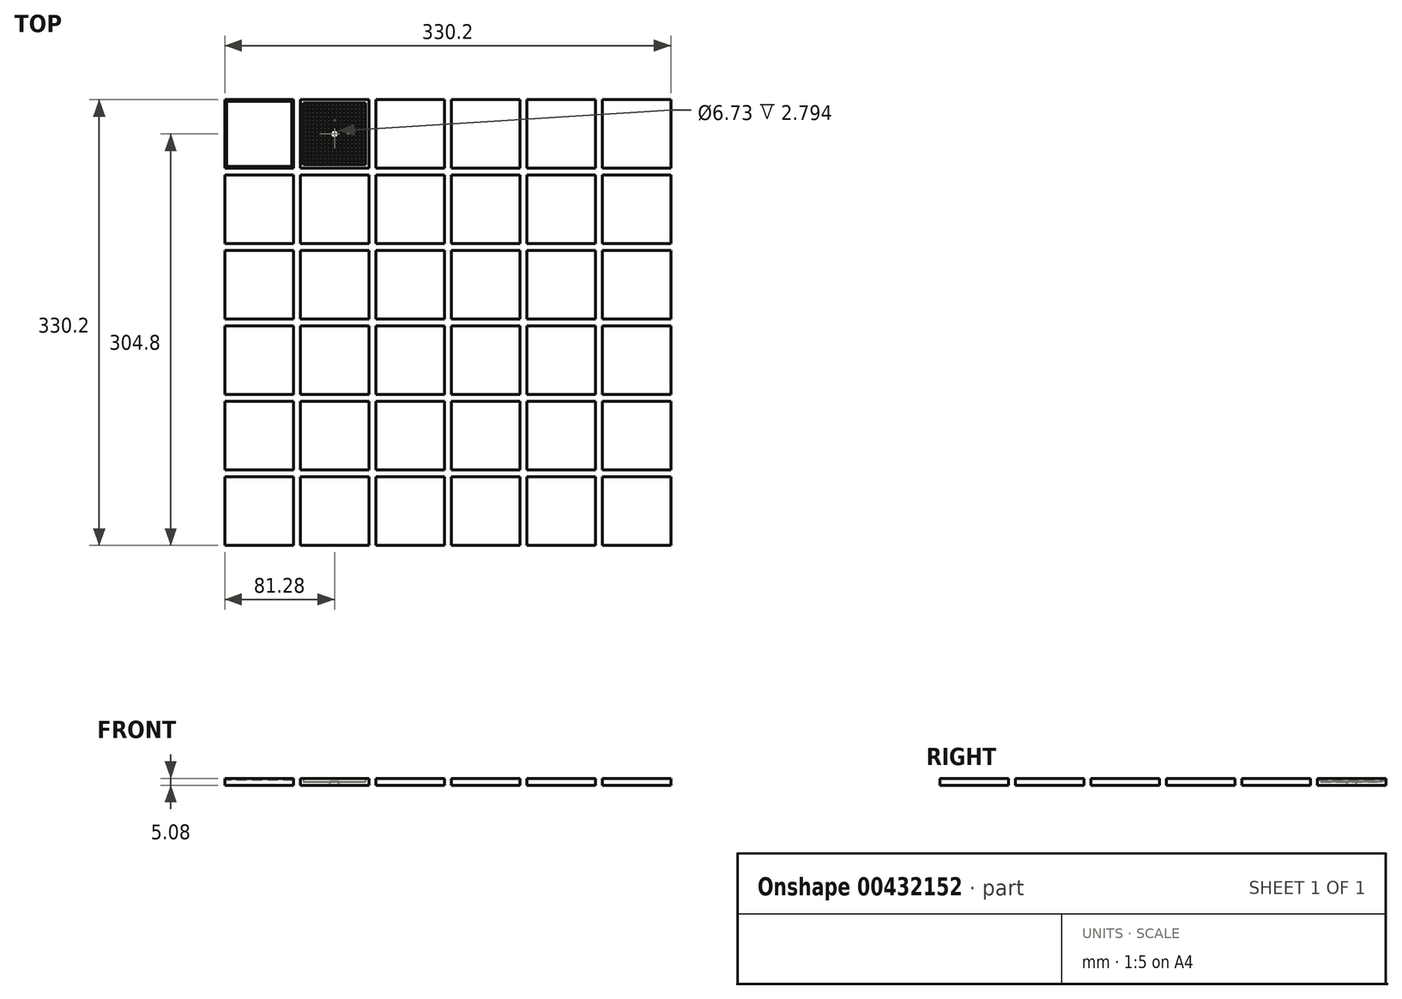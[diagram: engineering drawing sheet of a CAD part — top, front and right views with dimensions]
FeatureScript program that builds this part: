
annotation { "Feature Type Name" : "Feature", "Feature Type Description" : "" }
export const myFeature = defineFeature(function(context is Context, id is Id, definition is map)
    precondition{}
    {
        {
            var Q0;
            Q0=qCreatedBy(makeId("Top.planeOp"),FACE);
            var sketch = newSketch(context, id + "F0", { "sketchPlane" : qUnion([Q0])});
            skLineSegment(sketch, "E0.bottom", {"start": v(0, 0) * mm, "end": v(50.8, 0) * mm});
            skLineSegment(sketch, "E0.top", {"start": v(0, 50.8) * mm, "end": v(50.8, 50.8) * mm});
            skLineSegment(sketch, "E0.left", {"start": v(0, 0) * mm, "end": v(0, 50.8) * mm});
            skLineSegment(sketch, "E0.right", {"start": v(50.8, 0) * mm, "end": v(50.8, 50.8) * mm});
            skLineSegment(sketch, "E1.0.1.0", {"start": v(0, 55.88) * mm, "end": v(0, 106.68) * mm});
            skLineSegment(sketch, "E1.0.1.1", {"start": v(0, 106.68) * mm, "end": v(50.8, 106.68) * mm});
            skLineSegment(sketch, "E1.0.1.2", {"start": v(50.8, 55.88) * mm, "end": v(50.8, 106.68) * mm});
            skLineSegment(sketch, "E1.0.1.3", {"start": v(0, 55.88) * mm, "end": v(50.8, 55.88) * mm});
            skLineSegment(sketch, "E1.0.2.0", {"start": v(0, 111.76) * mm, "end": v(0, 162.56) * mm});
            skLineSegment(sketch, "E1.0.2.1", {"start": v(0, 162.56) * mm, "end": v(50.8, 162.56) * mm});
            skLineSegment(sketch, "E1.0.2.2", {"start": v(50.8, 111.76) * mm, "end": v(50.8, 162.56) * mm});
            skLineSegment(sketch, "E1.0.2.3", {"start": v(0, 111.76) * mm, "end": v(50.8, 111.76) * mm});
            skLineSegment(sketch, "E1.0.3.0", {"start": v(0, 167.64) * mm, "end": v(0, 218.44) * mm});
            skLineSegment(sketch, "E1.0.3.1", {"start": v(0, 218.44) * mm, "end": v(50.8, 218.44) * mm});
            skLineSegment(sketch, "E1.0.3.2", {"start": v(50.8, 167.64) * mm, "end": v(50.8, 218.44) * mm});
            skLineSegment(sketch, "E1.0.3.3", {"start": v(0, 167.64) * mm, "end": v(50.8, 167.64) * mm});
            skLineSegment(sketch, "E1.0.4.0", {"start": v(0, 223.52) * mm, "end": v(0, 274.32) * mm});
            skLineSegment(sketch, "E1.0.4.1", {"start": v(0, 274.32) * mm, "end": v(50.8, 274.32) * mm});
            skLineSegment(sketch, "E1.0.4.2", {"start": v(50.8, 223.52) * mm, "end": v(50.8, 274.32) * mm});
            skLineSegment(sketch, "E1.0.4.3", {"start": v(0, 223.52) * mm, "end": v(50.8, 223.52) * mm});
            skLineSegment(sketch, "E1.0.5.0", {"start": v(0, 279.4) * mm, "end": v(0, 330.2) * mm});
            skLineSegment(sketch, "E1.0.5.1", {"start": v(0, 330.2) * mm, "end": v(50.8, 330.2) * mm});
            skLineSegment(sketch, "E1.0.5.2", {"start": v(50.8, 279.4) * mm, "end": v(50.8, 330.2) * mm});
            skLineSegment(sketch, "E1.0.5.3", {"start": v(0, 279.4) * mm, "end": v(50.8, 279.4) * mm});
            skLineSegment(sketch, "E1.1.0.0", {"start": v(-55.88, 0) * mm, "end": v(-55.88, 50.8) * mm});
            skLineSegment(sketch, "E1.1.0.1", {"start": v(-55.88, 50.8) * mm, "end": v(-5.08, 50.8) * mm});
            skLineSegment(sketch, "E1.1.0.2", {"start": v(-5.08, 0) * mm, "end": v(-5.08, 50.8) * mm});
            skLineSegment(sketch, "E1.1.0.3", {"start": v(-55.88, 0) * mm, "end": v(-5.08, 0) * mm});
            skLineSegment(sketch, "E1.1.1.0", {"start": v(-55.88, 55.88) * mm, "end": v(-55.88, 106.68) * mm});
            skLineSegment(sketch, "E1.1.1.1", {"start": v(-55.88, 106.68) * mm, "end": v(-5.08, 106.68) * mm});
            skLineSegment(sketch, "E1.1.1.2", {"start": v(-5.08, 55.88) * mm, "end": v(-5.08, 106.68) * mm});
            skLineSegment(sketch, "E1.1.1.3", {"start": v(-55.88, 55.88) * mm, "end": v(-5.08, 55.88) * mm});
            skLineSegment(sketch, "E1.1.2.0", {"start": v(-55.88, 111.76) * mm, "end": v(-55.88, 162.56) * mm});
            skLineSegment(sketch, "E1.1.2.1", {"start": v(-55.88, 162.56) * mm, "end": v(-5.08, 162.56) * mm});
            skLineSegment(sketch, "E1.1.2.2", {"start": v(-5.08, 111.76) * mm, "end": v(-5.08, 162.56) * mm});
            skLineSegment(sketch, "E1.1.2.3", {"start": v(-55.88, 111.76) * mm, "end": v(-5.08, 111.76) * mm});
            skLineSegment(sketch, "E1.1.3.0", {"start": v(-55.88, 167.64) * mm, "end": v(-55.88, 218.44) * mm});
            skLineSegment(sketch, "E1.1.3.1", {"start": v(-55.88, 218.44) * mm, "end": v(-5.08, 218.44) * mm});
            skLineSegment(sketch, "E1.1.3.2", {"start": v(-5.08, 167.64) * mm, "end": v(-5.08, 218.44) * mm});
            skLineSegment(sketch, "E1.1.3.3", {"start": v(-55.88, 167.64) * mm, "end": v(-5.08, 167.64) * mm});
            skLineSegment(sketch, "E1.1.4.0", {"start": v(-55.88, 223.52) * mm, "end": v(-55.88, 274.32) * mm});
            skLineSegment(sketch, "E1.1.4.1", {"start": v(-55.88, 274.32) * mm, "end": v(-5.08, 274.32) * mm});
            skLineSegment(sketch, "E1.1.4.2", {"start": v(-5.08, 223.52) * mm, "end": v(-5.08, 274.32) * mm});
            skLineSegment(sketch, "E1.1.4.3", {"start": v(-55.88, 223.52) * mm, "end": v(-5.08, 223.52) * mm});
            skLineSegment(sketch, "E1.1.5.0", {"start": v(-55.88, 279.4) * mm, "end": v(-55.88, 330.2) * mm});
            skLineSegment(sketch, "E1.1.5.1", {"start": v(-55.88, 330.2) * mm, "end": v(-5.08, 330.2) * mm});
            skLineSegment(sketch, "E1.1.5.2", {"start": v(-5.08, 279.4) * mm, "end": v(-5.08, 330.2) * mm});
            skLineSegment(sketch, "E1.1.5.3", {"start": v(-55.88, 279.4) * mm, "end": v(-5.08, 279.4) * mm});
            skLineSegment(sketch, "E1.2.0.0", {"start": v(-111.76, 0) * mm, "end": v(-111.76, 50.8) * mm});
            skLineSegment(sketch, "E1.2.0.1", {"start": v(-111.76, 50.8) * mm, "end": v(-60.96, 50.8) * mm});
            skLineSegment(sketch, "E1.2.0.2", {"start": v(-60.96, 0) * mm, "end": v(-60.96, 50.8) * mm});
            skLineSegment(sketch, "E1.2.0.3", {"start": v(-111.76, 0) * mm, "end": v(-60.96, 0) * mm});
            skLineSegment(sketch, "E1.2.1.0", {"start": v(-111.76, 55.88) * mm, "end": v(-111.76, 106.68) * mm});
            skLineSegment(sketch, "E1.2.1.1", {"start": v(-111.76, 106.68) * mm, "end": v(-60.96, 106.68) * mm});
            skLineSegment(sketch, "E1.2.1.2", {"start": v(-60.96, 55.88) * mm, "end": v(-60.96, 106.68) * mm});
            skLineSegment(sketch, "E1.2.1.3", {"start": v(-111.76, 55.88) * mm, "end": v(-60.96, 55.88) * mm});
            skLineSegment(sketch, "E1.2.2.0", {"start": v(-111.76, 111.76) * mm, "end": v(-111.76, 162.56) * mm});
            skLineSegment(sketch, "E1.2.2.1", {"start": v(-111.76, 162.56) * mm, "end": v(-60.96, 162.56) * mm});
            skLineSegment(sketch, "E1.2.2.2", {"start": v(-60.96, 111.76) * mm, "end": v(-60.96, 162.56) * mm});
            skLineSegment(sketch, "E1.2.2.3", {"start": v(-111.76, 111.76) * mm, "end": v(-60.96, 111.76) * mm});
            skLineSegment(sketch, "E1.2.3.0", {"start": v(-111.76, 167.64) * mm, "end": v(-111.76, 218.44) * mm});
            skLineSegment(sketch, "E1.2.3.1", {"start": v(-111.76, 218.44) * mm, "end": v(-60.96, 218.44) * mm});
            skLineSegment(sketch, "E1.2.3.2", {"start": v(-60.96, 167.64) * mm, "end": v(-60.96, 218.44) * mm});
            skLineSegment(sketch, "E1.2.3.3", {"start": v(-111.76, 167.64) * mm, "end": v(-60.96, 167.64) * mm});
            skLineSegment(sketch, "E1.2.4.0", {"start": v(-111.76, 223.52) * mm, "end": v(-111.76, 274.32) * mm});
            skLineSegment(sketch, "E1.2.4.1", {"start": v(-111.76, 274.32) * mm, "end": v(-60.96, 274.32) * mm});
            skLineSegment(sketch, "E1.2.4.2", {"start": v(-60.96, 223.52) * mm, "end": v(-60.96, 274.32) * mm});
            skLineSegment(sketch, "E1.2.4.3", {"start": v(-111.76, 223.52) * mm, "end": v(-60.96, 223.52) * mm});
            skLineSegment(sketch, "E1.2.5.0", {"start": v(-111.76, 279.4) * mm, "end": v(-111.76, 330.2) * mm});
            skLineSegment(sketch, "E1.2.5.1", {"start": v(-111.76, 330.2) * mm, "end": v(-60.96, 330.2) * mm});
            skLineSegment(sketch, "E1.2.5.2", {"start": v(-60.96, 279.4) * mm, "end": v(-60.96, 330.2) * mm});
            skLineSegment(sketch, "E1.2.5.3", {"start": v(-111.76, 279.4) * mm, "end": v(-60.96, 279.4) * mm});
            skLineSegment(sketch, "E1.3.0.0", {"start": v(-167.64, 0) * mm, "end": v(-167.64, 50.8) * mm});
            skLineSegment(sketch, "E1.3.0.1", {"start": v(-167.64, 50.8) * mm, "end": v(-116.84, 50.8) * mm});
            skLineSegment(sketch, "E1.3.0.2", {"start": v(-116.84, 0) * mm, "end": v(-116.84, 50.8) * mm});
            skLineSegment(sketch, "E1.3.0.3", {"start": v(-167.64, 0) * mm, "end": v(-116.84, 0) * mm});
            skLineSegment(sketch, "E1.3.1.0", {"start": v(-167.64, 55.88) * mm, "end": v(-167.64, 106.68) * mm});
            skLineSegment(sketch, "E1.3.1.1", {"start": v(-167.64, 106.68) * mm, "end": v(-116.84, 106.68) * mm});
            skLineSegment(sketch, "E1.3.1.2", {"start": v(-116.84, 55.88) * mm, "end": v(-116.84, 106.68) * mm});
            skLineSegment(sketch, "E1.3.1.3", {"start": v(-167.64, 55.88) * mm, "end": v(-116.84, 55.88) * mm});
            skLineSegment(sketch, "E1.3.2.0", {"start": v(-167.64, 111.76) * mm, "end": v(-167.64, 162.56) * mm});
            skLineSegment(sketch, "E1.3.2.1", {"start": v(-167.64, 162.56) * mm, "end": v(-116.84, 162.56) * mm});
            skLineSegment(sketch, "E1.3.2.2", {"start": v(-116.84, 111.76) * mm, "end": v(-116.84, 162.56) * mm});
            skLineSegment(sketch, "E1.3.2.3", {"start": v(-167.64, 111.76) * mm, "end": v(-116.84, 111.76) * mm});
            skLineSegment(sketch, "E1.3.3.0", {"start": v(-167.64, 167.64) * mm, "end": v(-167.64, 218.44) * mm});
            skLineSegment(sketch, "E1.3.3.1", {"start": v(-167.64, 218.44) * mm, "end": v(-116.84, 218.44) * mm});
            skLineSegment(sketch, "E1.3.3.2", {"start": v(-116.84, 167.64) * mm, "end": v(-116.84, 218.44) * mm});
            skLineSegment(sketch, "E1.3.3.3", {"start": v(-167.64, 167.64) * mm, "end": v(-116.84, 167.64) * mm});
            skLineSegment(sketch, "E1.3.4.0", {"start": v(-167.64, 223.52) * mm, "end": v(-167.64, 274.32) * mm});
            skLineSegment(sketch, "E1.3.4.1", {"start": v(-167.64, 274.32) * mm, "end": v(-116.84, 274.32) * mm});
            skLineSegment(sketch, "E1.3.4.2", {"start": v(-116.84, 223.52) * mm, "end": v(-116.84, 274.32) * mm});
            skLineSegment(sketch, "E1.3.4.3", {"start": v(-167.64, 223.52) * mm, "end": v(-116.84, 223.52) * mm});
            skLineSegment(sketch, "E1.3.5.0", {"start": v(-167.64, 279.4) * mm, "end": v(-167.64, 330.2) * mm});
            skLineSegment(sketch, "E1.3.5.1", {"start": v(-167.64, 330.2) * mm, "end": v(-116.84, 330.2) * mm});
            skLineSegment(sketch, "E1.3.5.2", {"start": v(-116.84, 279.4) * mm, "end": v(-116.84, 330.2) * mm});
            skLineSegment(sketch, "E1.3.5.3", {"start": v(-167.64, 279.4) * mm, "end": v(-116.84, 279.4) * mm});
            skLineSegment(sketch, "E1.4.0.0", {"start": v(-223.52, 0) * mm, "end": v(-223.52, 50.8) * mm});
            skLineSegment(sketch, "E1.4.0.1", {"start": v(-223.52, 50.8) * mm, "end": v(-172.72, 50.8) * mm});
            skLineSegment(sketch, "E1.4.0.2", {"start": v(-172.72, 0) * mm, "end": v(-172.72, 50.8) * mm});
            skLineSegment(sketch, "E1.4.0.3", {"start": v(-223.52, 0) * mm, "end": v(-172.72, 0) * mm});
            skLineSegment(sketch, "E1.4.1.0", {"start": v(-223.52, 55.88) * mm, "end": v(-223.52, 106.68) * mm});
            skLineSegment(sketch, "E1.4.1.1", {"start": v(-223.52, 106.68) * mm, "end": v(-172.72, 106.68) * mm});
            skLineSegment(sketch, "E1.4.1.2", {"start": v(-172.72, 55.88) * mm, "end": v(-172.72, 106.68) * mm});
            skLineSegment(sketch, "E1.4.1.3", {"start": v(-223.52, 55.88) * mm, "end": v(-172.72, 55.88) * mm});
            skLineSegment(sketch, "E1.4.2.0", {"start": v(-223.52, 111.76) * mm, "end": v(-223.52, 162.56) * mm});
            skLineSegment(sketch, "E1.4.2.1", {"start": v(-223.52, 162.56) * mm, "end": v(-172.72, 162.56) * mm});
            skLineSegment(sketch, "E1.4.2.2", {"start": v(-172.72, 111.76) * mm, "end": v(-172.72, 162.56) * mm});
            skLineSegment(sketch, "E1.4.2.3", {"start": v(-223.52, 111.76) * mm, "end": v(-172.72, 111.76) * mm});
            skLineSegment(sketch, "E1.4.3.0", {"start": v(-223.52, 167.64) * mm, "end": v(-223.52, 218.44) * mm});
            skLineSegment(sketch, "E1.4.3.1", {"start": v(-223.52, 218.44) * mm, "end": v(-172.72, 218.44) * mm});
            skLineSegment(sketch, "E1.4.3.2", {"start": v(-172.72, 167.64) * mm, "end": v(-172.72, 218.44) * mm});
            skLineSegment(sketch, "E1.4.3.3", {"start": v(-223.52, 167.64) * mm, "end": v(-172.72, 167.64) * mm});
            skLineSegment(sketch, "E1.4.4.0", {"start": v(-223.52, 223.52) * mm, "end": v(-223.52, 274.32) * mm});
            skLineSegment(sketch, "E1.4.4.1", {"start": v(-223.52, 274.32) * mm, "end": v(-172.72, 274.32) * mm});
            skLineSegment(sketch, "E1.4.4.2", {"start": v(-172.72, 223.52) * mm, "end": v(-172.72, 274.32) * mm});
            skLineSegment(sketch, "E1.4.4.3", {"start": v(-223.52, 223.52) * mm, "end": v(-172.72, 223.52) * mm});
            skLineSegment(sketch, "E1.4.5.0", {"start": v(-223.52, 279.4) * mm, "end": v(-223.52, 330.2) * mm});
            skLineSegment(sketch, "E1.4.5.1", {"start": v(-223.52, 330.2) * mm, "end": v(-172.72, 330.2) * mm});
            skLineSegment(sketch, "E1.4.5.2", {"start": v(-172.72, 279.4) * mm, "end": v(-172.72, 330.2) * mm});
            skLineSegment(sketch, "E1.4.5.3", {"start": v(-223.52, 279.4) * mm, "end": v(-172.72, 279.4) * mm});
            skLineSegment(sketch, "E1.5.0.0", {"start": v(-279.4, 0) * mm, "end": v(-279.4, 50.8) * mm});
            skLineSegment(sketch, "E1.5.0.1", {"start": v(-279.4, 50.8) * mm, "end": v(-228.6, 50.8) * mm});
            skLineSegment(sketch, "E1.5.0.2", {"start": v(-228.6, 0) * mm, "end": v(-228.6, 50.8) * mm});
            skLineSegment(sketch, "E1.5.0.3", {"start": v(-279.4, 0) * mm, "end": v(-228.6, 0) * mm});
            skLineSegment(sketch, "E1.5.1.0", {"start": v(-279.4, 55.88) * mm, "end": v(-279.4, 106.68) * mm});
            skLineSegment(sketch, "E1.5.1.1", {"start": v(-279.4, 106.68) * mm, "end": v(-228.6, 106.68) * mm});
            skLineSegment(sketch, "E1.5.1.2", {"start": v(-228.6, 55.88) * mm, "end": v(-228.6, 106.68) * mm});
            skLineSegment(sketch, "E1.5.1.3", {"start": v(-279.4, 55.88) * mm, "end": v(-228.6, 55.88) * mm});
            skLineSegment(sketch, "E1.5.2.0", {"start": v(-279.4, 111.76) * mm, "end": v(-279.4, 162.56) * mm});
            skLineSegment(sketch, "E1.5.2.1", {"start": v(-279.4, 162.56) * mm, "end": v(-228.6, 162.56) * mm});
            skLineSegment(sketch, "E1.5.2.2", {"start": v(-228.6, 111.76) * mm, "end": v(-228.6, 162.56) * mm});
            skLineSegment(sketch, "E1.5.2.3", {"start": v(-279.4, 111.76) * mm, "end": v(-228.6, 111.76) * mm});
            skLineSegment(sketch, "E1.5.3.0", {"start": v(-279.4, 167.64) * mm, "end": v(-279.4, 218.44) * mm});
            skLineSegment(sketch, "E1.5.3.1", {"start": v(-279.4, 218.44) * mm, "end": v(-228.6, 218.44) * mm});
            skLineSegment(sketch, "E1.5.3.2", {"start": v(-228.6, 167.64) * mm, "end": v(-228.6, 218.44) * mm});
            skLineSegment(sketch, "E1.5.3.3", {"start": v(-279.4, 167.64) * mm, "end": v(-228.6, 167.64) * mm});
            skLineSegment(sketch, "E1.5.4.0", {"start": v(-279.4, 223.52) * mm, "end": v(-279.4, 274.32) * mm});
            skLineSegment(sketch, "E1.5.4.1", {"start": v(-279.4, 274.32) * mm, "end": v(-228.6, 274.32) * mm});
            skLineSegment(sketch, "E1.5.4.2", {"start": v(-228.6, 223.52) * mm, "end": v(-228.6, 274.32) * mm});
            skLineSegment(sketch, "E1.5.4.3", {"start": v(-279.4, 223.52) * mm, "end": v(-228.6, 223.52) * mm});
            skLineSegment(sketch, "E1.5.5.0", {"start": v(-279.4, 279.4) * mm, "end": v(-279.4, 330.2) * mm});
            skLineSegment(sketch, "E1.5.5.1", {"start": v(-279.4, 330.2) * mm, "end": v(-228.6, 330.2) * mm});
            skLineSegment(sketch, "E1.5.5.2", {"start": v(-228.6, 279.4) * mm, "end": v(-228.6, 330.2) * mm});
            skLineSegment(sketch, "E1.5.5.3", {"start": v(-279.4, 279.4) * mm, "end": v(-228.6, 279.4) * mm});
            skLineSegment(sketch, "E1.direction1", {"start": v(0, 0) * mm, "end": v(-55.88, 0) * mm, "construction": true});
            skLineSegment(sketch, "E1.direction2", {"start": v(0, 0) * mm, "end": v(0, 55.88) * mm, "construction": true});
            skSolve(sketch);
        }
        {
            var Q0;
            Q0=makeQuery(id+"F0.imprint","IMPRINT",FACE,{"disambiguationData":[TD([[makeQuery(id+"F0.imprint","IMPRINT",EDGE,{"derivedFrom":sQuery(id+"F0.wireOp",EDGE,"E1.4.2.0")}),-1.0]])]});
            var Q1;
            Q1=makeQuery(id+"F0.imprint","IMPRINT",FACE,{"disambiguationData":[TD([[makeQuery(id+"F0.imprint","IMPRINT",EDGE,{"derivedFrom":sQuery(id+"F0.wireOp",EDGE,"E1.4.5.0")}),-1.0]])]});
            var Q2;
            Q2=makeQuery(id+"F0.imprint","IMPRINT",FACE,{"disambiguationData":[TD([[makeQuery(id+"F0.imprint","IMPRINT",EDGE,{"derivedFrom":sQuery(id+"F0.wireOp",EDGE,"E1.4.3.0")}),-1.0]])]});
            var Q3;
            Q3=makeQuery(id+"F0.imprint","IMPRINT",FACE,{"disambiguationData":[TD([[makeQuery(id+"F0.imprint","IMPRINT",EDGE,{"derivedFrom":sQuery(id+"F0.wireOp",EDGE,"E1.5.0.0")}),-1.0]])]});
            var Q4;
            Q4=makeQuery(id+"F0.imprint","IMPRINT",FACE,{"disambiguationData":[TD([[makeQuery(id+"F0.imprint","IMPRINT",EDGE,{"derivedFrom":sQuery(id+"F0.wireOp",EDGE,"E1.4.4.0")}),-1.0]])]});
            var Q5;
            Q5=makeQuery(id+"F0.imprint","IMPRINT",FACE,{"disambiguationData":[TD([[makeQuery(id+"F0.imprint","IMPRINT",EDGE,{"derivedFrom":sQuery(id+"F0.wireOp",EDGE,"E1.2.4.0")}),-1.0]])]});
            var Q6;
            Q6=makeQuery(id+"F0.imprint","IMPRINT",FACE,{"disambiguationData":[TD([[makeQuery(id+"F0.imprint","IMPRINT",EDGE,{"derivedFrom":sQuery(id+"F0.wireOp",EDGE,"E1.5.2.0")}),-1.0]])]});
            var Q7;
            Q7=makeQuery(id+"F0.imprint","IMPRINT",FACE,{"disambiguationData":[TD([[makeQuery(id+"F0.imprint","IMPRINT",EDGE,{"derivedFrom":sQuery(id+"F0.wireOp",EDGE,"E1.2.5.0")}),-1.0]])]});
            var Q8;
            Q8=makeQuery(id+"F0.imprint","IMPRINT",FACE,{"disambiguationData":[TD([[makeQuery(id+"F0.imprint","IMPRINT",EDGE,{"derivedFrom":sQuery(id+"F0.wireOp",EDGE,"E1.5.3.0")}),-1.0]])]});
            var Q9;
            Q9=makeQuery(id+"F0.imprint","IMPRINT",FACE,{"disambiguationData":[TD([[makeQuery(id+"F0.imprint","IMPRINT",EDGE,{"derivedFrom":sQuery(id+"F0.wireOp",EDGE,"E1.3.0.0")}),-1.0]])]});
            var Q10;
            Q10=makeQuery(id+"F0.imprint","IMPRINT",FACE,{"disambiguationData":[TD([[makeQuery(id+"F0.imprint","IMPRINT",EDGE,{"derivedFrom":sQuery(id+"F0.wireOp",EDGE,"E1.5.4.0")}),-1.0]])]});
            var Q11;
            Q11=makeQuery(id+"F0.imprint","IMPRINT",FACE,{"disambiguationData":[TD([[makeQuery(id+"F0.imprint","IMPRINT",EDGE,{"derivedFrom":sQuery(id+"F0.wireOp",EDGE,"E1.3.1.0")}),-1.0]])]});
            var Q12;
            Q12=makeQuery(id+"F0.imprint","IMPRINT",FACE,{"disambiguationData":[TD([[makeQuery(id+"F0.imprint","IMPRINT",EDGE,{"derivedFrom":sQuery(id+"F0.wireOp",EDGE,"E1.5.5.0")}),-1.0]])]});
            var Q13;
            Q13=makeQuery(id+"F0.imprint","IMPRINT",FACE,{"disambiguationData":[TD([[makeQuery(id+"F0.imprint","IMPRINT",EDGE,{"derivedFrom":sQuery(id+"F0.wireOp",EDGE,"E1.3.2.0")}),-1.0]])]});
            var Q14;
            Q14=makeQuery(id+"F0.imprint","IMPRINT",FACE,{"disambiguationData":[TD([[makeQuery(id+"F0.imprint","IMPRINT",EDGE,{"derivedFrom":sQuery(id+"F0.wireOp",EDGE,"E1.3.3.0")}),-1.0]])]});
            var Q15;
            Q15=makeQuery(id+"F0.imprint","IMPRINT",FACE,{"disambiguationData":[TD([[makeQuery(id+"F0.imprint","IMPRINT",EDGE,{"derivedFrom":sQuery(id+"F0.wireOp",EDGE,"E1.3.4.0")}),-1.0]])]});
            var Q16;
            Q16=makeQuery(id+"F0.imprint","IMPRINT",FACE,{"disambiguationData":[TD([[makeQuery(id+"F0.imprint","IMPRINT",EDGE,{"derivedFrom":sQuery(id+"F0.wireOp",EDGE,"E1.2.3.0")}),-1.0]])]});
            var Q17;
            Q17=makeQuery(id+"F0.imprint","IMPRINT",FACE,{"disambiguationData":[TD([[makeQuery(id+"F0.imprint","IMPRINT",EDGE,{"derivedFrom":sQuery(id+"F0.wireOp",EDGE,"E1.2.1.0")}),-1.0]])]});
            var Q18;
            Q18=makeQuery(id+"F0.imprint","IMPRINT",FACE,{"disambiguationData":[TD([[makeQuery(id+"F0.imprint","IMPRINT",EDGE,{"derivedFrom":sQuery(id+"F0.wireOp",EDGE,"E1.2.2.0")}),-1.0]])]});
            var Q19;
            Q19=makeQuery(id+"F0.imprint","IMPRINT",FACE,{"disambiguationData":[TD([[makeQuery(id+"F0.imprint","IMPRINT",EDGE,{"derivedFrom":sQuery(id+"F0.wireOp",EDGE,"E1.0.1.0")}),-1.0]])]});
            var Q20;
            Q20=makeQuery(id+"F0.imprint","IMPRINT",FACE,{"disambiguationData":[TD([[makeQuery(id+"F0.imprint","IMPRINT",EDGE,{"derivedFrom":sQuery(id+"F0.wireOp",EDGE,"E1.0.2.0")}),-1.0]])]});
            var Q21;
            Q21=makeQuery(id+"F0.imprint","IMPRINT",FACE,{"disambiguationData":[TD([[makeQuery(id+"F0.imprint","IMPRINT",EDGE,{"derivedFrom":sQuery(id+"F0.wireOp",EDGE,"E1.0.3.0")}),-1.0]])]});
            var Q22;
            Q22=makeQuery(id+"F0.imprint","IMPRINT",FACE,{"disambiguationData":[TD([[makeQuery(id+"F0.imprint","IMPRINT",EDGE,{"derivedFrom":sQuery(id+"F0.wireOp",EDGE,"E1.0.4.0")}),-1.0]])]});
            var Q23;
            Q23=makeQuery(id+"F0.imprint","IMPRINT",FACE,{"disambiguationData":[TD([[makeQuery(id+"F0.imprint","IMPRINT",EDGE,{"derivedFrom":sQuery(id+"F0.wireOp",EDGE,"E1.0.5.0")}),-1.0]])]});
            var Q24;
            Q24=makeQuery(id+"F0.imprint","IMPRINT",FACE,{"disambiguationData":[TD([[makeQuery(id+"F0.imprint","IMPRINT",EDGE,{"derivedFrom":sQuery(id+"F0.wireOp",EDGE,"E1.1.0.0")}),-1.0]])]});
            var Q25;
            Q25=makeQuery(id+"F0.imprint","IMPRINT",FACE,{"disambiguationData":[TD([[makeQuery(id+"F0.imprint","IMPRINT",EDGE,{"derivedFrom":sQuery(id+"F0.wireOp",EDGE,"E1.1.1.0")}),-1.0]])]});
            var Q26;
            Q26=makeQuery(id+"F0.imprint","IMPRINT",FACE,{"disambiguationData":[TD([[makeQuery(id+"F0.imprint","IMPRINT",EDGE,{"derivedFrom":sQuery(id+"F0.wireOp",EDGE,"E1.1.2.0")}),-1.0]])]});
            var Q27;
            Q27=makeQuery(id+"F0.imprint","IMPRINT",FACE,{"disambiguationData":[TD([[makeQuery(id+"F0.imprint","IMPRINT",EDGE,{"derivedFrom":sQuery(id+"F0.wireOp",EDGE,"E1.1.3.0")}),-1.0]])]});
            var Q28;
            Q28=makeQuery(id+"F0.imprint","IMPRINT",FACE,{"disambiguationData":[TD([[makeQuery(id+"F0.imprint","IMPRINT",EDGE,{"derivedFrom":sQuery(id+"F0.wireOp",EDGE,"E1.1.4.0")}),-1.0]])]});
            var Q29;
            Q29=makeQuery(id+"F0.imprint","IMPRINT",FACE,{"disambiguationData":[TD([[makeQuery(id+"F0.imprint","IMPRINT",EDGE,{"derivedFrom":sQuery(id+"F0.wireOp",EDGE,"E1.1.5.0")}),-1.0]])]});
            var Q30;
            Q30=makeQuery(id+"F0.imprint","IMPRINT",FACE,{"disambiguationData":[TD([[makeQuery(id+"F0.imprint","IMPRINT",EDGE,{"derivedFrom":sQuery(id+"F0.wireOp",EDGE,"E1.2.0.0")}),-1.0]])]});
            var Q31;
            Q31=makeQuery(id+"F0.imprint","IMPRINT",FACE,{"disambiguationData":[TD([[makeQuery(id+"F0.imprint","IMPRINT",EDGE,{"derivedFrom":sQuery(id+"F0.wireOp",EDGE,"E1.3.5.0")}),-1.0]])]});
            var Q32;
            Q32=makeQuery(id+"F0.imprint","IMPRINT",FACE,{"disambiguationData":[TD([[makeQuery(id+"F0.imprint","IMPRINT",EDGE,{"derivedFrom":sQuery(id+"F0.wireOp",EDGE,"E1.4.0.0")}),-1.0]])]});
            var Q33;
            Q33=makeQuery(id+"F0.imprint","IMPRINT",FACE,{"disambiguationData":[TD([[makeQuery(id+"F0.imprint","IMPRINT",EDGE,{"derivedFrom":sQuery(id+"F0.wireOp",EDGE,"E1.5.1.0")}),-1.0]])]});
            var Q34;
            Q34=makeQuery(id+"F0.imprint","IMPRINT",FACE,{"disambiguationData":[TD([[makeQuery(id+"F0.imprint","IMPRINT",EDGE,{"derivedFrom":sQuery(id+"F0.wireOp",EDGE,"E1.4.1.0")}),-1.0]])]});
            var Q35;
            Q35=makeQuery(id+"F0.imprint","IMPRINT",FACE,{"disambiguationData":[TD([[makeQuery(id+"F0.imprint","IMPRINT",EDGE,{"derivedFrom":sQuery(id+"F0.wireOp",EDGE,"E0.bottom")}),1.0]])]});
            extrude(context, id + "F1", {"entities" : qUnion([Q0, Q1, Q2, Q3, Q4, Q5, Q6, Q7, Q8, Q9, Q10, Q11, Q12, Q13, Q14, Q15, Q16, Q17, Q18, Q19, Q20, Q21, Q22, Q23, Q24, Q25, Q26, Q27, Q28, Q29, Q30, Q31, Q32, Q33, Q34, Q35]), "depth" : 5.08 * mm});
        }
        {
            var Q0;
            Q0=makeQuery(id+"F1.opExtrude","CAP_EDGE",EDGE,{"disambiguationData":[OSD([sQuery(id+"F0.wireOp",EDGE,"E1.5.5.0")])],"isStart":false});
            var Q1;
            Q1=makeQuery(id+"F1.opExtrude","CAP_EDGE",EDGE,{"disambiguationData":[OSD([sQuery(id+"F0.wireOp",EDGE,"E1.5.5.3")])],"isStart":false});
            var Q2;
            Q2=makeQuery(id+"F1.opExtrude","CAP_EDGE",EDGE,{"disambiguationData":[OSD([sQuery(id+"F0.wireOp",EDGE,"E1.5.5.2")])],"isStart":false});
            var Q3;
            Q3=makeQuery(id+"F1.opExtrude","CAP_EDGE",EDGE,{"disambiguationData":[OSD([sQuery(id+"F0.wireOp",EDGE,"E1.5.5.1")])],"isStart":false});
            chamfer(context, id + "F2", {"entities" : qUnion([Q0, Q1, Q2, Q3]), "width" : 1.27 * mm, "tangentPropagation" : true});
        }
        {
            var Q0;
            Q0=makeQuery(id+"F1.opExtrude","CAP_FACE",FACE,{"disambiguationData":[OSD([sQuery(id+"F0.wireOp",EDGE,"E1.4.5.0"),sQuery(id+"F0.wireOp",EDGE,"E1.4.5.1"),sQuery(id+"F0.wireOp",EDGE,"E1.4.5.2"),sQuery(id+"F0.wireOp",EDGE,"E1.4.5.3")])],"isStart":false});
            shell(context, id + "F3", {"entities" : qUnion([Q0]), "thickness" : 2.54 * mm});
        }
        {
            var Q0;
            Q0=makeQuery(id+"F3.opShell","OFFSET_FACE",FACE,{"disambiguationData":[OSD([sQuery(id+"F0.wireOp",EDGE,"E1.4.5.0"),sQuery(id+"F0.wireOp",EDGE,"E1.4.5.1"),sQuery(id+"F0.wireOp",EDGE,"E1.4.5.2"),sQuery(id+"F0.wireOp",EDGE,"E1.4.5.3")])]});
            var sketch = newSketch(context, id + "F4", { "sketchPlane" : qUnion([Q0])});
            skLineSegment(sketch, "E2", {"start": v(-220.98, 327.66) * mm, "end": v(-220.73, 327.66) * mm});
            skLineSegment(sketch, "E3", {"start": v(-220.73, 327.66) * mm, "end": v(-220.73, 327.41) * mm});
            skLineSegment(sketch, "E4", {"start": v(-220.73, 327.41) * mm, "end": v(-220.98, 327.41) * mm});
            skLineSegment(sketch, "E5.bottom", {"start": v(-220.73, 327.41) * mm, "end": v(-218.2, 327.41) * mm});
            skLineSegment(sketch, "E5.top", {"start": v(-220.73, 324.87) * mm, "end": v(-218.2, 324.87) * mm});
            skLineSegment(sketch, "E5.left", {"start": v(-220.73, 327.41) * mm, "end": v(-220.73, 324.87) * mm});
            skLineSegment(sketch, "E5.right", {"start": v(-218.2, 327.41) * mm, "end": v(-218.2, 324.87) * mm});
            skCircle(sketch, "E6", {"center": v(-198.12, 304.8) * mm, "radius": 3.18 * mm});
            skPoint(sketch, "E6.centerSnap0", {"position": v(-220.98, 304.8) * mm});
            skPoint(sketch, "E6.centerSnap1", {"position": v(-198.12, 327.66) * mm});
            skLineSegment(sketch, "E7.0.1.0", {"start": v(-220.73, 322.03) * mm, "end": v(-218.2, 322.03) * mm});
            skLineSegment(sketch, "E7.0.1.1", {"start": v(-220.73, 324.57) * mm, "end": v(-220.73, 322.03) * mm});
            skLineSegment(sketch, "E7.0.1.2", {"start": v(-220.73, 324.57) * mm, "end": v(-218.2, 324.57) * mm});
            skLineSegment(sketch, "E7.0.1.3", {"start": v(-218.2, 324.57) * mm, "end": v(-218.2, 322.03) * mm});
            skLineSegment(sketch, "E7.1.0.0", {"start": v(-217.89, 324.87) * mm, "end": v(-215.35, 324.87) * mm});
            skLineSegment(sketch, "E7.1.0.1", {"start": v(-217.89, 327.41) * mm, "end": v(-217.89, 324.87) * mm});
            skLineSegment(sketch, "E7.1.0.2", {"start": v(-217.89, 327.41) * mm, "end": v(-215.35, 327.41) * mm});
            skLineSegment(sketch, "E7.1.0.3", {"start": v(-215.35, 327.41) * mm, "end": v(-215.35, 324.87) * mm});
            skLineSegment(sketch, "E7.1.1.0", {"start": v(-217.89, 322.03) * mm, "end": v(-215.35, 322.03) * mm});
            skLineSegment(sketch, "E7.1.1.1", {"start": v(-217.89, 324.57) * mm, "end": v(-217.89, 322.03) * mm});
            skLineSegment(sketch, "E7.1.1.2", {"start": v(-217.89, 324.57) * mm, "end": v(-215.35, 324.57) * mm});
            skLineSegment(sketch, "E7.1.1.3", {"start": v(-215.35, 324.57) * mm, "end": v(-215.35, 322.03) * mm});
            skLineSegment(sketch, "E7.2.0.0", {"start": v(-215.04, 324.87) * mm, "end": v(-212.5, 324.87) * mm});
            skLineSegment(sketch, "E7.2.0.1", {"start": v(-215.04, 327.41) * mm, "end": v(-215.04, 324.87) * mm});
            skLineSegment(sketch, "E7.2.0.2", {"start": v(-215.04, 327.41) * mm, "end": v(-212.5, 327.41) * mm});
            skLineSegment(sketch, "E7.2.0.3", {"start": v(-212.5, 327.41) * mm, "end": v(-212.5, 324.87) * mm});
            skLineSegment(sketch, "E7.2.1.0", {"start": v(-215.04, 322.03) * mm, "end": v(-212.5, 322.03) * mm});
            skLineSegment(sketch, "E7.2.1.1", {"start": v(-215.04, 324.57) * mm, "end": v(-215.04, 322.03) * mm});
            skLineSegment(sketch, "E7.2.1.2", {"start": v(-215.04, 324.57) * mm, "end": v(-212.5, 324.57) * mm});
            skLineSegment(sketch, "E7.2.1.3", {"start": v(-212.5, 324.57) * mm, "end": v(-212.5, 322.03) * mm});
            skLineSegment(sketch, "E7.3.0.0", {"start": v(-212.2, 324.87) * mm, "end": v(-209.66, 324.87) * mm});
            skLineSegment(sketch, "E7.3.0.1", {"start": v(-212.2, 327.41) * mm, "end": v(-212.2, 324.87) * mm});
            skLineSegment(sketch, "E7.3.0.2", {"start": v(-212.2, 327.41) * mm, "end": v(-209.66, 327.41) * mm});
            skLineSegment(sketch, "E7.3.0.3", {"start": v(-209.66, 327.41) * mm, "end": v(-209.66, 324.87) * mm});
            skLineSegment(sketch, "E7.3.1.0", {"start": v(-212.2, 322.03) * mm, "end": v(-209.66, 322.03) * mm});
            skLineSegment(sketch, "E7.3.1.1", {"start": v(-212.2, 324.57) * mm, "end": v(-212.2, 322.03) * mm});
            skLineSegment(sketch, "E7.3.1.2", {"start": v(-212.2, 324.57) * mm, "end": v(-209.66, 324.57) * mm});
            skLineSegment(sketch, "E7.3.1.3", {"start": v(-209.66, 324.57) * mm, "end": v(-209.66, 322.03) * mm});
            skLineSegment(sketch, "E7.4.0.0", {"start": v(-209.35, 324.87) * mm, "end": v(-206.81, 324.87) * mm});
            skLineSegment(sketch, "E7.4.0.1", {"start": v(-209.35, 327.41) * mm, "end": v(-209.35, 324.87) * mm});
            skLineSegment(sketch, "E7.4.0.2", {"start": v(-209.35, 327.41) * mm, "end": v(-206.81, 327.41) * mm});
            skLineSegment(sketch, "E7.4.0.3", {"start": v(-206.81, 327.41) * mm, "end": v(-206.81, 324.87) * mm});
            skLineSegment(sketch, "E7.4.1.0", {"start": v(-209.35, 322.03) * mm, "end": v(-206.81, 322.03) * mm});
            skLineSegment(sketch, "E7.4.1.1", {"start": v(-209.35, 324.57) * mm, "end": v(-209.35, 322.03) * mm});
            skLineSegment(sketch, "E7.4.1.2", {"start": v(-209.35, 324.57) * mm, "end": v(-206.81, 324.57) * mm});
            skLineSegment(sketch, "E7.4.1.3", {"start": v(-206.81, 324.57) * mm, "end": v(-206.81, 322.03) * mm});
            skLineSegment(sketch, "E7.5.0.0", {"start": v(-206.5, 324.87) * mm, "end": v(-203.97, 324.87) * mm});
            skLineSegment(sketch, "E7.5.0.1", {"start": v(-206.5, 327.41) * mm, "end": v(-206.5, 324.87) * mm});
            skLineSegment(sketch, "E7.5.0.2", {"start": v(-206.5, 327.41) * mm, "end": v(-203.97, 327.41) * mm});
            skLineSegment(sketch, "E7.5.0.3", {"start": v(-203.97, 327.41) * mm, "end": v(-203.97, 324.87) * mm});
            skLineSegment(sketch, "E7.5.1.0", {"start": v(-206.5, 322.03) * mm, "end": v(-203.97, 322.03) * mm});
            skLineSegment(sketch, "E7.5.1.1", {"start": v(-206.5, 324.57) * mm, "end": v(-206.5, 322.03) * mm});
            skLineSegment(sketch, "E7.5.1.2", {"start": v(-206.5, 324.57) * mm, "end": v(-203.97, 324.57) * mm});
            skLineSegment(sketch, "E7.5.1.3", {"start": v(-203.97, 324.57) * mm, "end": v(-203.97, 322.03) * mm});
            skLineSegment(sketch, "E7.6.0.0", {"start": v(-203.66, 324.87) * mm, "end": v(-201.12, 324.87) * mm});
            skLineSegment(sketch, "E7.6.0.1", {"start": v(-203.66, 327.41) * mm, "end": v(-203.66, 324.87) * mm});
            skLineSegment(sketch, "E7.6.0.2", {"start": v(-203.66, 327.41) * mm, "end": v(-201.12, 327.41) * mm});
            skLineSegment(sketch, "E7.6.0.3", {"start": v(-201.12, 327.41) * mm, "end": v(-201.12, 324.87) * mm});
            skLineSegment(sketch, "E7.6.1.0", {"start": v(-203.66, 322.03) * mm, "end": v(-201.12, 322.03) * mm});
            skLineSegment(sketch, "E7.6.1.1", {"start": v(-203.66, 324.57) * mm, "end": v(-203.66, 322.03) * mm});
            skLineSegment(sketch, "E7.6.1.2", {"start": v(-203.66, 324.57) * mm, "end": v(-201.12, 324.57) * mm});
            skLineSegment(sketch, "E7.6.1.3", {"start": v(-201.12, 324.57) * mm, "end": v(-201.12, 322.03) * mm});
            skLineSegment(sketch, "E7.7.0.0", {"start": v(-200.82, 324.87) * mm, "end": v(-198.28, 324.87) * mm});
            skLineSegment(sketch, "E7.7.0.1", {"start": v(-200.82, 327.41) * mm, "end": v(-200.82, 324.87) * mm});
            skLineSegment(sketch, "E7.7.0.2", {"start": v(-200.82, 327.41) * mm, "end": v(-198.28, 327.41) * mm});
            skLineSegment(sketch, "E7.7.0.3", {"start": v(-198.28, 327.41) * mm, "end": v(-198.28, 324.87) * mm});
            skLineSegment(sketch, "E7.7.1.0", {"start": v(-200.82, 322.03) * mm, "end": v(-198.28, 322.03) * mm});
            skLineSegment(sketch, "E7.7.1.1", {"start": v(-200.82, 324.57) * mm, "end": v(-200.82, 322.03) * mm});
            skLineSegment(sketch, "E7.7.1.2", {"start": v(-200.82, 324.57) * mm, "end": v(-198.28, 324.57) * mm});
            skLineSegment(sketch, "E7.7.1.3", {"start": v(-198.28, 324.57) * mm, "end": v(-198.28, 322.03) * mm});
            skLineSegment(sketch, "E7.8.0.0", {"start": v(-197.97, 324.87) * mm, "end": v(-195.43, 324.87) * mm});
            skLineSegment(sketch, "E7.8.0.1", {"start": v(-197.97, 327.41) * mm, "end": v(-197.97, 324.87) * mm});
            skLineSegment(sketch, "E7.8.0.2", {"start": v(-197.97, 327.41) * mm, "end": v(-195.43, 327.41) * mm});
            skLineSegment(sketch, "E7.8.0.3", {"start": v(-195.43, 327.41) * mm, "end": v(-195.43, 324.87) * mm});
            skLineSegment(sketch, "E7.8.1.0", {"start": v(-197.97, 322.03) * mm, "end": v(-195.43, 322.03) * mm});
            skLineSegment(sketch, "E7.8.1.1", {"start": v(-197.97, 324.57) * mm, "end": v(-197.97, 322.03) * mm});
            skLineSegment(sketch, "E7.8.1.2", {"start": v(-197.97, 324.57) * mm, "end": v(-195.43, 324.57) * mm});
            skLineSegment(sketch, "E7.8.1.3", {"start": v(-195.43, 324.57) * mm, "end": v(-195.43, 322.03) * mm});
            skLineSegment(sketch, "E7.9.0.0", {"start": v(-195.13, 324.87) * mm, "end": v(-192.59, 324.87) * mm});
            skLineSegment(sketch, "E7.9.0.1", {"start": v(-195.13, 327.41) * mm, "end": v(-195.13, 324.87) * mm});
            skLineSegment(sketch, "E7.9.0.2", {"start": v(-195.13, 327.41) * mm, "end": v(-192.59, 327.41) * mm});
            skLineSegment(sketch, "E7.9.0.3", {"start": v(-192.59, 327.41) * mm, "end": v(-192.59, 324.87) * mm});
            skLineSegment(sketch, "E7.9.1.0", {"start": v(-195.13, 322.03) * mm, "end": v(-192.59, 322.03) * mm});
            skLineSegment(sketch, "E7.9.1.1", {"start": v(-195.13, 324.57) * mm, "end": v(-195.13, 322.03) * mm});
            skLineSegment(sketch, "E7.9.1.2", {"start": v(-195.13, 324.57) * mm, "end": v(-192.59, 324.57) * mm});
            skLineSegment(sketch, "E7.9.1.3", {"start": v(-192.59, 324.57) * mm, "end": v(-192.59, 322.03) * mm});
            skLineSegment(sketch, "E7.10.0.0", {"start": v(-192.28, 324.87) * mm, "end": v(-189.74, 324.87) * mm});
            skLineSegment(sketch, "E7.10.0.1", {"start": v(-192.28, 327.41) * mm, "end": v(-192.28, 324.87) * mm});
            skLineSegment(sketch, "E7.10.0.2", {"start": v(-192.28, 327.41) * mm, "end": v(-189.74, 327.41) * mm});
            skLineSegment(sketch, "E7.10.0.3", {"start": v(-189.74, 327.41) * mm, "end": v(-189.74, 324.87) * mm});
            skLineSegment(sketch, "E7.10.1.0", {"start": v(-192.28, 322.03) * mm, "end": v(-189.74, 322.03) * mm});
            skLineSegment(sketch, "E7.10.1.1", {"start": v(-192.28, 324.57) * mm, "end": v(-192.28, 322.03) * mm});
            skLineSegment(sketch, "E7.10.1.2", {"start": v(-192.28, 324.57) * mm, "end": v(-189.74, 324.57) * mm});
            skLineSegment(sketch, "E7.10.1.3", {"start": v(-189.74, 324.57) * mm, "end": v(-189.74, 322.03) * mm});
            skLineSegment(sketch, "E7.11.0.0", {"start": v(-189.44, 324.87) * mm, "end": v(-186.9, 324.87) * mm});
            skLineSegment(sketch, "E7.11.0.1", {"start": v(-189.44, 327.41) * mm, "end": v(-189.44, 324.87) * mm});
            skLineSegment(sketch, "E7.11.0.2", {"start": v(-189.44, 327.41) * mm, "end": v(-186.9, 327.41) * mm});
            skLineSegment(sketch, "E7.11.0.3", {"start": v(-186.9, 327.41) * mm, "end": v(-186.9, 324.87) * mm});
            skLineSegment(sketch, "E7.11.1.0", {"start": v(-189.44, 322.03) * mm, "end": v(-186.9, 322.03) * mm});
            skLineSegment(sketch, "E7.11.1.1", {"start": v(-189.44, 324.57) * mm, "end": v(-189.44, 322.03) * mm});
            skLineSegment(sketch, "E7.11.1.2", {"start": v(-189.44, 324.57) * mm, "end": v(-186.9, 324.57) * mm});
            skLineSegment(sketch, "E7.11.1.3", {"start": v(-186.9, 324.57) * mm, "end": v(-186.9, 322.03) * mm});
            skLineSegment(sketch, "E7.12.0.0", {"start": v(-186.6, 324.87) * mm, "end": v(-184.05, 324.87) * mm});
            skLineSegment(sketch, "E7.12.0.1", {"start": v(-186.6, 327.41) * mm, "end": v(-186.6, 324.87) * mm});
            skLineSegment(sketch, "E7.12.0.2", {"start": v(-186.6, 327.41) * mm, "end": v(-184.05, 327.41) * mm});
            skLineSegment(sketch, "E7.12.0.3", {"start": v(-184.05, 327.41) * mm, "end": v(-184.05, 324.87) * mm});
            skLineSegment(sketch, "E7.12.1.0", {"start": v(-186.6, 322.03) * mm, "end": v(-184.05, 322.03) * mm});
            skLineSegment(sketch, "E7.12.1.1", {"start": v(-186.6, 324.57) * mm, "end": v(-186.6, 322.03) * mm});
            skLineSegment(sketch, "E7.12.1.2", {"start": v(-186.6, 324.57) * mm, "end": v(-184.05, 324.57) * mm});
            skLineSegment(sketch, "E7.12.1.3", {"start": v(-184.05, 324.57) * mm, "end": v(-184.05, 322.03) * mm});
            skLineSegment(sketch, "E7.13.0.0", {"start": v(-183.75, 324.87) * mm, "end": v(-181.2, 324.87) * mm});
            skLineSegment(sketch, "E7.13.0.1", {"start": v(-183.75, 327.41) * mm, "end": v(-183.75, 324.87) * mm});
            skLineSegment(sketch, "E7.13.0.2", {"start": v(-183.75, 327.41) * mm, "end": v(-181.2, 327.41) * mm});
            skLineSegment(sketch, "E7.13.0.3", {"start": v(-181.2, 327.41) * mm, "end": v(-181.2, 324.87) * mm});
            skLineSegment(sketch, "E7.13.1.0", {"start": v(-183.75, 322.03) * mm, "end": v(-181.2, 322.03) * mm});
            skLineSegment(sketch, "E7.13.1.1", {"start": v(-183.75, 324.57) * mm, "end": v(-183.75, 322.03) * mm});
            skLineSegment(sketch, "E7.13.1.2", {"start": v(-183.75, 324.57) * mm, "end": v(-181.2, 324.57) * mm});
            skLineSegment(sketch, "E7.13.1.3", {"start": v(-181.2, 324.57) * mm, "end": v(-181.2, 322.03) * mm});
            skLineSegment(sketch, "E7.14.0.0", {"start": v(-180.9, 324.87) * mm, "end": v(-178.36, 324.87) * mm});
            skLineSegment(sketch, "E7.14.0.1", {"start": v(-180.9, 327.41) * mm, "end": v(-180.9, 324.87) * mm});
            skLineSegment(sketch, "E7.14.0.2", {"start": v(-180.9, 327.41) * mm, "end": v(-178.36, 327.41) * mm});
            skLineSegment(sketch, "E7.14.0.3", {"start": v(-178.36, 327.41) * mm, "end": v(-178.36, 324.87) * mm});
            skLineSegment(sketch, "E7.14.1.0", {"start": v(-180.9, 322.03) * mm, "end": v(-178.36, 322.03) * mm});
            skLineSegment(sketch, "E7.14.1.1", {"start": v(-180.9, 324.57) * mm, "end": v(-180.9, 322.03) * mm});
            skLineSegment(sketch, "E7.14.1.2", {"start": v(-180.9, 324.57) * mm, "end": v(-178.36, 324.57) * mm});
            skLineSegment(sketch, "E7.14.1.3", {"start": v(-178.36, 324.57) * mm, "end": v(-178.36, 322.03) * mm});
            skLineSegment(sketch, "E7.15.0.0", {"start": v(-178.06, 324.87) * mm, "end": v(-175.52, 324.87) * mm});
            skLineSegment(sketch, "E7.15.0.1", {"start": v(-178.06, 327.41) * mm, "end": v(-178.06, 324.87) * mm});
            skLineSegment(sketch, "E7.15.0.2", {"start": v(-178.06, 327.41) * mm, "end": v(-175.52, 327.41) * mm});
            skLineSegment(sketch, "E7.15.0.3", {"start": v(-175.52, 327.41) * mm, "end": v(-175.52, 324.87) * mm});
            skLineSegment(sketch, "E7.15.1.0", {"start": v(-178.06, 322.03) * mm, "end": v(-175.52, 322.03) * mm});
            skLineSegment(sketch, "E7.15.1.1", {"start": v(-178.06, 324.57) * mm, "end": v(-178.06, 322.03) * mm});
            skLineSegment(sketch, "E7.15.1.2", {"start": v(-178.06, 324.57) * mm, "end": v(-175.52, 324.57) * mm});
            skLineSegment(sketch, "E7.15.1.3", {"start": v(-175.52, 324.57) * mm, "end": v(-175.52, 322.03) * mm});
            skLineSegment(sketch, "E7.direction1", {"start": v(-220.73, 324.87) * mm, "end": v(-217.89, 324.87) * mm, "construction": true});
            skLineSegment(sketch, "E7.direction2", {"start": v(-220.73, 324.87) * mm, "end": v(-220.73, 322.03) * mm, "construction": true});
            skLineSegment(sketch, "E8.0.0.2", {"start": v(-220.73, 319.18) * mm, "end": v(-218.2, 319.18) * mm});
            skLineSegment(sketch, "E8.3.0.2", {"start": v(-220.73, 321.72) * mm, "end": v(-220.73, 319.18) * mm});
            skLineSegment(sketch, "E8.6.0.2", {"start": v(-220.73, 321.72) * mm, "end": v(-218.2, 321.72) * mm});
            skLineSegment(sketch, "E8.9.0.2", {"start": v(-218.2, 321.72) * mm, "end": v(-218.2, 319.18) * mm});
            skLineSegment(sketch, "E8.0.0.3", {"start": v(-220.73, 316.34) * mm, "end": v(-218.2, 316.34) * mm});
            skLineSegment(sketch, "E8.3.0.3", {"start": v(-220.73, 318.88) * mm, "end": v(-220.73, 316.34) * mm});
            skLineSegment(sketch, "E8.6.0.3", {"start": v(-220.73, 318.88) * mm, "end": v(-218.2, 318.88) * mm});
            skLineSegment(sketch, "E8.9.0.3", {"start": v(-218.2, 318.88) * mm, "end": v(-218.2, 316.34) * mm});
            skLineSegment(sketch, "E8.0.0.4", {"start": v(-220.73, 313.5) * mm, "end": v(-218.2, 313.5) * mm});
            skLineSegment(sketch, "E8.3.0.4", {"start": v(-220.73, 316.03) * mm, "end": v(-220.73, 313.5) * mm});
            skLineSegment(sketch, "E8.6.0.4", {"start": v(-220.73, 316.03) * mm, "end": v(-218.2, 316.03) * mm});
            skLineSegment(sketch, "E8.9.0.4", {"start": v(-218.2, 316.03) * mm, "end": v(-218.2, 313.5) * mm});
            skLineSegment(sketch, "E8.0.0.5", {"start": v(-220.73, 310.65) * mm, "end": v(-218.2, 310.65) * mm});
            skLineSegment(sketch, "E8.3.0.5", {"start": v(-220.73, 313.19) * mm, "end": v(-220.73, 310.65) * mm});
            skLineSegment(sketch, "E8.6.0.5", {"start": v(-220.73, 313.19) * mm, "end": v(-218.2, 313.19) * mm});
            skLineSegment(sketch, "E8.9.0.5", {"start": v(-218.2, 313.19) * mm, "end": v(-218.2, 310.65) * mm});
            skLineSegment(sketch, "E8.0.0.6", {"start": v(-220.73, 307.8) * mm, "end": v(-218.2, 307.8) * mm});
            skLineSegment(sketch, "E8.3.0.6", {"start": v(-220.73, 310.34) * mm, "end": v(-220.73, 307.8) * mm});
            skLineSegment(sketch, "E8.6.0.6", {"start": v(-220.73, 310.34) * mm, "end": v(-218.2, 310.34) * mm});
            skLineSegment(sketch, "E8.9.0.6", {"start": v(-218.2, 310.34) * mm, "end": v(-218.2, 307.8) * mm});
            skLineSegment(sketch, "E8.0.0.7", {"start": v(-220.73, 304.96) * mm, "end": v(-218.2, 304.96) * mm});
            skLineSegment(sketch, "E8.3.0.7", {"start": v(-220.73, 307.5) * mm, "end": v(-220.73, 304.96) * mm});
            skLineSegment(sketch, "E8.6.0.7", {"start": v(-220.73, 307.5) * mm, "end": v(-218.2, 307.5) * mm});
            skLineSegment(sketch, "E8.9.0.7", {"start": v(-218.2, 307.5) * mm, "end": v(-218.2, 304.96) * mm});
            skLineSegment(sketch, "E8.0.0.8", {"start": v(-220.73, 302.11) * mm, "end": v(-218.2, 302.11) * mm});
            skLineSegment(sketch, "E8.3.0.8", {"start": v(-220.73, 304.65) * mm, "end": v(-220.73, 302.11) * mm});
            skLineSegment(sketch, "E8.6.0.8", {"start": v(-220.73, 304.65) * mm, "end": v(-218.2, 304.65) * mm});
            skLineSegment(sketch, "E8.9.0.8", {"start": v(-218.2, 304.65) * mm, "end": v(-218.2, 302.11) * mm});
            skLineSegment(sketch, "E8.0.0.9", {"start": v(-220.73, 299.27) * mm, "end": v(-218.2, 299.27) * mm});
            skLineSegment(sketch, "E8.3.0.9", {"start": v(-220.73, 301.8) * mm, "end": v(-220.73, 299.27) * mm});
            skLineSegment(sketch, "E8.6.0.9", {"start": v(-220.73, 301.8) * mm, "end": v(-218.2, 301.8) * mm});
            skLineSegment(sketch, "E8.9.0.9", {"start": v(-218.2, 301.8) * mm, "end": v(-218.2, 299.27) * mm});
            skLineSegment(sketch, "E8.0.0.10", {"start": v(-220.73, 296.42) * mm, "end": v(-218.2, 296.42) * mm});
            skLineSegment(sketch, "E8.3.0.10", {"start": v(-220.73, 298.96) * mm, "end": v(-220.73, 296.42) * mm});
            skLineSegment(sketch, "E8.6.0.10", {"start": v(-220.73, 298.96) * mm, "end": v(-218.2, 298.96) * mm});
            skLineSegment(sketch, "E8.9.0.10", {"start": v(-218.2, 298.96) * mm, "end": v(-218.2, 296.42) * mm});
            skLineSegment(sketch, "E8.0.0.11", {"start": v(-220.73, 293.58) * mm, "end": v(-218.2, 293.58) * mm});
            skLineSegment(sketch, "E8.3.0.11", {"start": v(-220.73, 296.12) * mm, "end": v(-220.73, 293.58) * mm});
            skLineSegment(sketch, "E8.6.0.11", {"start": v(-220.73, 296.12) * mm, "end": v(-218.2, 296.12) * mm});
            skLineSegment(sketch, "E8.9.0.11", {"start": v(-218.2, 296.12) * mm, "end": v(-218.2, 293.58) * mm});
            skLineSegment(sketch, "E8.0.0.12", {"start": v(-220.73, 290.73) * mm, "end": v(-218.2, 290.73) * mm});
            skLineSegment(sketch, "E8.3.0.12", {"start": v(-220.73, 293.27) * mm, "end": v(-220.73, 290.73) * mm});
            skLineSegment(sketch, "E8.6.0.12", {"start": v(-220.73, 293.27) * mm, "end": v(-218.2, 293.27) * mm});
            skLineSegment(sketch, "E8.9.0.12", {"start": v(-218.2, 293.27) * mm, "end": v(-218.2, 290.73) * mm});
            skLineSegment(sketch, "E8.0.0.13", {"start": v(-220.73, 287.89) * mm, "end": v(-218.2, 287.89) * mm});
            skLineSegment(sketch, "E8.3.0.13", {"start": v(-220.73, 290.43) * mm, "end": v(-220.73, 287.89) * mm});
            skLineSegment(sketch, "E8.6.0.13", {"start": v(-220.73, 290.43) * mm, "end": v(-218.2, 290.43) * mm});
            skLineSegment(sketch, "E8.9.0.13", {"start": v(-218.2, 290.43) * mm, "end": v(-218.2, 287.89) * mm});
            skLineSegment(sketch, "E8.0.0.14", {"start": v(-220.73, 285.04) * mm, "end": v(-218.2, 285.04) * mm});
            skLineSegment(sketch, "E8.3.0.14", {"start": v(-220.73, 287.58) * mm, "end": v(-220.73, 285.04) * mm});
            skLineSegment(sketch, "E8.6.0.14", {"start": v(-220.73, 287.58) * mm, "end": v(-218.2, 287.58) * mm});
            skLineSegment(sketch, "E8.9.0.14", {"start": v(-218.2, 287.58) * mm, "end": v(-218.2, 285.04) * mm});
            skLineSegment(sketch, "E8.0.0.15", {"start": v(-220.73, 282.2) * mm, "end": v(-218.2, 282.2) * mm});
            skLineSegment(sketch, "E8.3.0.15", {"start": v(-220.73, 284.74) * mm, "end": v(-220.73, 282.2) * mm});
            skLineSegment(sketch, "E8.6.0.15", {"start": v(-220.73, 284.74) * mm, "end": v(-218.2, 284.74) * mm});
            skLineSegment(sketch, "E8.9.0.15", {"start": v(-218.2, 284.74) * mm, "end": v(-218.2, 282.2) * mm});
            skLineSegment(sketch, "E8.0.1.2", {"start": v(-217.89, 319.18) * mm, "end": v(-215.35, 319.18) * mm});
            skLineSegment(sketch, "E8.3.1.2", {"start": v(-217.89, 321.72) * mm, "end": v(-217.89, 319.18) * mm});
            skLineSegment(sketch, "E8.6.1.2", {"start": v(-217.89, 321.72) * mm, "end": v(-215.35, 321.72) * mm});
            skLineSegment(sketch, "E8.9.1.2", {"start": v(-215.35, 321.72) * mm, "end": v(-215.35, 319.18) * mm});
            skLineSegment(sketch, "E8.0.1.3", {"start": v(-217.89, 316.34) * mm, "end": v(-215.35, 316.34) * mm});
            skLineSegment(sketch, "E8.3.1.3", {"start": v(-217.89, 318.88) * mm, "end": v(-217.89, 316.34) * mm});
            skLineSegment(sketch, "E8.6.1.3", {"start": v(-217.89, 318.88) * mm, "end": v(-215.35, 318.88) * mm});
            skLineSegment(sketch, "E8.9.1.3", {"start": v(-215.35, 318.88) * mm, "end": v(-215.35, 316.34) * mm});
            skLineSegment(sketch, "E8.0.1.4", {"start": v(-217.89, 313.5) * mm, "end": v(-215.35, 313.5) * mm});
            skLineSegment(sketch, "E8.3.1.4", {"start": v(-217.89, 316.03) * mm, "end": v(-217.89, 313.5) * mm});
            skLineSegment(sketch, "E8.6.1.4", {"start": v(-217.89, 316.03) * mm, "end": v(-215.35, 316.03) * mm});
            skLineSegment(sketch, "E8.9.1.4", {"start": v(-215.35, 316.03) * mm, "end": v(-215.35, 313.5) * mm});
            skLineSegment(sketch, "E8.0.1.5", {"start": v(-217.89, 310.65) * mm, "end": v(-215.35, 310.65) * mm});
            skLineSegment(sketch, "E8.3.1.5", {"start": v(-217.89, 313.19) * mm, "end": v(-217.89, 310.65) * mm});
            skLineSegment(sketch, "E8.6.1.5", {"start": v(-217.89, 313.19) * mm, "end": v(-215.35, 313.19) * mm});
            skLineSegment(sketch, "E8.9.1.5", {"start": v(-215.35, 313.19) * mm, "end": v(-215.35, 310.65) * mm});
            skLineSegment(sketch, "E8.0.1.6", {"start": v(-217.89, 307.8) * mm, "end": v(-215.35, 307.8) * mm});
            skLineSegment(sketch, "E8.3.1.6", {"start": v(-217.89, 310.34) * mm, "end": v(-217.89, 307.8) * mm});
            skLineSegment(sketch, "E8.6.1.6", {"start": v(-217.89, 310.34) * mm, "end": v(-215.35, 310.34) * mm});
            skLineSegment(sketch, "E8.9.1.6", {"start": v(-215.35, 310.34) * mm, "end": v(-215.35, 307.8) * mm});
            skLineSegment(sketch, "E8.0.1.7", {"start": v(-217.89, 304.96) * mm, "end": v(-215.35, 304.96) * mm});
            skLineSegment(sketch, "E8.3.1.7", {"start": v(-217.89, 307.5) * mm, "end": v(-217.89, 304.96) * mm});
            skLineSegment(sketch, "E8.6.1.7", {"start": v(-217.89, 307.5) * mm, "end": v(-215.35, 307.5) * mm});
            skLineSegment(sketch, "E8.9.1.7", {"start": v(-215.35, 307.5) * mm, "end": v(-215.35, 304.96) * mm});
            skLineSegment(sketch, "E8.0.1.8", {"start": v(-217.89, 302.11) * mm, "end": v(-215.35, 302.11) * mm});
            skLineSegment(sketch, "E8.3.1.8", {"start": v(-217.89, 304.65) * mm, "end": v(-217.89, 302.11) * mm});
            skLineSegment(sketch, "E8.6.1.8", {"start": v(-217.89, 304.65) * mm, "end": v(-215.35, 304.65) * mm});
            skLineSegment(sketch, "E8.9.1.8", {"start": v(-215.35, 304.65) * mm, "end": v(-215.35, 302.11) * mm});
            skLineSegment(sketch, "E8.0.1.9", {"start": v(-217.89, 299.27) * mm, "end": v(-215.35, 299.27) * mm});
            skLineSegment(sketch, "E8.3.1.9", {"start": v(-217.89, 301.8) * mm, "end": v(-217.89, 299.27) * mm});
            skLineSegment(sketch, "E8.6.1.9", {"start": v(-217.89, 301.8) * mm, "end": v(-215.35, 301.8) * mm});
            skLineSegment(sketch, "E8.9.1.9", {"start": v(-215.35, 301.8) * mm, "end": v(-215.35, 299.27) * mm});
            skLineSegment(sketch, "E8.0.1.10", {"start": v(-217.89, 296.42) * mm, "end": v(-215.35, 296.42) * mm});
            skLineSegment(sketch, "E8.3.1.10", {"start": v(-217.89, 298.96) * mm, "end": v(-217.89, 296.42) * mm});
            skLineSegment(sketch, "E8.6.1.10", {"start": v(-217.89, 298.96) * mm, "end": v(-215.35, 298.96) * mm});
            skLineSegment(sketch, "E8.9.1.10", {"start": v(-215.35, 298.96) * mm, "end": v(-215.35, 296.42) * mm});
            skLineSegment(sketch, "E8.0.1.11", {"start": v(-217.89, 293.58) * mm, "end": v(-215.35, 293.58) * mm});
            skLineSegment(sketch, "E8.3.1.11", {"start": v(-217.89, 296.12) * mm, "end": v(-217.89, 293.58) * mm});
            skLineSegment(sketch, "E8.6.1.11", {"start": v(-217.89, 296.12) * mm, "end": v(-215.35, 296.12) * mm});
            skLineSegment(sketch, "E8.9.1.11", {"start": v(-215.35, 296.12) * mm, "end": v(-215.35, 293.58) * mm});
            skLineSegment(sketch, "E8.0.1.12", {"start": v(-217.89, 290.73) * mm, "end": v(-215.35, 290.73) * mm});
            skLineSegment(sketch, "E8.3.1.12", {"start": v(-217.89, 293.27) * mm, "end": v(-217.89, 290.73) * mm});
            skLineSegment(sketch, "E8.6.1.12", {"start": v(-217.89, 293.27) * mm, "end": v(-215.35, 293.27) * mm});
            skLineSegment(sketch, "E8.9.1.12", {"start": v(-215.35, 293.27) * mm, "end": v(-215.35, 290.73) * mm});
            skLineSegment(sketch, "E8.0.1.13", {"start": v(-217.89, 287.89) * mm, "end": v(-215.35, 287.89) * mm});
            skLineSegment(sketch, "E8.3.1.13", {"start": v(-217.89, 290.43) * mm, "end": v(-217.89, 287.89) * mm});
            skLineSegment(sketch, "E8.6.1.13", {"start": v(-217.89, 290.43) * mm, "end": v(-215.35, 290.43) * mm});
            skLineSegment(sketch, "E8.9.1.13", {"start": v(-215.35, 290.43) * mm, "end": v(-215.35, 287.89) * mm});
            skLineSegment(sketch, "E8.0.1.14", {"start": v(-217.89, 285.04) * mm, "end": v(-215.35, 285.04) * mm});
            skLineSegment(sketch, "E8.3.1.14", {"start": v(-217.89, 287.58) * mm, "end": v(-217.89, 285.04) * mm});
            skLineSegment(sketch, "E8.6.1.14", {"start": v(-217.89, 287.58) * mm, "end": v(-215.35, 287.58) * mm});
            skLineSegment(sketch, "E8.9.1.14", {"start": v(-215.35, 287.58) * mm, "end": v(-215.35, 285.04) * mm});
            skLineSegment(sketch, "E8.0.1.15", {"start": v(-217.89, 282.2) * mm, "end": v(-215.35, 282.2) * mm});
            skLineSegment(sketch, "E8.3.1.15", {"start": v(-217.89, 284.74) * mm, "end": v(-217.89, 282.2) * mm});
            skLineSegment(sketch, "E8.6.1.15", {"start": v(-217.89, 284.74) * mm, "end": v(-215.35, 284.74) * mm});
            skLineSegment(sketch, "E8.9.1.15", {"start": v(-215.35, 284.74) * mm, "end": v(-215.35, 282.2) * mm});
            skLineSegment(sketch, "E8.0.2.2", {"start": v(-215.04, 319.18) * mm, "end": v(-212.5, 319.18) * mm});
            skLineSegment(sketch, "E8.3.2.2", {"start": v(-215.04, 321.72) * mm, "end": v(-215.04, 319.18) * mm});
            skLineSegment(sketch, "E8.6.2.2", {"start": v(-215.04, 321.72) * mm, "end": v(-212.5, 321.72) * mm});
            skLineSegment(sketch, "E8.9.2.2", {"start": v(-212.5, 321.72) * mm, "end": v(-212.5, 319.18) * mm});
            skLineSegment(sketch, "E8.0.2.3", {"start": v(-215.04, 316.34) * mm, "end": v(-212.5, 316.34) * mm});
            skLineSegment(sketch, "E8.3.2.3", {"start": v(-215.04, 318.88) * mm, "end": v(-215.04, 316.34) * mm});
            skLineSegment(sketch, "E8.6.2.3", {"start": v(-215.04, 318.88) * mm, "end": v(-212.5, 318.88) * mm});
            skLineSegment(sketch, "E8.9.2.3", {"start": v(-212.5, 318.88) * mm, "end": v(-212.5, 316.34) * mm});
            skLineSegment(sketch, "E8.0.2.4", {"start": v(-215.04, 313.5) * mm, "end": v(-212.5, 313.5) * mm});
            skLineSegment(sketch, "E8.3.2.4", {"start": v(-215.04, 316.03) * mm, "end": v(-215.04, 313.5) * mm});
            skLineSegment(sketch, "E8.6.2.4", {"start": v(-215.04, 316.03) * mm, "end": v(-212.5, 316.03) * mm});
            skLineSegment(sketch, "E8.9.2.4", {"start": v(-212.5, 316.03) * mm, "end": v(-212.5, 313.5) * mm});
            skLineSegment(sketch, "E8.0.2.5", {"start": v(-215.04, 310.65) * mm, "end": v(-212.5, 310.65) * mm});
            skLineSegment(sketch, "E8.3.2.5", {"start": v(-215.04, 313.19) * mm, "end": v(-215.04, 310.65) * mm});
            skLineSegment(sketch, "E8.6.2.5", {"start": v(-215.04, 313.19) * mm, "end": v(-212.5, 313.19) * mm});
            skLineSegment(sketch, "E8.9.2.5", {"start": v(-212.5, 313.19) * mm, "end": v(-212.5, 310.65) * mm});
            skLineSegment(sketch, "E8.0.2.6", {"start": v(-215.04, 307.8) * mm, "end": v(-212.5, 307.8) * mm});
            skLineSegment(sketch, "E8.3.2.6", {"start": v(-215.04, 310.34) * mm, "end": v(-215.04, 307.8) * mm});
            skLineSegment(sketch, "E8.6.2.6", {"start": v(-215.04, 310.34) * mm, "end": v(-212.5, 310.34) * mm});
            skLineSegment(sketch, "E8.9.2.6", {"start": v(-212.5, 310.34) * mm, "end": v(-212.5, 307.8) * mm});
            skLineSegment(sketch, "E8.0.2.7", {"start": v(-215.04, 304.96) * mm, "end": v(-212.5, 304.96) * mm});
            skLineSegment(sketch, "E8.3.2.7", {"start": v(-215.04, 307.5) * mm, "end": v(-215.04, 304.96) * mm});
            skLineSegment(sketch, "E8.6.2.7", {"start": v(-215.04, 307.5) * mm, "end": v(-212.5, 307.5) * mm});
            skLineSegment(sketch, "E8.9.2.7", {"start": v(-212.5, 307.5) * mm, "end": v(-212.5, 304.96) * mm});
            skLineSegment(sketch, "E8.0.2.8", {"start": v(-215.04, 302.11) * mm, "end": v(-212.5, 302.11) * mm});
            skLineSegment(sketch, "E8.3.2.8", {"start": v(-215.04, 304.65) * mm, "end": v(-215.04, 302.11) * mm});
            skLineSegment(sketch, "E8.6.2.8", {"start": v(-215.04, 304.65) * mm, "end": v(-212.5, 304.65) * mm});
            skLineSegment(sketch, "E8.9.2.8", {"start": v(-212.5, 304.65) * mm, "end": v(-212.5, 302.11) * mm});
            skLineSegment(sketch, "E8.0.2.9", {"start": v(-215.04, 299.27) * mm, "end": v(-212.5, 299.27) * mm});
            skLineSegment(sketch, "E8.3.2.9", {"start": v(-215.04, 301.8) * mm, "end": v(-215.04, 299.27) * mm});
            skLineSegment(sketch, "E8.6.2.9", {"start": v(-215.04, 301.8) * mm, "end": v(-212.5, 301.8) * mm});
            skLineSegment(sketch, "E8.9.2.9", {"start": v(-212.5, 301.8) * mm, "end": v(-212.5, 299.27) * mm});
            skLineSegment(sketch, "E8.0.2.10", {"start": v(-215.04, 296.42) * mm, "end": v(-212.5, 296.42) * mm});
            skLineSegment(sketch, "E8.3.2.10", {"start": v(-215.04, 298.96) * mm, "end": v(-215.04, 296.42) * mm});
            skLineSegment(sketch, "E8.6.2.10", {"start": v(-215.04, 298.96) * mm, "end": v(-212.5, 298.96) * mm});
            skLineSegment(sketch, "E8.9.2.10", {"start": v(-212.5, 298.96) * mm, "end": v(-212.5, 296.42) * mm});
            skLineSegment(sketch, "E8.0.2.11", {"start": v(-215.04, 293.58) * mm, "end": v(-212.5, 293.58) * mm});
            skLineSegment(sketch, "E8.3.2.11", {"start": v(-215.04, 296.12) * mm, "end": v(-215.04, 293.58) * mm});
            skLineSegment(sketch, "E8.6.2.11", {"start": v(-215.04, 296.12) * mm, "end": v(-212.5, 296.12) * mm});
            skLineSegment(sketch, "E8.9.2.11", {"start": v(-212.5, 296.12) * mm, "end": v(-212.5, 293.58) * mm});
            skLineSegment(sketch, "E8.0.2.12", {"start": v(-215.04, 290.73) * mm, "end": v(-212.5, 290.73) * mm});
            skLineSegment(sketch, "E8.3.2.12", {"start": v(-215.04, 293.27) * mm, "end": v(-215.04, 290.73) * mm});
            skLineSegment(sketch, "E8.6.2.12", {"start": v(-215.04, 293.27) * mm, "end": v(-212.5, 293.27) * mm});
            skLineSegment(sketch, "E8.9.2.12", {"start": v(-212.5, 293.27) * mm, "end": v(-212.5, 290.73) * mm});
            skLineSegment(sketch, "E8.0.2.13", {"start": v(-215.04, 287.89) * mm, "end": v(-212.5, 287.89) * mm});
            skLineSegment(sketch, "E8.3.2.13", {"start": v(-215.04, 290.43) * mm, "end": v(-215.04, 287.89) * mm});
            skLineSegment(sketch, "E8.6.2.13", {"start": v(-215.04, 290.43) * mm, "end": v(-212.5, 290.43) * mm});
            skLineSegment(sketch, "E8.9.2.13", {"start": v(-212.5, 290.43) * mm, "end": v(-212.5, 287.89) * mm});
            skLineSegment(sketch, "E8.0.2.14", {"start": v(-215.04, 285.04) * mm, "end": v(-212.5, 285.04) * mm});
            skLineSegment(sketch, "E8.3.2.14", {"start": v(-215.04, 287.58) * mm, "end": v(-215.04, 285.04) * mm});
            skLineSegment(sketch, "E8.6.2.14", {"start": v(-215.04, 287.58) * mm, "end": v(-212.5, 287.58) * mm});
            skLineSegment(sketch, "E8.9.2.14", {"start": v(-212.5, 287.58) * mm, "end": v(-212.5, 285.04) * mm});
            skLineSegment(sketch, "E8.0.2.15", {"start": v(-215.04, 282.2) * mm, "end": v(-212.5, 282.2) * mm});
            skLineSegment(sketch, "E8.3.2.15", {"start": v(-215.04, 284.74) * mm, "end": v(-215.04, 282.2) * mm});
            skLineSegment(sketch, "E8.6.2.15", {"start": v(-215.04, 284.74) * mm, "end": v(-212.5, 284.74) * mm});
            skLineSegment(sketch, "E8.9.2.15", {"start": v(-212.5, 284.74) * mm, "end": v(-212.5, 282.2) * mm});
            skLineSegment(sketch, "E8.0.3.2", {"start": v(-212.2, 319.18) * mm, "end": v(-209.66, 319.18) * mm});
            skLineSegment(sketch, "E8.3.3.2", {"start": v(-212.2, 321.72) * mm, "end": v(-212.2, 319.18) * mm});
            skLineSegment(sketch, "E8.6.3.2", {"start": v(-212.2, 321.72) * mm, "end": v(-209.66, 321.72) * mm});
            skLineSegment(sketch, "E8.9.3.2", {"start": v(-209.66, 321.72) * mm, "end": v(-209.66, 319.18) * mm});
            skLineSegment(sketch, "E8.0.3.3", {"start": v(-212.2, 316.34) * mm, "end": v(-209.66, 316.34) * mm});
            skLineSegment(sketch, "E8.3.3.3", {"start": v(-212.2, 318.88) * mm, "end": v(-212.2, 316.34) * mm});
            skLineSegment(sketch, "E8.6.3.3", {"start": v(-212.2, 318.88) * mm, "end": v(-209.66, 318.88) * mm});
            skLineSegment(sketch, "E8.9.3.3", {"start": v(-209.66, 318.88) * mm, "end": v(-209.66, 316.34) * mm});
            skLineSegment(sketch, "E8.0.3.4", {"start": v(-212.2, 313.5) * mm, "end": v(-209.66, 313.5) * mm});
            skLineSegment(sketch, "E8.3.3.4", {"start": v(-212.2, 316.03) * mm, "end": v(-212.2, 313.5) * mm});
            skLineSegment(sketch, "E8.6.3.4", {"start": v(-212.2, 316.03) * mm, "end": v(-209.66, 316.03) * mm});
            skLineSegment(sketch, "E8.9.3.4", {"start": v(-209.66, 316.03) * mm, "end": v(-209.66, 313.5) * mm});
            skLineSegment(sketch, "E8.0.3.5", {"start": v(-212.2, 310.65) * mm, "end": v(-209.66, 310.65) * mm});
            skLineSegment(sketch, "E8.3.3.5", {"start": v(-212.2, 313.19) * mm, "end": v(-212.2, 310.65) * mm});
            skLineSegment(sketch, "E8.6.3.5", {"start": v(-212.2, 313.19) * mm, "end": v(-209.66, 313.19) * mm});
            skLineSegment(sketch, "E8.9.3.5", {"start": v(-209.66, 313.19) * mm, "end": v(-209.66, 310.65) * mm});
            skLineSegment(sketch, "E8.0.3.6", {"start": v(-212.2, 307.8) * mm, "end": v(-209.66, 307.8) * mm});
            skLineSegment(sketch, "E8.3.3.6", {"start": v(-212.2, 310.34) * mm, "end": v(-212.2, 307.8) * mm});
            skLineSegment(sketch, "E8.6.3.6", {"start": v(-212.2, 310.34) * mm, "end": v(-209.66, 310.34) * mm});
            skLineSegment(sketch, "E8.9.3.6", {"start": v(-209.66, 310.34) * mm, "end": v(-209.66, 307.8) * mm});
            skLineSegment(sketch, "E8.0.3.7", {"start": v(-212.2, 304.96) * mm, "end": v(-209.66, 304.96) * mm});
            skLineSegment(sketch, "E8.3.3.7", {"start": v(-212.2, 307.5) * mm, "end": v(-212.2, 304.96) * mm});
            skLineSegment(sketch, "E8.6.3.7", {"start": v(-212.2, 307.5) * mm, "end": v(-209.66, 307.5) * mm});
            skLineSegment(sketch, "E8.9.3.7", {"start": v(-209.66, 307.5) * mm, "end": v(-209.66, 304.96) * mm});
            skLineSegment(sketch, "E8.0.3.8", {"start": v(-212.2, 302.11) * mm, "end": v(-209.66, 302.11) * mm});
            skLineSegment(sketch, "E8.3.3.8", {"start": v(-212.2, 304.65) * mm, "end": v(-212.2, 302.11) * mm});
            skLineSegment(sketch, "E8.6.3.8", {"start": v(-212.2, 304.65) * mm, "end": v(-209.66, 304.65) * mm});
            skLineSegment(sketch, "E8.9.3.8", {"start": v(-209.66, 304.65) * mm, "end": v(-209.66, 302.11) * mm});
            skLineSegment(sketch, "E8.0.3.9", {"start": v(-212.2, 299.27) * mm, "end": v(-209.66, 299.27) * mm});
            skLineSegment(sketch, "E8.3.3.9", {"start": v(-212.2, 301.8) * mm, "end": v(-212.2, 299.27) * mm});
            skLineSegment(sketch, "E8.6.3.9", {"start": v(-212.2, 301.8) * mm, "end": v(-209.66, 301.8) * mm});
            skLineSegment(sketch, "E8.9.3.9", {"start": v(-209.66, 301.8) * mm, "end": v(-209.66, 299.27) * mm});
            skLineSegment(sketch, "E8.0.3.10", {"start": v(-212.2, 296.42) * mm, "end": v(-209.66, 296.42) * mm});
            skLineSegment(sketch, "E8.3.3.10", {"start": v(-212.2, 298.96) * mm, "end": v(-212.2, 296.42) * mm});
            skLineSegment(sketch, "E8.6.3.10", {"start": v(-212.2, 298.96) * mm, "end": v(-209.66, 298.96) * mm});
            skLineSegment(sketch, "E8.9.3.10", {"start": v(-209.66, 298.96) * mm, "end": v(-209.66, 296.42) * mm});
            skLineSegment(sketch, "E8.0.3.11", {"start": v(-212.2, 293.58) * mm, "end": v(-209.66, 293.58) * mm});
            skLineSegment(sketch, "E8.3.3.11", {"start": v(-212.2, 296.12) * mm, "end": v(-212.2, 293.58) * mm});
            skLineSegment(sketch, "E8.6.3.11", {"start": v(-212.2, 296.12) * mm, "end": v(-209.66, 296.12) * mm});
            skLineSegment(sketch, "E8.9.3.11", {"start": v(-209.66, 296.12) * mm, "end": v(-209.66, 293.58) * mm});
            skLineSegment(sketch, "E8.0.3.12", {"start": v(-212.2, 290.73) * mm, "end": v(-209.66, 290.73) * mm});
            skLineSegment(sketch, "E8.3.3.12", {"start": v(-212.2, 293.27) * mm, "end": v(-212.2, 290.73) * mm});
            skLineSegment(sketch, "E8.6.3.12", {"start": v(-212.2, 293.27) * mm, "end": v(-209.66, 293.27) * mm});
            skLineSegment(sketch, "E8.9.3.12", {"start": v(-209.66, 293.27) * mm, "end": v(-209.66, 290.73) * mm});
            skLineSegment(sketch, "E8.0.3.13", {"start": v(-212.2, 287.89) * mm, "end": v(-209.66, 287.89) * mm});
            skLineSegment(sketch, "E8.3.3.13", {"start": v(-212.2, 290.43) * mm, "end": v(-212.2, 287.89) * mm});
            skLineSegment(sketch, "E8.6.3.13", {"start": v(-212.2, 290.43) * mm, "end": v(-209.66, 290.43) * mm});
            skLineSegment(sketch, "E8.9.3.13", {"start": v(-209.66, 290.43) * mm, "end": v(-209.66, 287.89) * mm});
            skLineSegment(sketch, "E8.0.3.14", {"start": v(-212.2, 285.04) * mm, "end": v(-209.66, 285.04) * mm});
            skLineSegment(sketch, "E8.3.3.14", {"start": v(-212.2, 287.58) * mm, "end": v(-212.2, 285.04) * mm});
            skLineSegment(sketch, "E8.6.3.14", {"start": v(-212.2, 287.58) * mm, "end": v(-209.66, 287.58) * mm});
            skLineSegment(sketch, "E8.9.3.14", {"start": v(-209.66, 287.58) * mm, "end": v(-209.66, 285.04) * mm});
            skLineSegment(sketch, "E8.0.3.15", {"start": v(-212.2, 282.2) * mm, "end": v(-209.66, 282.2) * mm});
            skLineSegment(sketch, "E8.3.3.15", {"start": v(-212.2, 284.74) * mm, "end": v(-212.2, 282.2) * mm});
            skLineSegment(sketch, "E8.6.3.15", {"start": v(-212.2, 284.74) * mm, "end": v(-209.66, 284.74) * mm});
            skLineSegment(sketch, "E8.9.3.15", {"start": v(-209.66, 284.74) * mm, "end": v(-209.66, 282.2) * mm});
            skLineSegment(sketch, "E8.0.4.2", {"start": v(-209.35, 319.18) * mm, "end": v(-206.81, 319.18) * mm});
            skLineSegment(sketch, "E8.3.4.2", {"start": v(-209.35, 321.72) * mm, "end": v(-209.35, 319.18) * mm});
            skLineSegment(sketch, "E8.6.4.2", {"start": v(-209.35, 321.72) * mm, "end": v(-206.81, 321.72) * mm});
            skLineSegment(sketch, "E8.9.4.2", {"start": v(-206.81, 321.72) * mm, "end": v(-206.81, 319.18) * mm});
            skLineSegment(sketch, "E8.0.4.3", {"start": v(-209.35, 316.34) * mm, "end": v(-206.81, 316.34) * mm});
            skLineSegment(sketch, "E8.3.4.3", {"start": v(-209.35, 318.88) * mm, "end": v(-209.35, 316.34) * mm});
            skLineSegment(sketch, "E8.6.4.3", {"start": v(-209.35, 318.88) * mm, "end": v(-206.81, 318.88) * mm});
            skLineSegment(sketch, "E8.9.4.3", {"start": v(-206.81, 318.88) * mm, "end": v(-206.81, 316.34) * mm});
            skLineSegment(sketch, "E8.0.4.4", {"start": v(-209.35, 313.5) * mm, "end": v(-206.81, 313.5) * mm});
            skLineSegment(sketch, "E8.3.4.4", {"start": v(-209.35, 316.03) * mm, "end": v(-209.35, 313.5) * mm});
            skLineSegment(sketch, "E8.6.4.4", {"start": v(-209.35, 316.03) * mm, "end": v(-206.81, 316.03) * mm});
            skLineSegment(sketch, "E8.9.4.4", {"start": v(-206.81, 316.03) * mm, "end": v(-206.81, 313.5) * mm});
            skLineSegment(sketch, "E8.0.4.5", {"start": v(-209.35, 310.65) * mm, "end": v(-206.81, 310.65) * mm});
            skLineSegment(sketch, "E8.3.4.5", {"start": v(-209.35, 313.19) * mm, "end": v(-209.35, 310.65) * mm});
            skLineSegment(sketch, "E8.6.4.5", {"start": v(-209.35, 313.19) * mm, "end": v(-206.81, 313.19) * mm});
            skLineSegment(sketch, "E8.9.4.5", {"start": v(-206.81, 313.19) * mm, "end": v(-206.81, 310.65) * mm});
            skLineSegment(sketch, "E8.0.4.6", {"start": v(-209.35, 307.8) * mm, "end": v(-206.81, 307.8) * mm});
            skLineSegment(sketch, "E8.3.4.6", {"start": v(-209.35, 310.34) * mm, "end": v(-209.35, 307.8) * mm});
            skLineSegment(sketch, "E8.6.4.6", {"start": v(-209.35, 310.34) * mm, "end": v(-206.81, 310.34) * mm});
            skLineSegment(sketch, "E8.9.4.6", {"start": v(-206.81, 310.34) * mm, "end": v(-206.81, 307.8) * mm});
            skLineSegment(sketch, "E8.0.4.7", {"start": v(-209.35, 304.96) * mm, "end": v(-206.81, 304.96) * mm});
            skLineSegment(sketch, "E8.3.4.7", {"start": v(-209.35, 307.5) * mm, "end": v(-209.35, 304.96) * mm});
            skLineSegment(sketch, "E8.6.4.7", {"start": v(-209.35, 307.5) * mm, "end": v(-206.81, 307.5) * mm});
            skLineSegment(sketch, "E8.9.4.7", {"start": v(-206.81, 307.5) * mm, "end": v(-206.81, 304.96) * mm});
            skLineSegment(sketch, "E8.0.4.8", {"start": v(-209.35, 302.11) * mm, "end": v(-206.81, 302.11) * mm});
            skLineSegment(sketch, "E8.3.4.8", {"start": v(-209.35, 304.65) * mm, "end": v(-209.35, 302.11) * mm});
            skLineSegment(sketch, "E8.6.4.8", {"start": v(-209.35, 304.65) * mm, "end": v(-206.81, 304.65) * mm});
            skLineSegment(sketch, "E8.9.4.8", {"start": v(-206.81, 304.65) * mm, "end": v(-206.81, 302.11) * mm});
            skLineSegment(sketch, "E8.0.4.9", {"start": v(-209.35, 299.27) * mm, "end": v(-206.81, 299.27) * mm});
            skLineSegment(sketch, "E8.3.4.9", {"start": v(-209.35, 301.8) * mm, "end": v(-209.35, 299.27) * mm});
            skLineSegment(sketch, "E8.6.4.9", {"start": v(-209.35, 301.8) * mm, "end": v(-206.81, 301.8) * mm});
            skLineSegment(sketch, "E8.9.4.9", {"start": v(-206.81, 301.8) * mm, "end": v(-206.81, 299.27) * mm});
            skLineSegment(sketch, "E8.0.4.10", {"start": v(-209.35, 296.42) * mm, "end": v(-206.81, 296.42) * mm});
            skLineSegment(sketch, "E8.3.4.10", {"start": v(-209.35, 298.96) * mm, "end": v(-209.35, 296.42) * mm});
            skLineSegment(sketch, "E8.6.4.10", {"start": v(-209.35, 298.96) * mm, "end": v(-206.81, 298.96) * mm});
            skLineSegment(sketch, "E8.9.4.10", {"start": v(-206.81, 298.96) * mm, "end": v(-206.81, 296.42) * mm});
            skLineSegment(sketch, "E8.0.4.11", {"start": v(-209.35, 293.58) * mm, "end": v(-206.81, 293.58) * mm});
            skLineSegment(sketch, "E8.3.4.11", {"start": v(-209.35, 296.12) * mm, "end": v(-209.35, 293.58) * mm});
            skLineSegment(sketch, "E8.6.4.11", {"start": v(-209.35, 296.12) * mm, "end": v(-206.81, 296.12) * mm});
            skLineSegment(sketch, "E8.9.4.11", {"start": v(-206.81, 296.12) * mm, "end": v(-206.81, 293.58) * mm});
            skLineSegment(sketch, "E8.0.4.12", {"start": v(-209.35, 290.73) * mm, "end": v(-206.81, 290.73) * mm});
            skLineSegment(sketch, "E8.3.4.12", {"start": v(-209.35, 293.27) * mm, "end": v(-209.35, 290.73) * mm});
            skLineSegment(sketch, "E8.6.4.12", {"start": v(-209.35, 293.27) * mm, "end": v(-206.81, 293.27) * mm});
            skLineSegment(sketch, "E8.9.4.12", {"start": v(-206.81, 293.27) * mm, "end": v(-206.81, 290.73) * mm});
            skLineSegment(sketch, "E8.0.4.13", {"start": v(-209.35, 287.89) * mm, "end": v(-206.81, 287.89) * mm});
            skLineSegment(sketch, "E8.3.4.13", {"start": v(-209.35, 290.43) * mm, "end": v(-209.35, 287.89) * mm});
            skLineSegment(sketch, "E8.6.4.13", {"start": v(-209.35, 290.43) * mm, "end": v(-206.81, 290.43) * mm});
            skLineSegment(sketch, "E8.9.4.13", {"start": v(-206.81, 290.43) * mm, "end": v(-206.81, 287.89) * mm});
            skLineSegment(sketch, "E8.0.4.14", {"start": v(-209.35, 285.04) * mm, "end": v(-206.81, 285.04) * mm});
            skLineSegment(sketch, "E8.3.4.14", {"start": v(-209.35, 287.58) * mm, "end": v(-209.35, 285.04) * mm});
            skLineSegment(sketch, "E8.6.4.14", {"start": v(-209.35, 287.58) * mm, "end": v(-206.81, 287.58) * mm});
            skLineSegment(sketch, "E8.9.4.14", {"start": v(-206.81, 287.58) * mm, "end": v(-206.81, 285.04) * mm});
            skLineSegment(sketch, "E8.0.4.15", {"start": v(-209.35, 282.2) * mm, "end": v(-206.81, 282.2) * mm});
            skLineSegment(sketch, "E8.3.4.15", {"start": v(-209.35, 284.74) * mm, "end": v(-209.35, 282.2) * mm});
            skLineSegment(sketch, "E8.6.4.15", {"start": v(-209.35, 284.74) * mm, "end": v(-206.81, 284.74) * mm});
            skLineSegment(sketch, "E8.9.4.15", {"start": v(-206.81, 284.74) * mm, "end": v(-206.81, 282.2) * mm});
            skLineSegment(sketch, "E8.0.5.2", {"start": v(-206.5, 319.18) * mm, "end": v(-203.97, 319.18) * mm});
            skLineSegment(sketch, "E8.3.5.2", {"start": v(-206.5, 321.72) * mm, "end": v(-206.5, 319.18) * mm});
            skLineSegment(sketch, "E8.6.5.2", {"start": v(-206.5, 321.72) * mm, "end": v(-203.97, 321.72) * mm});
            skLineSegment(sketch, "E8.9.5.2", {"start": v(-203.97, 321.72) * mm, "end": v(-203.97, 319.18) * mm});
            skLineSegment(sketch, "E8.0.5.3", {"start": v(-206.5, 316.34) * mm, "end": v(-203.97, 316.34) * mm});
            skLineSegment(sketch, "E8.3.5.3", {"start": v(-206.5, 318.88) * mm, "end": v(-206.5, 316.34) * mm});
            skLineSegment(sketch, "E8.6.5.3", {"start": v(-206.5, 318.88) * mm, "end": v(-203.97, 318.88) * mm});
            skLineSegment(sketch, "E8.9.5.3", {"start": v(-203.97, 318.88) * mm, "end": v(-203.97, 316.34) * mm});
            skLineSegment(sketch, "E8.0.5.4", {"start": v(-206.5, 313.5) * mm, "end": v(-203.97, 313.5) * mm});
            skLineSegment(sketch, "E8.3.5.4", {"start": v(-206.5, 316.03) * mm, "end": v(-206.5, 313.5) * mm});
            skLineSegment(sketch, "E8.6.5.4", {"start": v(-206.5, 316.03) * mm, "end": v(-203.97, 316.03) * mm});
            skLineSegment(sketch, "E8.9.5.4", {"start": v(-203.97, 316.03) * mm, "end": v(-203.97, 313.5) * mm});
            skLineSegment(sketch, "E8.0.5.5", {"start": v(-206.5, 310.65) * mm, "end": v(-203.97, 310.65) * mm});
            skLineSegment(sketch, "E8.3.5.5", {"start": v(-206.5, 313.19) * mm, "end": v(-206.5, 310.65) * mm});
            skLineSegment(sketch, "E8.6.5.5", {"start": v(-206.5, 313.19) * mm, "end": v(-203.97, 313.19) * mm});
            skLineSegment(sketch, "E8.9.5.5", {"start": v(-203.97, 313.19) * mm, "end": v(-203.97, 310.65) * mm});
            skLineSegment(sketch, "E8.0.5.6", {"start": v(-206.5, 307.8) * mm, "end": v(-203.97, 307.8) * mm});
            skLineSegment(sketch, "E8.3.5.6", {"start": v(-206.5, 310.34) * mm, "end": v(-206.5, 307.8) * mm});
            skLineSegment(sketch, "E8.6.5.6", {"start": v(-206.5, 310.34) * mm, "end": v(-203.97, 310.34) * mm});
            skLineSegment(sketch, "E8.9.5.6", {"start": v(-203.97, 310.34) * mm, "end": v(-203.97, 307.8) * mm});
            skLineSegment(sketch, "E8.0.5.7", {"start": v(-206.5, 304.96) * mm, "end": v(-203.97, 304.96) * mm});
            skLineSegment(sketch, "E8.3.5.7", {"start": v(-206.5, 307.5) * mm, "end": v(-206.5, 304.96) * mm});
            skLineSegment(sketch, "E8.6.5.7", {"start": v(-206.5, 307.5) * mm, "end": v(-203.97, 307.5) * mm});
            skLineSegment(sketch, "E8.9.5.7", {"start": v(-203.97, 307.5) * mm, "end": v(-203.97, 304.96) * mm});
            skLineSegment(sketch, "E8.0.5.8", {"start": v(-206.5, 302.11) * mm, "end": v(-203.97, 302.11) * mm});
            skLineSegment(sketch, "E8.3.5.8", {"start": v(-206.5, 304.65) * mm, "end": v(-206.5, 302.11) * mm});
            skLineSegment(sketch, "E8.6.5.8", {"start": v(-206.5, 304.65) * mm, "end": v(-203.97, 304.65) * mm});
            skLineSegment(sketch, "E8.9.5.8", {"start": v(-203.97, 304.65) * mm, "end": v(-203.97, 302.11) * mm});
            skLineSegment(sketch, "E8.0.5.9", {"start": v(-206.5, 299.27) * mm, "end": v(-203.97, 299.27) * mm});
            skLineSegment(sketch, "E8.3.5.9", {"start": v(-206.5, 301.8) * mm, "end": v(-206.5, 299.27) * mm});
            skLineSegment(sketch, "E8.6.5.9", {"start": v(-206.5, 301.8) * mm, "end": v(-203.97, 301.8) * mm});
            skLineSegment(sketch, "E8.9.5.9", {"start": v(-203.97, 301.8) * mm, "end": v(-203.97, 299.27) * mm});
            skLineSegment(sketch, "E8.0.5.10", {"start": v(-206.5, 296.42) * mm, "end": v(-203.97, 296.42) * mm});
            skLineSegment(sketch, "E8.3.5.10", {"start": v(-206.5, 298.96) * mm, "end": v(-206.5, 296.42) * mm});
            skLineSegment(sketch, "E8.6.5.10", {"start": v(-206.5, 298.96) * mm, "end": v(-203.97, 298.96) * mm});
            skLineSegment(sketch, "E8.9.5.10", {"start": v(-203.97, 298.96) * mm, "end": v(-203.97, 296.42) * mm});
            skLineSegment(sketch, "E8.0.5.11", {"start": v(-206.5, 293.58) * mm, "end": v(-203.97, 293.58) * mm});
            skLineSegment(sketch, "E8.3.5.11", {"start": v(-206.5, 296.12) * mm, "end": v(-206.5, 293.58) * mm});
            skLineSegment(sketch, "E8.6.5.11", {"start": v(-206.5, 296.12) * mm, "end": v(-203.97, 296.12) * mm});
            skLineSegment(sketch, "E8.9.5.11", {"start": v(-203.97, 296.12) * mm, "end": v(-203.97, 293.58) * mm});
            skLineSegment(sketch, "E8.0.5.12", {"start": v(-206.5, 290.73) * mm, "end": v(-203.97, 290.73) * mm});
            skLineSegment(sketch, "E8.3.5.12", {"start": v(-206.5, 293.27) * mm, "end": v(-206.5, 290.73) * mm});
            skLineSegment(sketch, "E8.6.5.12", {"start": v(-206.5, 293.27) * mm, "end": v(-203.97, 293.27) * mm});
            skLineSegment(sketch, "E8.9.5.12", {"start": v(-203.97, 293.27) * mm, "end": v(-203.97, 290.73) * mm});
            skLineSegment(sketch, "E8.0.5.13", {"start": v(-206.5, 287.89) * mm, "end": v(-203.97, 287.89) * mm});
            skLineSegment(sketch, "E8.3.5.13", {"start": v(-206.5, 290.43) * mm, "end": v(-206.5, 287.89) * mm});
            skLineSegment(sketch, "E8.6.5.13", {"start": v(-206.5, 290.43) * mm, "end": v(-203.97, 290.43) * mm});
            skLineSegment(sketch, "E8.9.5.13", {"start": v(-203.97, 290.43) * mm, "end": v(-203.97, 287.89) * mm});
            skLineSegment(sketch, "E8.0.5.14", {"start": v(-206.5, 285.04) * mm, "end": v(-203.97, 285.04) * mm});
            skLineSegment(sketch, "E8.3.5.14", {"start": v(-206.5, 287.58) * mm, "end": v(-206.5, 285.04) * mm});
            skLineSegment(sketch, "E8.6.5.14", {"start": v(-206.5, 287.58) * mm, "end": v(-203.97, 287.58) * mm});
            skLineSegment(sketch, "E8.9.5.14", {"start": v(-203.97, 287.58) * mm, "end": v(-203.97, 285.04) * mm});
            skLineSegment(sketch, "E8.0.5.15", {"start": v(-206.5, 282.2) * mm, "end": v(-203.97, 282.2) * mm});
            skLineSegment(sketch, "E8.3.5.15", {"start": v(-206.5, 284.74) * mm, "end": v(-206.5, 282.2) * mm});
            skLineSegment(sketch, "E8.6.5.15", {"start": v(-206.5, 284.74) * mm, "end": v(-203.97, 284.74) * mm});
            skLineSegment(sketch, "E8.9.5.15", {"start": v(-203.97, 284.74) * mm, "end": v(-203.97, 282.2) * mm});
            skLineSegment(sketch, "E8.0.6.2", {"start": v(-203.66, 319.18) * mm, "end": v(-201.12, 319.18) * mm});
            skLineSegment(sketch, "E8.3.6.2", {"start": v(-203.66, 321.72) * mm, "end": v(-203.66, 319.18) * mm});
            skLineSegment(sketch, "E8.6.6.2", {"start": v(-203.66, 321.72) * mm, "end": v(-201.12, 321.72) * mm});
            skLineSegment(sketch, "E8.9.6.2", {"start": v(-201.12, 321.72) * mm, "end": v(-201.12, 319.18) * mm});
            skLineSegment(sketch, "E8.0.6.3", {"start": v(-203.66, 316.34) * mm, "end": v(-201.12, 316.34) * mm});
            skLineSegment(sketch, "E8.3.6.3", {"start": v(-203.66, 318.88) * mm, "end": v(-203.66, 316.34) * mm});
            skLineSegment(sketch, "E8.6.6.3", {"start": v(-203.66, 318.88) * mm, "end": v(-201.12, 318.88) * mm});
            skLineSegment(sketch, "E8.9.6.3", {"start": v(-201.12, 318.88) * mm, "end": v(-201.12, 316.34) * mm});
            skLineSegment(sketch, "E8.0.6.4", {"start": v(-203.66, 313.5) * mm, "end": v(-201.12, 313.5) * mm});
            skLineSegment(sketch, "E8.3.6.4", {"start": v(-203.66, 316.03) * mm, "end": v(-203.66, 313.5) * mm});
            skLineSegment(sketch, "E8.6.6.4", {"start": v(-203.66, 316.03) * mm, "end": v(-201.12, 316.03) * mm});
            skLineSegment(sketch, "E8.9.6.4", {"start": v(-201.12, 316.03) * mm, "end": v(-201.12, 313.5) * mm});
            skLineSegment(sketch, "E8.0.6.5", {"start": v(-203.66, 310.65) * mm, "end": v(-201.12, 310.65) * mm});
            skLineSegment(sketch, "E8.3.6.5", {"start": v(-203.66, 313.19) * mm, "end": v(-203.66, 310.65) * mm});
            skLineSegment(sketch, "E8.6.6.5", {"start": v(-203.66, 313.19) * mm, "end": v(-201.12, 313.19) * mm});
            skLineSegment(sketch, "E8.9.6.5", {"start": v(-201.12, 313.19) * mm, "end": v(-201.12, 310.65) * mm});
            skLineSegment(sketch, "E8.0.6.6", {"start": v(-203.66, 307.8) * mm, "end": v(-201.12, 307.8) * mm});
            skLineSegment(sketch, "E8.3.6.6", {"start": v(-203.66, 310.34) * mm, "end": v(-203.66, 307.8) * mm});
            skLineSegment(sketch, "E8.6.6.6", {"start": v(-203.66, 310.34) * mm, "end": v(-201.12, 310.34) * mm});
            skLineSegment(sketch, "E8.9.6.6", {"start": v(-201.12, 310.34) * mm, "end": v(-201.12, 307.8) * mm});
            skLineSegment(sketch, "E8.0.6.7", {"start": v(-203.66, 304.96) * mm, "end": v(-201.12, 304.96) * mm});
            skLineSegment(sketch, "E8.3.6.7", {"start": v(-203.66, 307.5) * mm, "end": v(-203.66, 304.96) * mm});
            skLineSegment(sketch, "E8.6.6.7", {"start": v(-203.66, 307.5) * mm, "end": v(-201.12, 307.5) * mm});
            skLineSegment(sketch, "E8.9.6.7", {"start": v(-201.12, 307.5) * mm, "end": v(-201.12, 304.96) * mm});
            skLineSegment(sketch, "E8.0.6.8", {"start": v(-203.66, 302.11) * mm, "end": v(-201.12, 302.11) * mm});
            skLineSegment(sketch, "E8.3.6.8", {"start": v(-203.66, 304.65) * mm, "end": v(-203.66, 302.11) * mm});
            skLineSegment(sketch, "E8.6.6.8", {"start": v(-203.66, 304.65) * mm, "end": v(-201.12, 304.65) * mm});
            skLineSegment(sketch, "E8.9.6.8", {"start": v(-201.12, 304.65) * mm, "end": v(-201.12, 302.11) * mm});
            skLineSegment(sketch, "E8.0.6.9", {"start": v(-203.66, 299.27) * mm, "end": v(-201.12, 299.27) * mm});
            skLineSegment(sketch, "E8.3.6.9", {"start": v(-203.66, 301.8) * mm, "end": v(-203.66, 299.27) * mm});
            skLineSegment(sketch, "E8.6.6.9", {"start": v(-203.66, 301.8) * mm, "end": v(-201.12, 301.8) * mm});
            skLineSegment(sketch, "E8.9.6.9", {"start": v(-201.12, 301.8) * mm, "end": v(-201.12, 299.27) * mm});
            skLineSegment(sketch, "E8.0.6.10", {"start": v(-203.66, 296.42) * mm, "end": v(-201.12, 296.42) * mm});
            skLineSegment(sketch, "E8.3.6.10", {"start": v(-203.66, 298.96) * mm, "end": v(-203.66, 296.42) * mm});
            skLineSegment(sketch, "E8.6.6.10", {"start": v(-203.66, 298.96) * mm, "end": v(-201.12, 298.96) * mm});
            skLineSegment(sketch, "E8.9.6.10", {"start": v(-201.12, 298.96) * mm, "end": v(-201.12, 296.42) * mm});
            skLineSegment(sketch, "E8.0.6.11", {"start": v(-203.66, 293.58) * mm, "end": v(-201.12, 293.58) * mm});
            skLineSegment(sketch, "E8.3.6.11", {"start": v(-203.66, 296.12) * mm, "end": v(-203.66, 293.58) * mm});
            skLineSegment(sketch, "E8.6.6.11", {"start": v(-203.66, 296.12) * mm, "end": v(-201.12, 296.12) * mm});
            skLineSegment(sketch, "E8.9.6.11", {"start": v(-201.12, 296.12) * mm, "end": v(-201.12, 293.58) * mm});
            skLineSegment(sketch, "E8.0.6.12", {"start": v(-203.66, 290.73) * mm, "end": v(-201.12, 290.73) * mm});
            skLineSegment(sketch, "E8.3.6.12", {"start": v(-203.66, 293.27) * mm, "end": v(-203.66, 290.73) * mm});
            skLineSegment(sketch, "E8.6.6.12", {"start": v(-203.66, 293.27) * mm, "end": v(-201.12, 293.27) * mm});
            skLineSegment(sketch, "E8.9.6.12", {"start": v(-201.12, 293.27) * mm, "end": v(-201.12, 290.73) * mm});
            skLineSegment(sketch, "E8.0.6.13", {"start": v(-203.66, 287.89) * mm, "end": v(-201.12, 287.89) * mm});
            skLineSegment(sketch, "E8.3.6.13", {"start": v(-203.66, 290.43) * mm, "end": v(-203.66, 287.89) * mm});
            skLineSegment(sketch, "E8.6.6.13", {"start": v(-203.66, 290.43) * mm, "end": v(-201.12, 290.43) * mm});
            skLineSegment(sketch, "E8.9.6.13", {"start": v(-201.12, 290.43) * mm, "end": v(-201.12, 287.89) * mm});
            skLineSegment(sketch, "E8.0.6.14", {"start": v(-203.66, 285.04) * mm, "end": v(-201.12, 285.04) * mm});
            skLineSegment(sketch, "E8.3.6.14", {"start": v(-203.66, 287.58) * mm, "end": v(-203.66, 285.04) * mm});
            skLineSegment(sketch, "E8.6.6.14", {"start": v(-203.66, 287.58) * mm, "end": v(-201.12, 287.58) * mm});
            skLineSegment(sketch, "E8.9.6.14", {"start": v(-201.12, 287.58) * mm, "end": v(-201.12, 285.04) * mm});
            skLineSegment(sketch, "E8.0.6.15", {"start": v(-203.66, 282.2) * mm, "end": v(-201.12, 282.2) * mm});
            skLineSegment(sketch, "E8.3.6.15", {"start": v(-203.66, 284.74) * mm, "end": v(-203.66, 282.2) * mm});
            skLineSegment(sketch, "E8.6.6.15", {"start": v(-203.66, 284.74) * mm, "end": v(-201.12, 284.74) * mm});
            skLineSegment(sketch, "E8.9.6.15", {"start": v(-201.12, 284.74) * mm, "end": v(-201.12, 282.2) * mm});
            skLineSegment(sketch, "E8.0.7.2", {"start": v(-200.82, 319.18) * mm, "end": v(-198.28, 319.18) * mm});
            skLineSegment(sketch, "E8.3.7.2", {"start": v(-200.82, 321.72) * mm, "end": v(-200.82, 319.18) * mm});
            skLineSegment(sketch, "E8.6.7.2", {"start": v(-200.82, 321.72) * mm, "end": v(-198.28, 321.72) * mm});
            skLineSegment(sketch, "E8.9.7.2", {"start": v(-198.28, 321.72) * mm, "end": v(-198.28, 319.18) * mm});
            skLineSegment(sketch, "E8.0.7.3", {"start": v(-200.82, 316.34) * mm, "end": v(-198.28, 316.34) * mm});
            skLineSegment(sketch, "E8.3.7.3", {"start": v(-200.82, 318.88) * mm, "end": v(-200.82, 316.34) * mm});
            skLineSegment(sketch, "E8.6.7.3", {"start": v(-200.82, 318.88) * mm, "end": v(-198.28, 318.88) * mm});
            skLineSegment(sketch, "E8.9.7.3", {"start": v(-198.28, 318.88) * mm, "end": v(-198.28, 316.34) * mm});
            skLineSegment(sketch, "E8.0.7.4", {"start": v(-200.82, 313.5) * mm, "end": v(-198.28, 313.5) * mm});
            skLineSegment(sketch, "E8.3.7.4", {"start": v(-200.82, 316.03) * mm, "end": v(-200.82, 313.5) * mm});
            skLineSegment(sketch, "E8.6.7.4", {"start": v(-200.82, 316.03) * mm, "end": v(-198.28, 316.03) * mm});
            skLineSegment(sketch, "E8.9.7.4", {"start": v(-198.28, 316.03) * mm, "end": v(-198.28, 313.5) * mm});
            skLineSegment(sketch, "E8.0.7.5", {"start": v(-200.82, 310.65) * mm, "end": v(-198.28, 310.65) * mm});
            skLineSegment(sketch, "E8.3.7.5", {"start": v(-200.82, 313.19) * mm, "end": v(-200.82, 310.65) * mm});
            skLineSegment(sketch, "E8.6.7.5", {"start": v(-200.82, 313.19) * mm, "end": v(-198.28, 313.19) * mm});
            skLineSegment(sketch, "E8.9.7.5", {"start": v(-198.28, 313.19) * mm, "end": v(-198.28, 310.65) * mm});
            skLineSegment(sketch, "E8.0.7.6", {"start": v(-200.82, 307.8) * mm, "end": v(-198.28, 307.8) * mm});
            skLineSegment(sketch, "E8.3.7.6", {"start": v(-200.82, 310.34) * mm, "end": v(-200.82, 307.8) * mm});
            skLineSegment(sketch, "E8.6.7.6", {"start": v(-200.82, 310.34) * mm, "end": v(-198.28, 310.34) * mm});
            skLineSegment(sketch, "E8.9.7.6", {"start": v(-198.28, 310.34) * mm, "end": v(-198.28, 307.8) * mm});
            skLineSegment(sketch, "E8.0.7.7", {"start": v(-200.82, 304.96) * mm, "end": v(-198.28, 304.96) * mm});
            skLineSegment(sketch, "E8.3.7.7", {"start": v(-200.82, 307.5) * mm, "end": v(-200.82, 304.96) * mm});
            skLineSegment(sketch, "E8.6.7.7", {"start": v(-200.82, 307.5) * mm, "end": v(-198.28, 307.5) * mm});
            skLineSegment(sketch, "E8.9.7.7", {"start": v(-198.28, 307.5) * mm, "end": v(-198.28, 304.96) * mm});
            skLineSegment(sketch, "E8.0.7.8", {"start": v(-200.82, 302.11) * mm, "end": v(-198.28, 302.11) * mm});
            skLineSegment(sketch, "E8.3.7.8", {"start": v(-200.82, 304.65) * mm, "end": v(-200.82, 302.11) * mm});
            skLineSegment(sketch, "E8.6.7.8", {"start": v(-200.82, 304.65) * mm, "end": v(-198.28, 304.65) * mm});
            skLineSegment(sketch, "E8.9.7.8", {"start": v(-198.28, 304.65) * mm, "end": v(-198.28, 302.11) * mm});
            skLineSegment(sketch, "E8.0.7.9", {"start": v(-200.82, 299.27) * mm, "end": v(-198.28, 299.27) * mm});
            skLineSegment(sketch, "E8.3.7.9", {"start": v(-200.82, 301.8) * mm, "end": v(-200.82, 299.27) * mm});
            skLineSegment(sketch, "E8.6.7.9", {"start": v(-200.82, 301.8) * mm, "end": v(-198.28, 301.8) * mm});
            skLineSegment(sketch, "E8.9.7.9", {"start": v(-198.28, 301.8) * mm, "end": v(-198.28, 299.27) * mm});
            skLineSegment(sketch, "E8.0.7.10", {"start": v(-200.82, 296.42) * mm, "end": v(-198.28, 296.42) * mm});
            skLineSegment(sketch, "E8.3.7.10", {"start": v(-200.82, 298.96) * mm, "end": v(-200.82, 296.42) * mm});
            skLineSegment(sketch, "E8.6.7.10", {"start": v(-200.82, 298.96) * mm, "end": v(-198.28, 298.96) * mm});
            skLineSegment(sketch, "E8.9.7.10", {"start": v(-198.28, 298.96) * mm, "end": v(-198.28, 296.42) * mm});
            skLineSegment(sketch, "E8.0.7.11", {"start": v(-200.82, 293.58) * mm, "end": v(-198.28, 293.58) * mm});
            skLineSegment(sketch, "E8.3.7.11", {"start": v(-200.82, 296.12) * mm, "end": v(-200.82, 293.58) * mm});
            skLineSegment(sketch, "E8.6.7.11", {"start": v(-200.82, 296.12) * mm, "end": v(-198.28, 296.12) * mm});
            skLineSegment(sketch, "E8.9.7.11", {"start": v(-198.28, 296.12) * mm, "end": v(-198.28, 293.58) * mm});
            skLineSegment(sketch, "E8.0.7.12", {"start": v(-200.82, 290.73) * mm, "end": v(-198.28, 290.73) * mm});
            skLineSegment(sketch, "E8.3.7.12", {"start": v(-200.82, 293.27) * mm, "end": v(-200.82, 290.73) * mm});
            skLineSegment(sketch, "E8.6.7.12", {"start": v(-200.82, 293.27) * mm, "end": v(-198.28, 293.27) * mm});
            skLineSegment(sketch, "E8.9.7.12", {"start": v(-198.28, 293.27) * mm, "end": v(-198.28, 290.73) * mm});
            skLineSegment(sketch, "E8.0.7.13", {"start": v(-200.82, 287.89) * mm, "end": v(-198.28, 287.89) * mm});
            skLineSegment(sketch, "E8.3.7.13", {"start": v(-200.82, 290.43) * mm, "end": v(-200.82, 287.89) * mm});
            skLineSegment(sketch, "E8.6.7.13", {"start": v(-200.82, 290.43) * mm, "end": v(-198.28, 290.43) * mm});
            skLineSegment(sketch, "E8.9.7.13", {"start": v(-198.28, 290.43) * mm, "end": v(-198.28, 287.89) * mm});
            skLineSegment(sketch, "E8.0.7.14", {"start": v(-200.82, 285.04) * mm, "end": v(-198.28, 285.04) * mm});
            skLineSegment(sketch, "E8.3.7.14", {"start": v(-200.82, 287.58) * mm, "end": v(-200.82, 285.04) * mm});
            skLineSegment(sketch, "E8.6.7.14", {"start": v(-200.82, 287.58) * mm, "end": v(-198.28, 287.58) * mm});
            skLineSegment(sketch, "E8.9.7.14", {"start": v(-198.28, 287.58) * mm, "end": v(-198.28, 285.04) * mm});
            skLineSegment(sketch, "E8.0.7.15", {"start": v(-200.82, 282.2) * mm, "end": v(-198.28, 282.2) * mm});
            skLineSegment(sketch, "E8.3.7.15", {"start": v(-200.82, 284.74) * mm, "end": v(-200.82, 282.2) * mm});
            skLineSegment(sketch, "E8.6.7.15", {"start": v(-200.82, 284.74) * mm, "end": v(-198.28, 284.74) * mm});
            skLineSegment(sketch, "E8.9.7.15", {"start": v(-198.28, 284.74) * mm, "end": v(-198.28, 282.2) * mm});
            skLineSegment(sketch, "E8.0.8.2", {"start": v(-197.97, 319.18) * mm, "end": v(-195.43, 319.18) * mm});
            skLineSegment(sketch, "E8.3.8.2", {"start": v(-197.97, 321.72) * mm, "end": v(-197.97, 319.18) * mm});
            skLineSegment(sketch, "E8.6.8.2", {"start": v(-197.97, 321.72) * mm, "end": v(-195.43, 321.72) * mm});
            skLineSegment(sketch, "E8.9.8.2", {"start": v(-195.43, 321.72) * mm, "end": v(-195.43, 319.18) * mm});
            skLineSegment(sketch, "E8.0.8.3", {"start": v(-197.97, 316.34) * mm, "end": v(-195.43, 316.34) * mm});
            skLineSegment(sketch, "E8.3.8.3", {"start": v(-197.97, 318.88) * mm, "end": v(-197.97, 316.34) * mm});
            skLineSegment(sketch, "E8.6.8.3", {"start": v(-197.97, 318.88) * mm, "end": v(-195.43, 318.88) * mm});
            skLineSegment(sketch, "E8.9.8.3", {"start": v(-195.43, 318.88) * mm, "end": v(-195.43, 316.34) * mm});
            skLineSegment(sketch, "E8.0.8.4", {"start": v(-197.97, 313.5) * mm, "end": v(-195.43, 313.5) * mm});
            skLineSegment(sketch, "E8.3.8.4", {"start": v(-197.97, 316.03) * mm, "end": v(-197.97, 313.5) * mm});
            skLineSegment(sketch, "E8.6.8.4", {"start": v(-197.97, 316.03) * mm, "end": v(-195.43, 316.03) * mm});
            skLineSegment(sketch, "E8.9.8.4", {"start": v(-195.43, 316.03) * mm, "end": v(-195.43, 313.5) * mm});
            skLineSegment(sketch, "E8.0.8.5", {"start": v(-197.97, 310.65) * mm, "end": v(-195.43, 310.65) * mm});
            skLineSegment(sketch, "E8.3.8.5", {"start": v(-197.97, 313.19) * mm, "end": v(-197.97, 310.65) * mm});
            skLineSegment(sketch, "E8.6.8.5", {"start": v(-197.97, 313.19) * mm, "end": v(-195.43, 313.19) * mm});
            skLineSegment(sketch, "E8.9.8.5", {"start": v(-195.43, 313.19) * mm, "end": v(-195.43, 310.65) * mm});
            skLineSegment(sketch, "E8.0.8.6", {"start": v(-197.97, 307.8) * mm, "end": v(-195.43, 307.8) * mm});
            skLineSegment(sketch, "E8.3.8.6", {"start": v(-197.97, 310.34) * mm, "end": v(-197.97, 307.8) * mm});
            skLineSegment(sketch, "E8.6.8.6", {"start": v(-197.97, 310.34) * mm, "end": v(-195.43, 310.34) * mm});
            skLineSegment(sketch, "E8.9.8.6", {"start": v(-195.43, 310.34) * mm, "end": v(-195.43, 307.8) * mm});
            skLineSegment(sketch, "E8.0.8.7", {"start": v(-197.97, 304.96) * mm, "end": v(-195.43, 304.96) * mm});
            skLineSegment(sketch, "E8.3.8.7", {"start": v(-197.97, 307.5) * mm, "end": v(-197.97, 304.96) * mm});
            skLineSegment(sketch, "E8.6.8.7", {"start": v(-197.97, 307.5) * mm, "end": v(-195.43, 307.5) * mm});
            skLineSegment(sketch, "E8.9.8.7", {"start": v(-195.43, 307.5) * mm, "end": v(-195.43, 304.96) * mm});
            skLineSegment(sketch, "E8.0.8.8", {"start": v(-197.97, 302.11) * mm, "end": v(-195.43, 302.11) * mm});
            skLineSegment(sketch, "E8.3.8.8", {"start": v(-197.97, 304.65) * mm, "end": v(-197.97, 302.11) * mm});
            skLineSegment(sketch, "E8.6.8.8", {"start": v(-197.97, 304.65) * mm, "end": v(-195.43, 304.65) * mm});
            skLineSegment(sketch, "E8.9.8.8", {"start": v(-195.43, 304.65) * mm, "end": v(-195.43, 302.11) * mm});
            skLineSegment(sketch, "E8.0.8.9", {"start": v(-197.97, 299.27) * mm, "end": v(-195.43, 299.27) * mm});
            skLineSegment(sketch, "E8.3.8.9", {"start": v(-197.97, 301.8) * mm, "end": v(-197.97, 299.27) * mm});
            skLineSegment(sketch, "E8.6.8.9", {"start": v(-197.97, 301.8) * mm, "end": v(-195.43, 301.8) * mm});
            skLineSegment(sketch, "E8.9.8.9", {"start": v(-195.43, 301.8) * mm, "end": v(-195.43, 299.27) * mm});
            skLineSegment(sketch, "E8.0.8.10", {"start": v(-197.97, 296.42) * mm, "end": v(-195.43, 296.42) * mm});
            skLineSegment(sketch, "E8.3.8.10", {"start": v(-197.97, 298.96) * mm, "end": v(-197.97, 296.42) * mm});
            skLineSegment(sketch, "E8.6.8.10", {"start": v(-197.97, 298.96) * mm, "end": v(-195.43, 298.96) * mm});
            skLineSegment(sketch, "E8.9.8.10", {"start": v(-195.43, 298.96) * mm, "end": v(-195.43, 296.42) * mm});
            skLineSegment(sketch, "E8.0.8.11", {"start": v(-197.97, 293.58) * mm, "end": v(-195.43, 293.58) * mm});
            skLineSegment(sketch, "E8.3.8.11", {"start": v(-197.97, 296.12) * mm, "end": v(-197.97, 293.58) * mm});
            skLineSegment(sketch, "E8.6.8.11", {"start": v(-197.97, 296.12) * mm, "end": v(-195.43, 296.12) * mm});
            skLineSegment(sketch, "E8.9.8.11", {"start": v(-195.43, 296.12) * mm, "end": v(-195.43, 293.58) * mm});
            skLineSegment(sketch, "E8.0.8.12", {"start": v(-197.97, 290.73) * mm, "end": v(-195.43, 290.73) * mm});
            skLineSegment(sketch, "E8.3.8.12", {"start": v(-197.97, 293.27) * mm, "end": v(-197.97, 290.73) * mm});
            skLineSegment(sketch, "E8.6.8.12", {"start": v(-197.97, 293.27) * mm, "end": v(-195.43, 293.27) * mm});
            skLineSegment(sketch, "E8.9.8.12", {"start": v(-195.43, 293.27) * mm, "end": v(-195.43, 290.73) * mm});
            skLineSegment(sketch, "E8.0.8.13", {"start": v(-197.97, 287.89) * mm, "end": v(-195.43, 287.89) * mm});
            skLineSegment(sketch, "E8.3.8.13", {"start": v(-197.97, 290.43) * mm, "end": v(-197.97, 287.89) * mm});
            skLineSegment(sketch, "E8.6.8.13", {"start": v(-197.97, 290.43) * mm, "end": v(-195.43, 290.43) * mm});
            skLineSegment(sketch, "E8.9.8.13", {"start": v(-195.43, 290.43) * mm, "end": v(-195.43, 287.89) * mm});
            skLineSegment(sketch, "E8.0.8.14", {"start": v(-197.97, 285.04) * mm, "end": v(-195.43, 285.04) * mm});
            skLineSegment(sketch, "E8.3.8.14", {"start": v(-197.97, 287.58) * mm, "end": v(-197.97, 285.04) * mm});
            skLineSegment(sketch, "E8.6.8.14", {"start": v(-197.97, 287.58) * mm, "end": v(-195.43, 287.58) * mm});
            skLineSegment(sketch, "E8.9.8.14", {"start": v(-195.43, 287.58) * mm, "end": v(-195.43, 285.04) * mm});
            skLineSegment(sketch, "E8.0.8.15", {"start": v(-197.97, 282.2) * mm, "end": v(-195.43, 282.2) * mm});
            skLineSegment(sketch, "E8.3.8.15", {"start": v(-197.97, 284.74) * mm, "end": v(-197.97, 282.2) * mm});
            skLineSegment(sketch, "E8.6.8.15", {"start": v(-197.97, 284.74) * mm, "end": v(-195.43, 284.74) * mm});
            skLineSegment(sketch, "E8.9.8.15", {"start": v(-195.43, 284.74) * mm, "end": v(-195.43, 282.2) * mm});
            skLineSegment(sketch, "E8.0.9.2", {"start": v(-195.13, 319.18) * mm, "end": v(-192.59, 319.18) * mm});
            skLineSegment(sketch, "E8.3.9.2", {"start": v(-195.13, 321.72) * mm, "end": v(-195.13, 319.18) * mm});
            skLineSegment(sketch, "E8.6.9.2", {"start": v(-195.13, 321.72) * mm, "end": v(-192.59, 321.72) * mm});
            skLineSegment(sketch, "E8.9.9.2", {"start": v(-192.59, 321.72) * mm, "end": v(-192.59, 319.18) * mm});
            skLineSegment(sketch, "E8.0.9.3", {"start": v(-195.13, 316.34) * mm, "end": v(-192.59, 316.34) * mm});
            skLineSegment(sketch, "E8.3.9.3", {"start": v(-195.13, 318.88) * mm, "end": v(-195.13, 316.34) * mm});
            skLineSegment(sketch, "E8.6.9.3", {"start": v(-195.13, 318.88) * mm, "end": v(-192.59, 318.88) * mm});
            skLineSegment(sketch, "E8.9.9.3", {"start": v(-192.59, 318.88) * mm, "end": v(-192.59, 316.34) * mm});
            skLineSegment(sketch, "E8.0.9.4", {"start": v(-195.13, 313.5) * mm, "end": v(-192.59, 313.5) * mm});
            skLineSegment(sketch, "E8.3.9.4", {"start": v(-195.13, 316.03) * mm, "end": v(-195.13, 313.5) * mm});
            skLineSegment(sketch, "E8.6.9.4", {"start": v(-195.13, 316.03) * mm, "end": v(-192.59, 316.03) * mm});
            skLineSegment(sketch, "E8.9.9.4", {"start": v(-192.59, 316.03) * mm, "end": v(-192.59, 313.5) * mm});
            skLineSegment(sketch, "E8.0.9.5", {"start": v(-195.13, 310.65) * mm, "end": v(-192.59, 310.65) * mm});
            skLineSegment(sketch, "E8.3.9.5", {"start": v(-195.13, 313.19) * mm, "end": v(-195.13, 310.65) * mm});
            skLineSegment(sketch, "E8.6.9.5", {"start": v(-195.13, 313.19) * mm, "end": v(-192.59, 313.19) * mm});
            skLineSegment(sketch, "E8.9.9.5", {"start": v(-192.59, 313.19) * mm, "end": v(-192.59, 310.65) * mm});
            skLineSegment(sketch, "E8.0.9.6", {"start": v(-195.13, 307.8) * mm, "end": v(-192.59, 307.8) * mm});
            skLineSegment(sketch, "E8.3.9.6", {"start": v(-195.13, 310.34) * mm, "end": v(-195.13, 307.8) * mm});
            skLineSegment(sketch, "E8.6.9.6", {"start": v(-195.13, 310.34) * mm, "end": v(-192.59, 310.34) * mm});
            skLineSegment(sketch, "E8.9.9.6", {"start": v(-192.59, 310.34) * mm, "end": v(-192.59, 307.8) * mm});
            skLineSegment(sketch, "E8.0.9.7", {"start": v(-195.13, 304.96) * mm, "end": v(-192.59, 304.96) * mm});
            skLineSegment(sketch, "E8.3.9.7", {"start": v(-195.13, 307.5) * mm, "end": v(-195.13, 304.96) * mm});
            skLineSegment(sketch, "E8.6.9.7", {"start": v(-195.13, 307.5) * mm, "end": v(-192.59, 307.5) * mm});
            skLineSegment(sketch, "E8.9.9.7", {"start": v(-192.59, 307.5) * mm, "end": v(-192.59, 304.96) * mm});
            skLineSegment(sketch, "E8.0.9.8", {"start": v(-195.13, 302.11) * mm, "end": v(-192.59, 302.11) * mm});
            skLineSegment(sketch, "E8.3.9.8", {"start": v(-195.13, 304.65) * mm, "end": v(-195.13, 302.11) * mm});
            skLineSegment(sketch, "E8.6.9.8", {"start": v(-195.13, 304.65) * mm, "end": v(-192.59, 304.65) * mm});
            skLineSegment(sketch, "E8.9.9.8", {"start": v(-192.59, 304.65) * mm, "end": v(-192.59, 302.11) * mm});
            skLineSegment(sketch, "E8.0.9.9", {"start": v(-195.13, 299.27) * mm, "end": v(-192.59, 299.27) * mm});
            skLineSegment(sketch, "E8.3.9.9", {"start": v(-195.13, 301.8) * mm, "end": v(-195.13, 299.27) * mm});
            skLineSegment(sketch, "E8.6.9.9", {"start": v(-195.13, 301.8) * mm, "end": v(-192.59, 301.8) * mm});
            skLineSegment(sketch, "E8.9.9.9", {"start": v(-192.59, 301.8) * mm, "end": v(-192.59, 299.27) * mm});
            skLineSegment(sketch, "E8.0.9.10", {"start": v(-195.13, 296.42) * mm, "end": v(-192.59, 296.42) * mm});
            skLineSegment(sketch, "E8.3.9.10", {"start": v(-195.13, 298.96) * mm, "end": v(-195.13, 296.42) * mm});
            skLineSegment(sketch, "E8.6.9.10", {"start": v(-195.13, 298.96) * mm, "end": v(-192.59, 298.96) * mm});
            skLineSegment(sketch, "E8.9.9.10", {"start": v(-192.59, 298.96) * mm, "end": v(-192.59, 296.42) * mm});
            skLineSegment(sketch, "E8.0.9.11", {"start": v(-195.13, 293.58) * mm, "end": v(-192.59, 293.58) * mm});
            skLineSegment(sketch, "E8.3.9.11", {"start": v(-195.13, 296.12) * mm, "end": v(-195.13, 293.58) * mm});
            skLineSegment(sketch, "E8.6.9.11", {"start": v(-195.13, 296.12) * mm, "end": v(-192.59, 296.12) * mm});
            skLineSegment(sketch, "E8.9.9.11", {"start": v(-192.59, 296.12) * mm, "end": v(-192.59, 293.58) * mm});
            skLineSegment(sketch, "E8.0.9.12", {"start": v(-195.13, 290.73) * mm, "end": v(-192.59, 290.73) * mm});
            skLineSegment(sketch, "E8.3.9.12", {"start": v(-195.13, 293.27) * mm, "end": v(-195.13, 290.73) * mm});
            skLineSegment(sketch, "E8.6.9.12", {"start": v(-195.13, 293.27) * mm, "end": v(-192.59, 293.27) * mm});
            skLineSegment(sketch, "E8.9.9.12", {"start": v(-192.59, 293.27) * mm, "end": v(-192.59, 290.73) * mm});
            skLineSegment(sketch, "E8.0.9.13", {"start": v(-195.13, 287.89) * mm, "end": v(-192.59, 287.89) * mm});
            skLineSegment(sketch, "E8.3.9.13", {"start": v(-195.13, 290.43) * mm, "end": v(-195.13, 287.89) * mm});
            skLineSegment(sketch, "E8.6.9.13", {"start": v(-195.13, 290.43) * mm, "end": v(-192.59, 290.43) * mm});
            skLineSegment(sketch, "E8.9.9.13", {"start": v(-192.59, 290.43) * mm, "end": v(-192.59, 287.89) * mm});
            skLineSegment(sketch, "E8.0.9.14", {"start": v(-195.13, 285.04) * mm, "end": v(-192.59, 285.04) * mm});
            skLineSegment(sketch, "E8.3.9.14", {"start": v(-195.13, 287.58) * mm, "end": v(-195.13, 285.04) * mm});
            skLineSegment(sketch, "E8.6.9.14", {"start": v(-195.13, 287.58) * mm, "end": v(-192.59, 287.58) * mm});
            skLineSegment(sketch, "E8.9.9.14", {"start": v(-192.59, 287.58) * mm, "end": v(-192.59, 285.04) * mm});
            skLineSegment(sketch, "E8.0.9.15", {"start": v(-195.13, 282.2) * mm, "end": v(-192.59, 282.2) * mm});
            skLineSegment(sketch, "E8.3.9.15", {"start": v(-195.13, 284.74) * mm, "end": v(-195.13, 282.2) * mm});
            skLineSegment(sketch, "E8.6.9.15", {"start": v(-195.13, 284.74) * mm, "end": v(-192.59, 284.74) * mm});
            skLineSegment(sketch, "E8.9.9.15", {"start": v(-192.59, 284.74) * mm, "end": v(-192.59, 282.2) * mm});
            skLineSegment(sketch, "E8.0.10.2", {"start": v(-192.28, 319.18) * mm, "end": v(-189.74, 319.18) * mm});
            skLineSegment(sketch, "E8.3.10.2", {"start": v(-192.28, 321.72) * mm, "end": v(-192.28, 319.18) * mm});
            skLineSegment(sketch, "E8.6.10.2", {"start": v(-192.28, 321.72) * mm, "end": v(-189.74, 321.72) * mm});
            skLineSegment(sketch, "E8.9.10.2", {"start": v(-189.74, 321.72) * mm, "end": v(-189.74, 319.18) * mm});
            skLineSegment(sketch, "E8.0.10.3", {"start": v(-192.28, 316.34) * mm, "end": v(-189.74, 316.34) * mm});
            skLineSegment(sketch, "E8.3.10.3", {"start": v(-192.28, 318.88) * mm, "end": v(-192.28, 316.34) * mm});
            skLineSegment(sketch, "E8.6.10.3", {"start": v(-192.28, 318.88) * mm, "end": v(-189.74, 318.88) * mm});
            skLineSegment(sketch, "E8.9.10.3", {"start": v(-189.74, 318.88) * mm, "end": v(-189.74, 316.34) * mm});
            skLineSegment(sketch, "E8.0.10.4", {"start": v(-192.28, 313.5) * mm, "end": v(-189.74, 313.5) * mm});
            skLineSegment(sketch, "E8.3.10.4", {"start": v(-192.28, 316.03) * mm, "end": v(-192.28, 313.5) * mm});
            skLineSegment(sketch, "E8.6.10.4", {"start": v(-192.28, 316.03) * mm, "end": v(-189.74, 316.03) * mm});
            skLineSegment(sketch, "E8.9.10.4", {"start": v(-189.74, 316.03) * mm, "end": v(-189.74, 313.5) * mm});
            skLineSegment(sketch, "E8.0.10.5", {"start": v(-192.28, 310.65) * mm, "end": v(-189.74, 310.65) * mm});
            skLineSegment(sketch, "E8.3.10.5", {"start": v(-192.28, 313.19) * mm, "end": v(-192.28, 310.65) * mm});
            skLineSegment(sketch, "E8.6.10.5", {"start": v(-192.28, 313.19) * mm, "end": v(-189.74, 313.19) * mm});
            skLineSegment(sketch, "E8.9.10.5", {"start": v(-189.74, 313.19) * mm, "end": v(-189.74, 310.65) * mm});
            skLineSegment(sketch, "E8.0.10.6", {"start": v(-192.28, 307.8) * mm, "end": v(-189.74, 307.8) * mm});
            skLineSegment(sketch, "E8.3.10.6", {"start": v(-192.28, 310.34) * mm, "end": v(-192.28, 307.8) * mm});
            skLineSegment(sketch, "E8.6.10.6", {"start": v(-192.28, 310.34) * mm, "end": v(-189.74, 310.34) * mm});
            skLineSegment(sketch, "E8.9.10.6", {"start": v(-189.74, 310.34) * mm, "end": v(-189.74, 307.8) * mm});
            skLineSegment(sketch, "E8.0.10.7", {"start": v(-192.28, 304.96) * mm, "end": v(-189.74, 304.96) * mm});
            skLineSegment(sketch, "E8.3.10.7", {"start": v(-192.28, 307.5) * mm, "end": v(-192.28, 304.96) * mm});
            skLineSegment(sketch, "E8.6.10.7", {"start": v(-192.28, 307.5) * mm, "end": v(-189.74, 307.5) * mm});
            skLineSegment(sketch, "E8.9.10.7", {"start": v(-189.74, 307.5) * mm, "end": v(-189.74, 304.96) * mm});
            skLineSegment(sketch, "E8.0.10.8", {"start": v(-192.28, 302.11) * mm, "end": v(-189.74, 302.11) * mm});
            skLineSegment(sketch, "E8.3.10.8", {"start": v(-192.28, 304.65) * mm, "end": v(-192.28, 302.11) * mm});
            skLineSegment(sketch, "E8.6.10.8", {"start": v(-192.28, 304.65) * mm, "end": v(-189.74, 304.65) * mm});
            skLineSegment(sketch, "E8.9.10.8", {"start": v(-189.74, 304.65) * mm, "end": v(-189.74, 302.11) * mm});
            skLineSegment(sketch, "E8.0.10.9", {"start": v(-192.28, 299.27) * mm, "end": v(-189.74, 299.27) * mm});
            skLineSegment(sketch, "E8.3.10.9", {"start": v(-192.28, 301.8) * mm, "end": v(-192.28, 299.27) * mm});
            skLineSegment(sketch, "E8.6.10.9", {"start": v(-192.28, 301.8) * mm, "end": v(-189.74, 301.8) * mm});
            skLineSegment(sketch, "E8.9.10.9", {"start": v(-189.74, 301.8) * mm, "end": v(-189.74, 299.27) * mm});
            skLineSegment(sketch, "E8.0.10.10", {"start": v(-192.28, 296.42) * mm, "end": v(-189.74, 296.42) * mm});
            skLineSegment(sketch, "E8.3.10.10", {"start": v(-192.28, 298.96) * mm, "end": v(-192.28, 296.42) * mm});
            skLineSegment(sketch, "E8.6.10.10", {"start": v(-192.28, 298.96) * mm, "end": v(-189.74, 298.96) * mm});
            skLineSegment(sketch, "E8.9.10.10", {"start": v(-189.74, 298.96) * mm, "end": v(-189.74, 296.42) * mm});
            skLineSegment(sketch, "E8.0.10.11", {"start": v(-192.28, 293.58) * mm, "end": v(-189.74, 293.58) * mm});
            skLineSegment(sketch, "E8.3.10.11", {"start": v(-192.28, 296.12) * mm, "end": v(-192.28, 293.58) * mm});
            skLineSegment(sketch, "E8.6.10.11", {"start": v(-192.28, 296.12) * mm, "end": v(-189.74, 296.12) * mm});
            skLineSegment(sketch, "E8.9.10.11", {"start": v(-189.74, 296.12) * mm, "end": v(-189.74, 293.58) * mm});
            skLineSegment(sketch, "E8.0.10.12", {"start": v(-192.28, 290.73) * mm, "end": v(-189.74, 290.73) * mm});
            skLineSegment(sketch, "E8.3.10.12", {"start": v(-192.28, 293.27) * mm, "end": v(-192.28, 290.73) * mm});
            skLineSegment(sketch, "E8.6.10.12", {"start": v(-192.28, 293.27) * mm, "end": v(-189.74, 293.27) * mm});
            skLineSegment(sketch, "E8.9.10.12", {"start": v(-189.74, 293.27) * mm, "end": v(-189.74, 290.73) * mm});
            skLineSegment(sketch, "E8.0.10.13", {"start": v(-192.28, 287.89) * mm, "end": v(-189.74, 287.89) * mm});
            skLineSegment(sketch, "E8.3.10.13", {"start": v(-192.28, 290.43) * mm, "end": v(-192.28, 287.89) * mm});
            skLineSegment(sketch, "E8.6.10.13", {"start": v(-192.28, 290.43) * mm, "end": v(-189.74, 290.43) * mm});
            skLineSegment(sketch, "E8.9.10.13", {"start": v(-189.74, 290.43) * mm, "end": v(-189.74, 287.89) * mm});
            skLineSegment(sketch, "E8.0.10.14", {"start": v(-192.28, 285.04) * mm, "end": v(-189.74, 285.04) * mm});
            skLineSegment(sketch, "E8.3.10.14", {"start": v(-192.28, 287.58) * mm, "end": v(-192.28, 285.04) * mm});
            skLineSegment(sketch, "E8.6.10.14", {"start": v(-192.28, 287.58) * mm, "end": v(-189.74, 287.58) * mm});
            skLineSegment(sketch, "E8.9.10.14", {"start": v(-189.74, 287.58) * mm, "end": v(-189.74, 285.04) * mm});
            skLineSegment(sketch, "E8.0.10.15", {"start": v(-192.28, 282.2) * mm, "end": v(-189.74, 282.2) * mm});
            skLineSegment(sketch, "E8.3.10.15", {"start": v(-192.28, 284.74) * mm, "end": v(-192.28, 282.2) * mm});
            skLineSegment(sketch, "E8.6.10.15", {"start": v(-192.28, 284.74) * mm, "end": v(-189.74, 284.74) * mm});
            skLineSegment(sketch, "E8.9.10.15", {"start": v(-189.74, 284.74) * mm, "end": v(-189.74, 282.2) * mm});
            skLineSegment(sketch, "E8.0.11.2", {"start": v(-189.44, 319.18) * mm, "end": v(-186.9, 319.18) * mm});
            skLineSegment(sketch, "E8.3.11.2", {"start": v(-189.44, 321.72) * mm, "end": v(-189.44, 319.18) * mm});
            skLineSegment(sketch, "E8.6.11.2", {"start": v(-189.44, 321.72) * mm, "end": v(-186.9, 321.72) * mm});
            skLineSegment(sketch, "E8.9.11.2", {"start": v(-186.9, 321.72) * mm, "end": v(-186.9, 319.18) * mm});
            skLineSegment(sketch, "E8.0.11.3", {"start": v(-189.44, 316.34) * mm, "end": v(-186.9, 316.34) * mm});
            skLineSegment(sketch, "E8.3.11.3", {"start": v(-189.44, 318.88) * mm, "end": v(-189.44, 316.34) * mm});
            skLineSegment(sketch, "E8.6.11.3", {"start": v(-189.44, 318.88) * mm, "end": v(-186.9, 318.88) * mm});
            skLineSegment(sketch, "E8.9.11.3", {"start": v(-186.9, 318.88) * mm, "end": v(-186.9, 316.34) * mm});
            skLineSegment(sketch, "E8.0.11.4", {"start": v(-189.44, 313.5) * mm, "end": v(-186.9, 313.5) * mm});
            skLineSegment(sketch, "E8.3.11.4", {"start": v(-189.44, 316.03) * mm, "end": v(-189.44, 313.5) * mm});
            skLineSegment(sketch, "E8.6.11.4", {"start": v(-189.44, 316.03) * mm, "end": v(-186.9, 316.03) * mm});
            skLineSegment(sketch, "E8.9.11.4", {"start": v(-186.9, 316.03) * mm, "end": v(-186.9, 313.5) * mm});
            skLineSegment(sketch, "E8.0.11.5", {"start": v(-189.44, 310.65) * mm, "end": v(-186.9, 310.65) * mm});
            skLineSegment(sketch, "E8.3.11.5", {"start": v(-189.44, 313.19) * mm, "end": v(-189.44, 310.65) * mm});
            skLineSegment(sketch, "E8.6.11.5", {"start": v(-189.44, 313.19) * mm, "end": v(-186.9, 313.19) * mm});
            skLineSegment(sketch, "E8.9.11.5", {"start": v(-186.9, 313.19) * mm, "end": v(-186.9, 310.65) * mm});
            skLineSegment(sketch, "E8.0.11.6", {"start": v(-189.44, 307.8) * mm, "end": v(-186.9, 307.8) * mm});
            skLineSegment(sketch, "E8.3.11.6", {"start": v(-189.44, 310.34) * mm, "end": v(-189.44, 307.8) * mm});
            skLineSegment(sketch, "E8.6.11.6", {"start": v(-189.44, 310.34) * mm, "end": v(-186.9, 310.34) * mm});
            skLineSegment(sketch, "E8.9.11.6", {"start": v(-186.9, 310.34) * mm, "end": v(-186.9, 307.8) * mm});
            skLineSegment(sketch, "E8.0.11.7", {"start": v(-189.44, 304.96) * mm, "end": v(-186.9, 304.96) * mm});
            skLineSegment(sketch, "E8.3.11.7", {"start": v(-189.44, 307.5) * mm, "end": v(-189.44, 304.96) * mm});
            skLineSegment(sketch, "E8.6.11.7", {"start": v(-189.44, 307.5) * mm, "end": v(-186.9, 307.5) * mm});
            skLineSegment(sketch, "E8.9.11.7", {"start": v(-186.9, 307.5) * mm, "end": v(-186.9, 304.96) * mm});
            skLineSegment(sketch, "E8.0.11.8", {"start": v(-189.44, 302.11) * mm, "end": v(-186.9, 302.11) * mm});
            skLineSegment(sketch, "E8.3.11.8", {"start": v(-189.44, 304.65) * mm, "end": v(-189.44, 302.11) * mm});
            skLineSegment(sketch, "E8.6.11.8", {"start": v(-189.44, 304.65) * mm, "end": v(-186.9, 304.65) * mm});
            skLineSegment(sketch, "E8.9.11.8", {"start": v(-186.9, 304.65) * mm, "end": v(-186.9, 302.11) * mm});
            skLineSegment(sketch, "E8.0.11.9", {"start": v(-189.44, 299.27) * mm, "end": v(-186.9, 299.27) * mm});
            skLineSegment(sketch, "E8.3.11.9", {"start": v(-189.44, 301.8) * mm, "end": v(-189.44, 299.27) * mm});
            skLineSegment(sketch, "E8.6.11.9", {"start": v(-189.44, 301.8) * mm, "end": v(-186.9, 301.8) * mm});
            skLineSegment(sketch, "E8.9.11.9", {"start": v(-186.9, 301.8) * mm, "end": v(-186.9, 299.27) * mm});
            skLineSegment(sketch, "E8.0.11.10", {"start": v(-189.44, 296.42) * mm, "end": v(-186.9, 296.42) * mm});
            skLineSegment(sketch, "E8.3.11.10", {"start": v(-189.44, 298.96) * mm, "end": v(-189.44, 296.42) * mm});
            skLineSegment(sketch, "E8.6.11.10", {"start": v(-189.44, 298.96) * mm, "end": v(-186.9, 298.96) * mm});
            skLineSegment(sketch, "E8.9.11.10", {"start": v(-186.9, 298.96) * mm, "end": v(-186.9, 296.42) * mm});
            skLineSegment(sketch, "E8.0.11.11", {"start": v(-189.44, 293.58) * mm, "end": v(-186.9, 293.58) * mm});
            skLineSegment(sketch, "E8.3.11.11", {"start": v(-189.44, 296.12) * mm, "end": v(-189.44, 293.58) * mm});
            skLineSegment(sketch, "E8.6.11.11", {"start": v(-189.44, 296.12) * mm, "end": v(-186.9, 296.12) * mm});
            skLineSegment(sketch, "E8.9.11.11", {"start": v(-186.9, 296.12) * mm, "end": v(-186.9, 293.58) * mm});
            skLineSegment(sketch, "E8.0.11.12", {"start": v(-189.44, 290.73) * mm, "end": v(-186.9, 290.73) * mm});
            skLineSegment(sketch, "E8.3.11.12", {"start": v(-189.44, 293.27) * mm, "end": v(-189.44, 290.73) * mm});
            skLineSegment(sketch, "E8.6.11.12", {"start": v(-189.44, 293.27) * mm, "end": v(-186.9, 293.27) * mm});
            skLineSegment(sketch, "E8.9.11.12", {"start": v(-186.9, 293.27) * mm, "end": v(-186.9, 290.73) * mm});
            skLineSegment(sketch, "E8.0.11.13", {"start": v(-189.44, 287.89) * mm, "end": v(-186.9, 287.89) * mm});
            skLineSegment(sketch, "E8.3.11.13", {"start": v(-189.44, 290.43) * mm, "end": v(-189.44, 287.89) * mm});
            skLineSegment(sketch, "E8.6.11.13", {"start": v(-189.44, 290.43) * mm, "end": v(-186.9, 290.43) * mm});
            skLineSegment(sketch, "E8.9.11.13", {"start": v(-186.9, 290.43) * mm, "end": v(-186.9, 287.89) * mm});
            skLineSegment(sketch, "E8.0.11.14", {"start": v(-189.44, 285.04) * mm, "end": v(-186.9, 285.04) * mm});
            skLineSegment(sketch, "E8.3.11.14", {"start": v(-189.44, 287.58) * mm, "end": v(-189.44, 285.04) * mm});
            skLineSegment(sketch, "E8.6.11.14", {"start": v(-189.44, 287.58) * mm, "end": v(-186.9, 287.58) * mm});
            skLineSegment(sketch, "E8.9.11.14", {"start": v(-186.9, 287.58) * mm, "end": v(-186.9, 285.04) * mm});
            skLineSegment(sketch, "E8.0.11.15", {"start": v(-189.44, 282.2) * mm, "end": v(-186.9, 282.2) * mm});
            skLineSegment(sketch, "E8.3.11.15", {"start": v(-189.44, 284.74) * mm, "end": v(-189.44, 282.2) * mm});
            skLineSegment(sketch, "E8.6.11.15", {"start": v(-189.44, 284.74) * mm, "end": v(-186.9, 284.74) * mm});
            skLineSegment(sketch, "E8.9.11.15", {"start": v(-186.9, 284.74) * mm, "end": v(-186.9, 282.2) * mm});
            skLineSegment(sketch, "E8.0.12.2", {"start": v(-186.6, 319.18) * mm, "end": v(-184.05, 319.18) * mm});
            skLineSegment(sketch, "E8.3.12.2", {"start": v(-186.6, 321.72) * mm, "end": v(-186.6, 319.18) * mm});
            skLineSegment(sketch, "E8.6.12.2", {"start": v(-186.6, 321.72) * mm, "end": v(-184.05, 321.72) * mm});
            skLineSegment(sketch, "E8.9.12.2", {"start": v(-184.05, 321.72) * mm, "end": v(-184.05, 319.18) * mm});
            skLineSegment(sketch, "E8.0.12.3", {"start": v(-186.6, 316.34) * mm, "end": v(-184.05, 316.34) * mm});
            skLineSegment(sketch, "E8.3.12.3", {"start": v(-186.6, 318.88) * mm, "end": v(-186.6, 316.34) * mm});
            skLineSegment(sketch, "E8.6.12.3", {"start": v(-186.6, 318.88) * mm, "end": v(-184.05, 318.88) * mm});
            skLineSegment(sketch, "E8.9.12.3", {"start": v(-184.05, 318.88) * mm, "end": v(-184.05, 316.34) * mm});
            skLineSegment(sketch, "E8.0.12.4", {"start": v(-186.6, 313.5) * mm, "end": v(-184.05, 313.5) * mm});
            skLineSegment(sketch, "E8.3.12.4", {"start": v(-186.6, 316.03) * mm, "end": v(-186.6, 313.5) * mm});
            skLineSegment(sketch, "E8.6.12.4", {"start": v(-186.6, 316.03) * mm, "end": v(-184.05, 316.03) * mm});
            skLineSegment(sketch, "E8.9.12.4", {"start": v(-184.05, 316.03) * mm, "end": v(-184.05, 313.5) * mm});
            skLineSegment(sketch, "E8.0.12.5", {"start": v(-186.6, 310.65) * mm, "end": v(-184.05, 310.65) * mm});
            skLineSegment(sketch, "E8.3.12.5", {"start": v(-186.6, 313.19) * mm, "end": v(-186.6, 310.65) * mm});
            skLineSegment(sketch, "E8.6.12.5", {"start": v(-186.6, 313.19) * mm, "end": v(-184.05, 313.19) * mm});
            skLineSegment(sketch, "E8.9.12.5", {"start": v(-184.05, 313.19) * mm, "end": v(-184.05, 310.65) * mm});
            skLineSegment(sketch, "E8.0.12.6", {"start": v(-186.6, 307.8) * mm, "end": v(-184.05, 307.8) * mm});
            skLineSegment(sketch, "E8.3.12.6", {"start": v(-186.6, 310.34) * mm, "end": v(-186.6, 307.8) * mm});
            skLineSegment(sketch, "E8.6.12.6", {"start": v(-186.6, 310.34) * mm, "end": v(-184.05, 310.34) * mm});
            skLineSegment(sketch, "E8.9.12.6", {"start": v(-184.05, 310.34) * mm, "end": v(-184.05, 307.8) * mm});
            skLineSegment(sketch, "E8.0.12.7", {"start": v(-186.6, 304.96) * mm, "end": v(-184.05, 304.96) * mm});
            skLineSegment(sketch, "E8.3.12.7", {"start": v(-186.6, 307.5) * mm, "end": v(-186.6, 304.96) * mm});
            skLineSegment(sketch, "E8.6.12.7", {"start": v(-186.6, 307.5) * mm, "end": v(-184.05, 307.5) * mm});
            skLineSegment(sketch, "E8.9.12.7", {"start": v(-184.05, 307.5) * mm, "end": v(-184.05, 304.96) * mm});
            skLineSegment(sketch, "E8.0.12.8", {"start": v(-186.6, 302.11) * mm, "end": v(-184.05, 302.11) * mm});
            skLineSegment(sketch, "E8.3.12.8", {"start": v(-186.6, 304.65) * mm, "end": v(-186.6, 302.11) * mm});
            skLineSegment(sketch, "E8.6.12.8", {"start": v(-186.6, 304.65) * mm, "end": v(-184.05, 304.65) * mm});
            skLineSegment(sketch, "E8.9.12.8", {"start": v(-184.05, 304.65) * mm, "end": v(-184.05, 302.11) * mm});
            skLineSegment(sketch, "E8.0.12.9", {"start": v(-186.6, 299.27) * mm, "end": v(-184.05, 299.27) * mm});
            skLineSegment(sketch, "E8.3.12.9", {"start": v(-186.6, 301.8) * mm, "end": v(-186.6, 299.27) * mm});
            skLineSegment(sketch, "E8.6.12.9", {"start": v(-186.6, 301.8) * mm, "end": v(-184.05, 301.8) * mm});
            skLineSegment(sketch, "E8.9.12.9", {"start": v(-184.05, 301.8) * mm, "end": v(-184.05, 299.27) * mm});
            skLineSegment(sketch, "E8.0.12.10", {"start": v(-186.6, 296.42) * mm, "end": v(-184.05, 296.42) * mm});
            skLineSegment(sketch, "E8.3.12.10", {"start": v(-186.6, 298.96) * mm, "end": v(-186.6, 296.42) * mm});
            skLineSegment(sketch, "E8.6.12.10", {"start": v(-186.6, 298.96) * mm, "end": v(-184.05, 298.96) * mm});
            skLineSegment(sketch, "E8.9.12.10", {"start": v(-184.05, 298.96) * mm, "end": v(-184.05, 296.42) * mm});
            skLineSegment(sketch, "E8.0.12.11", {"start": v(-186.6, 293.58) * mm, "end": v(-184.05, 293.58) * mm});
            skLineSegment(sketch, "E8.3.12.11", {"start": v(-186.6, 296.12) * mm, "end": v(-186.6, 293.58) * mm});
            skLineSegment(sketch, "E8.6.12.11", {"start": v(-186.6, 296.12) * mm, "end": v(-184.05, 296.12) * mm});
            skLineSegment(sketch, "E8.9.12.11", {"start": v(-184.05, 296.12) * mm, "end": v(-184.05, 293.58) * mm});
            skLineSegment(sketch, "E8.0.12.12", {"start": v(-186.6, 290.73) * mm, "end": v(-184.05, 290.73) * mm});
            skLineSegment(sketch, "E8.3.12.12", {"start": v(-186.6, 293.27) * mm, "end": v(-186.6, 290.73) * mm});
            skLineSegment(sketch, "E8.6.12.12", {"start": v(-186.6, 293.27) * mm, "end": v(-184.05, 293.27) * mm});
            skLineSegment(sketch, "E8.9.12.12", {"start": v(-184.05, 293.27) * mm, "end": v(-184.05, 290.73) * mm});
            skLineSegment(sketch, "E8.0.12.13", {"start": v(-186.6, 287.89) * mm, "end": v(-184.05, 287.89) * mm});
            skLineSegment(sketch, "E8.3.12.13", {"start": v(-186.6, 290.43) * mm, "end": v(-186.6, 287.89) * mm});
            skLineSegment(sketch, "E8.6.12.13", {"start": v(-186.6, 290.43) * mm, "end": v(-184.05, 290.43) * mm});
            skLineSegment(sketch, "E8.9.12.13", {"start": v(-184.05, 290.43) * mm, "end": v(-184.05, 287.89) * mm});
            skLineSegment(sketch, "E8.0.12.14", {"start": v(-186.6, 285.04) * mm, "end": v(-184.05, 285.04) * mm});
            skLineSegment(sketch, "E8.3.12.14", {"start": v(-186.6, 287.58) * mm, "end": v(-186.6, 285.04) * mm});
            skLineSegment(sketch, "E8.6.12.14", {"start": v(-186.6, 287.58) * mm, "end": v(-184.05, 287.58) * mm});
            skLineSegment(sketch, "E8.9.12.14", {"start": v(-184.05, 287.58) * mm, "end": v(-184.05, 285.04) * mm});
            skLineSegment(sketch, "E8.0.12.15", {"start": v(-186.6, 282.2) * mm, "end": v(-184.05, 282.2) * mm});
            skLineSegment(sketch, "E8.3.12.15", {"start": v(-186.6, 284.74) * mm, "end": v(-186.6, 282.2) * mm});
            skLineSegment(sketch, "E8.6.12.15", {"start": v(-186.6, 284.74) * mm, "end": v(-184.05, 284.74) * mm});
            skLineSegment(sketch, "E8.9.12.15", {"start": v(-184.05, 284.74) * mm, "end": v(-184.05, 282.2) * mm});
            skLineSegment(sketch, "E8.0.13.2", {"start": v(-183.75, 319.18) * mm, "end": v(-181.2, 319.18) * mm});
            skLineSegment(sketch, "E8.3.13.2", {"start": v(-183.75, 321.72) * mm, "end": v(-183.75, 319.18) * mm});
            skLineSegment(sketch, "E8.6.13.2", {"start": v(-183.75, 321.72) * mm, "end": v(-181.2, 321.72) * mm});
            skLineSegment(sketch, "E8.9.13.2", {"start": v(-181.2, 321.72) * mm, "end": v(-181.2, 319.18) * mm});
            skLineSegment(sketch, "E8.0.13.3", {"start": v(-183.75, 316.34) * mm, "end": v(-181.2, 316.34) * mm});
            skLineSegment(sketch, "E8.3.13.3", {"start": v(-183.75, 318.88) * mm, "end": v(-183.75, 316.34) * mm});
            skLineSegment(sketch, "E8.6.13.3", {"start": v(-183.75, 318.88) * mm, "end": v(-181.2, 318.88) * mm});
            skLineSegment(sketch, "E8.9.13.3", {"start": v(-181.2, 318.88) * mm, "end": v(-181.2, 316.34) * mm});
            skLineSegment(sketch, "E8.0.13.4", {"start": v(-183.75, 313.5) * mm, "end": v(-181.2, 313.5) * mm});
            skLineSegment(sketch, "E8.3.13.4", {"start": v(-183.75, 316.03) * mm, "end": v(-183.75, 313.5) * mm});
            skLineSegment(sketch, "E8.6.13.4", {"start": v(-183.75, 316.03) * mm, "end": v(-181.2, 316.03) * mm});
            skLineSegment(sketch, "E8.9.13.4", {"start": v(-181.2, 316.03) * mm, "end": v(-181.2, 313.5) * mm});
            skLineSegment(sketch, "E8.0.13.5", {"start": v(-183.75, 310.65) * mm, "end": v(-181.2, 310.65) * mm});
            skLineSegment(sketch, "E8.3.13.5", {"start": v(-183.75, 313.19) * mm, "end": v(-183.75, 310.65) * mm});
            skLineSegment(sketch, "E8.6.13.5", {"start": v(-183.75, 313.19) * mm, "end": v(-181.2, 313.19) * mm});
            skLineSegment(sketch, "E8.9.13.5", {"start": v(-181.2, 313.19) * mm, "end": v(-181.2, 310.65) * mm});
            skLineSegment(sketch, "E8.0.13.6", {"start": v(-183.75, 307.8) * mm, "end": v(-181.2, 307.8) * mm});
            skLineSegment(sketch, "E8.3.13.6", {"start": v(-183.75, 310.34) * mm, "end": v(-183.75, 307.8) * mm});
            skLineSegment(sketch, "E8.6.13.6", {"start": v(-183.75, 310.34) * mm, "end": v(-181.2, 310.34) * mm});
            skLineSegment(sketch, "E8.9.13.6", {"start": v(-181.2, 310.34) * mm, "end": v(-181.2, 307.8) * mm});
            skLineSegment(sketch, "E8.0.13.7", {"start": v(-183.75, 304.96) * mm, "end": v(-181.2, 304.96) * mm});
            skLineSegment(sketch, "E8.3.13.7", {"start": v(-183.75, 307.5) * mm, "end": v(-183.75, 304.96) * mm});
            skLineSegment(sketch, "E8.6.13.7", {"start": v(-183.75, 307.5) * mm, "end": v(-181.2, 307.5) * mm});
            skLineSegment(sketch, "E8.9.13.7", {"start": v(-181.2, 307.5) * mm, "end": v(-181.2, 304.96) * mm});
            skLineSegment(sketch, "E8.0.13.8", {"start": v(-183.75, 302.11) * mm, "end": v(-181.2, 302.11) * mm});
            skLineSegment(sketch, "E8.3.13.8", {"start": v(-183.75, 304.65) * mm, "end": v(-183.75, 302.11) * mm});
            skLineSegment(sketch, "E8.6.13.8", {"start": v(-183.75, 304.65) * mm, "end": v(-181.2, 304.65) * mm});
            skLineSegment(sketch, "E8.9.13.8", {"start": v(-181.2, 304.65) * mm, "end": v(-181.2, 302.11) * mm});
            skLineSegment(sketch, "E8.0.13.9", {"start": v(-183.75, 299.27) * mm, "end": v(-181.2, 299.27) * mm});
            skLineSegment(sketch, "E8.3.13.9", {"start": v(-183.75, 301.8) * mm, "end": v(-183.75, 299.27) * mm});
            skLineSegment(sketch, "E8.6.13.9", {"start": v(-183.75, 301.8) * mm, "end": v(-181.2, 301.8) * mm});
            skLineSegment(sketch, "E8.9.13.9", {"start": v(-181.2, 301.8) * mm, "end": v(-181.2, 299.27) * mm});
            skLineSegment(sketch, "E8.0.13.10", {"start": v(-183.75, 296.42) * mm, "end": v(-181.2, 296.42) * mm});
            skLineSegment(sketch, "E8.3.13.10", {"start": v(-183.75, 298.96) * mm, "end": v(-183.75, 296.42) * mm});
            skLineSegment(sketch, "E8.6.13.10", {"start": v(-183.75, 298.96) * mm, "end": v(-181.2, 298.96) * mm});
            skLineSegment(sketch, "E8.9.13.10", {"start": v(-181.2, 298.96) * mm, "end": v(-181.2, 296.42) * mm});
            skLineSegment(sketch, "E8.0.13.11", {"start": v(-183.75, 293.58) * mm, "end": v(-181.2, 293.58) * mm});
            skLineSegment(sketch, "E8.3.13.11", {"start": v(-183.75, 296.12) * mm, "end": v(-183.75, 293.58) * mm});
            skLineSegment(sketch, "E8.6.13.11", {"start": v(-183.75, 296.12) * mm, "end": v(-181.2, 296.12) * mm});
            skLineSegment(sketch, "E8.9.13.11", {"start": v(-181.2, 296.12) * mm, "end": v(-181.2, 293.58) * mm});
            skLineSegment(sketch, "E8.0.13.12", {"start": v(-183.75, 290.73) * mm, "end": v(-181.2, 290.73) * mm});
            skLineSegment(sketch, "E8.3.13.12", {"start": v(-183.75, 293.27) * mm, "end": v(-183.75, 290.73) * mm});
            skLineSegment(sketch, "E8.6.13.12", {"start": v(-183.75, 293.27) * mm, "end": v(-181.2, 293.27) * mm});
            skLineSegment(sketch, "E8.9.13.12", {"start": v(-181.2, 293.27) * mm, "end": v(-181.2, 290.73) * mm});
            skLineSegment(sketch, "E8.0.13.13", {"start": v(-183.75, 287.89) * mm, "end": v(-181.2, 287.89) * mm});
            skLineSegment(sketch, "E8.3.13.13", {"start": v(-183.75, 290.43) * mm, "end": v(-183.75, 287.89) * mm});
            skLineSegment(sketch, "E8.6.13.13", {"start": v(-183.75, 290.43) * mm, "end": v(-181.2, 290.43) * mm});
            skLineSegment(sketch, "E8.9.13.13", {"start": v(-181.2, 290.43) * mm, "end": v(-181.2, 287.89) * mm});
            skLineSegment(sketch, "E8.0.13.14", {"start": v(-183.75, 285.04) * mm, "end": v(-181.2, 285.04) * mm});
            skLineSegment(sketch, "E8.3.13.14", {"start": v(-183.75, 287.58) * mm, "end": v(-183.75, 285.04) * mm});
            skLineSegment(sketch, "E8.6.13.14", {"start": v(-183.75, 287.58) * mm, "end": v(-181.2, 287.58) * mm});
            skLineSegment(sketch, "E8.9.13.14", {"start": v(-181.2, 287.58) * mm, "end": v(-181.2, 285.04) * mm});
            skLineSegment(sketch, "E8.0.13.15", {"start": v(-183.75, 282.2) * mm, "end": v(-181.2, 282.2) * mm});
            skLineSegment(sketch, "E8.3.13.15", {"start": v(-183.75, 284.74) * mm, "end": v(-183.75, 282.2) * mm});
            skLineSegment(sketch, "E8.6.13.15", {"start": v(-183.75, 284.74) * mm, "end": v(-181.2, 284.74) * mm});
            skLineSegment(sketch, "E8.9.13.15", {"start": v(-181.2, 284.74) * mm, "end": v(-181.2, 282.2) * mm});
            skLineSegment(sketch, "E8.0.14.2", {"start": v(-180.9, 319.18) * mm, "end": v(-178.36, 319.18) * mm});
            skLineSegment(sketch, "E8.3.14.2", {"start": v(-180.9, 321.72) * mm, "end": v(-180.9, 319.18) * mm});
            skLineSegment(sketch, "E8.6.14.2", {"start": v(-180.9, 321.72) * mm, "end": v(-178.36, 321.72) * mm});
            skLineSegment(sketch, "E8.9.14.2", {"start": v(-178.36, 321.72) * mm, "end": v(-178.36, 319.18) * mm});
            skLineSegment(sketch, "E8.0.14.3", {"start": v(-180.9, 316.34) * mm, "end": v(-178.36, 316.34) * mm});
            skLineSegment(sketch, "E8.3.14.3", {"start": v(-180.9, 318.88) * mm, "end": v(-180.9, 316.34) * mm});
            skLineSegment(sketch, "E8.6.14.3", {"start": v(-180.9, 318.88) * mm, "end": v(-178.36, 318.88) * mm});
            skLineSegment(sketch, "E8.9.14.3", {"start": v(-178.36, 318.88) * mm, "end": v(-178.36, 316.34) * mm});
            skLineSegment(sketch, "E8.0.14.4", {"start": v(-180.9, 313.5) * mm, "end": v(-178.36, 313.5) * mm});
            skLineSegment(sketch, "E8.3.14.4", {"start": v(-180.9, 316.03) * mm, "end": v(-180.9, 313.5) * mm});
            skLineSegment(sketch, "E8.6.14.4", {"start": v(-180.9, 316.03) * mm, "end": v(-178.36, 316.03) * mm});
            skLineSegment(sketch, "E8.9.14.4", {"start": v(-178.36, 316.03) * mm, "end": v(-178.36, 313.5) * mm});
            skLineSegment(sketch, "E8.0.14.5", {"start": v(-180.9, 310.65) * mm, "end": v(-178.36, 310.65) * mm});
            skLineSegment(sketch, "E8.3.14.5", {"start": v(-180.9, 313.19) * mm, "end": v(-180.9, 310.65) * mm});
            skLineSegment(sketch, "E8.6.14.5", {"start": v(-180.9, 313.19) * mm, "end": v(-178.36, 313.19) * mm});
            skLineSegment(sketch, "E8.9.14.5", {"start": v(-178.36, 313.19) * mm, "end": v(-178.36, 310.65) * mm});
            skLineSegment(sketch, "E8.0.14.6", {"start": v(-180.9, 307.8) * mm, "end": v(-178.36, 307.8) * mm});
            skLineSegment(sketch, "E8.3.14.6", {"start": v(-180.9, 310.34) * mm, "end": v(-180.9, 307.8) * mm});
            skLineSegment(sketch, "E8.6.14.6", {"start": v(-180.9, 310.34) * mm, "end": v(-178.36, 310.34) * mm});
            skLineSegment(sketch, "E8.9.14.6", {"start": v(-178.36, 310.34) * mm, "end": v(-178.36, 307.8) * mm});
            skLineSegment(sketch, "E8.0.14.7", {"start": v(-180.9, 304.96) * mm, "end": v(-178.36, 304.96) * mm});
            skLineSegment(sketch, "E8.3.14.7", {"start": v(-180.9, 307.5) * mm, "end": v(-180.9, 304.96) * mm});
            skLineSegment(sketch, "E8.6.14.7", {"start": v(-180.9, 307.5) * mm, "end": v(-178.36, 307.5) * mm});
            skLineSegment(sketch, "E8.9.14.7", {"start": v(-178.36, 307.5) * mm, "end": v(-178.36, 304.96) * mm});
            skLineSegment(sketch, "E8.0.14.8", {"start": v(-180.9, 302.11) * mm, "end": v(-178.36, 302.11) * mm});
            skLineSegment(sketch, "E8.3.14.8", {"start": v(-180.9, 304.65) * mm, "end": v(-180.9, 302.11) * mm});
            skLineSegment(sketch, "E8.6.14.8", {"start": v(-180.9, 304.65) * mm, "end": v(-178.36, 304.65) * mm});
            skLineSegment(sketch, "E8.9.14.8", {"start": v(-178.36, 304.65) * mm, "end": v(-178.36, 302.11) * mm});
            skLineSegment(sketch, "E8.0.14.9", {"start": v(-180.9, 299.27) * mm, "end": v(-178.36, 299.27) * mm});
            skLineSegment(sketch, "E8.3.14.9", {"start": v(-180.9, 301.8) * mm, "end": v(-180.9, 299.27) * mm});
            skLineSegment(sketch, "E8.6.14.9", {"start": v(-180.9, 301.8) * mm, "end": v(-178.36, 301.8) * mm});
            skLineSegment(sketch, "E8.9.14.9", {"start": v(-178.36, 301.8) * mm, "end": v(-178.36, 299.27) * mm});
            skLineSegment(sketch, "E8.0.14.10", {"start": v(-180.9, 296.42) * mm, "end": v(-178.36, 296.42) * mm});
            skLineSegment(sketch, "E8.3.14.10", {"start": v(-180.9, 298.96) * mm, "end": v(-180.9, 296.42) * mm});
            skLineSegment(sketch, "E8.6.14.10", {"start": v(-180.9, 298.96) * mm, "end": v(-178.36, 298.96) * mm});
            skLineSegment(sketch, "E8.9.14.10", {"start": v(-178.36, 298.96) * mm, "end": v(-178.36, 296.42) * mm});
            skLineSegment(sketch, "E8.0.14.11", {"start": v(-180.9, 293.58) * mm, "end": v(-178.36, 293.58) * mm});
            skLineSegment(sketch, "E8.3.14.11", {"start": v(-180.9, 296.12) * mm, "end": v(-180.9, 293.58) * mm});
            skLineSegment(sketch, "E8.6.14.11", {"start": v(-180.9, 296.12) * mm, "end": v(-178.36, 296.12) * mm});
            skLineSegment(sketch, "E8.9.14.11", {"start": v(-178.36, 296.12) * mm, "end": v(-178.36, 293.58) * mm});
            skLineSegment(sketch, "E8.0.14.12", {"start": v(-180.9, 290.73) * mm, "end": v(-178.36, 290.73) * mm});
            skLineSegment(sketch, "E8.3.14.12", {"start": v(-180.9, 293.27) * mm, "end": v(-180.9, 290.73) * mm});
            skLineSegment(sketch, "E8.6.14.12", {"start": v(-180.9, 293.27) * mm, "end": v(-178.36, 293.27) * mm});
            skLineSegment(sketch, "E8.9.14.12", {"start": v(-178.36, 293.27) * mm, "end": v(-178.36, 290.73) * mm});
            skLineSegment(sketch, "E8.0.14.13", {"start": v(-180.9, 287.89) * mm, "end": v(-178.36, 287.89) * mm});
            skLineSegment(sketch, "E8.3.14.13", {"start": v(-180.9, 290.43) * mm, "end": v(-180.9, 287.89) * mm});
            skLineSegment(sketch, "E8.6.14.13", {"start": v(-180.9, 290.43) * mm, "end": v(-178.36, 290.43) * mm});
            skLineSegment(sketch, "E8.9.14.13", {"start": v(-178.36, 290.43) * mm, "end": v(-178.36, 287.89) * mm});
            skLineSegment(sketch, "E8.0.14.14", {"start": v(-180.9, 285.04) * mm, "end": v(-178.36, 285.04) * mm});
            skLineSegment(sketch, "E8.3.14.14", {"start": v(-180.9, 287.58) * mm, "end": v(-180.9, 285.04) * mm});
            skLineSegment(sketch, "E8.6.14.14", {"start": v(-180.9, 287.58) * mm, "end": v(-178.36, 287.58) * mm});
            skLineSegment(sketch, "E8.9.14.14", {"start": v(-178.36, 287.58) * mm, "end": v(-178.36, 285.04) * mm});
            skLineSegment(sketch, "E8.0.14.15", {"start": v(-180.9, 282.2) * mm, "end": v(-178.36, 282.2) * mm});
            skLineSegment(sketch, "E8.3.14.15", {"start": v(-180.9, 284.74) * mm, "end": v(-180.9, 282.2) * mm});
            skLineSegment(sketch, "E8.6.14.15", {"start": v(-180.9, 284.74) * mm, "end": v(-178.36, 284.74) * mm});
            skLineSegment(sketch, "E8.9.14.15", {"start": v(-178.36, 284.74) * mm, "end": v(-178.36, 282.2) * mm});
            skLineSegment(sketch, "E8.0.15.2", {"start": v(-178.06, 319.18) * mm, "end": v(-175.52, 319.18) * mm});
            skLineSegment(sketch, "E8.3.15.2", {"start": v(-178.06, 321.72) * mm, "end": v(-178.06, 319.18) * mm});
            skLineSegment(sketch, "E8.6.15.2", {"start": v(-178.06, 321.72) * mm, "end": v(-175.52, 321.72) * mm});
            skLineSegment(sketch, "E8.9.15.2", {"start": v(-175.52, 321.72) * mm, "end": v(-175.52, 319.18) * mm});
            skLineSegment(sketch, "E8.0.15.3", {"start": v(-178.06, 316.34) * mm, "end": v(-175.52, 316.34) * mm});
            skLineSegment(sketch, "E8.3.15.3", {"start": v(-178.06, 318.88) * mm, "end": v(-178.06, 316.34) * mm});
            skLineSegment(sketch, "E8.6.15.3", {"start": v(-178.06, 318.88) * mm, "end": v(-175.52, 318.88) * mm});
            skLineSegment(sketch, "E8.9.15.3", {"start": v(-175.52, 318.88) * mm, "end": v(-175.52, 316.34) * mm});
            skLineSegment(sketch, "E8.0.15.4", {"start": v(-178.06, 313.5) * mm, "end": v(-175.52, 313.5) * mm});
            skLineSegment(sketch, "E8.3.15.4", {"start": v(-178.06, 316.03) * mm, "end": v(-178.06, 313.5) * mm});
            skLineSegment(sketch, "E8.6.15.4", {"start": v(-178.06, 316.03) * mm, "end": v(-175.52, 316.03) * mm});
            skLineSegment(sketch, "E8.9.15.4", {"start": v(-175.52, 316.03) * mm, "end": v(-175.52, 313.5) * mm});
            skLineSegment(sketch, "E8.0.15.5", {"start": v(-178.06, 310.65) * mm, "end": v(-175.52, 310.65) * mm});
            skLineSegment(sketch, "E8.3.15.5", {"start": v(-178.06, 313.19) * mm, "end": v(-178.06, 310.65) * mm});
            skLineSegment(sketch, "E8.6.15.5", {"start": v(-178.06, 313.19) * mm, "end": v(-175.52, 313.19) * mm});
            skLineSegment(sketch, "E8.9.15.5", {"start": v(-175.52, 313.19) * mm, "end": v(-175.52, 310.65) * mm});
            skLineSegment(sketch, "E8.0.15.6", {"start": v(-178.06, 307.8) * mm, "end": v(-175.52, 307.8) * mm});
            skLineSegment(sketch, "E8.3.15.6", {"start": v(-178.06, 310.34) * mm, "end": v(-178.06, 307.8) * mm});
            skLineSegment(sketch, "E8.6.15.6", {"start": v(-178.06, 310.34) * mm, "end": v(-175.52, 310.34) * mm});
            skLineSegment(sketch, "E8.9.15.6", {"start": v(-175.52, 310.34) * mm, "end": v(-175.52, 307.8) * mm});
            skLineSegment(sketch, "E8.0.15.7", {"start": v(-178.06, 304.96) * mm, "end": v(-175.52, 304.96) * mm});
            skLineSegment(sketch, "E8.3.15.7", {"start": v(-178.06, 307.5) * mm, "end": v(-178.06, 304.96) * mm});
            skLineSegment(sketch, "E8.6.15.7", {"start": v(-178.06, 307.5) * mm, "end": v(-175.52, 307.5) * mm});
            skLineSegment(sketch, "E8.9.15.7", {"start": v(-175.52, 307.5) * mm, "end": v(-175.52, 304.96) * mm});
            skLineSegment(sketch, "E8.0.15.8", {"start": v(-178.06, 302.11) * mm, "end": v(-175.52, 302.11) * mm});
            skLineSegment(sketch, "E8.3.15.8", {"start": v(-178.06, 304.65) * mm, "end": v(-178.06, 302.11) * mm});
            skLineSegment(sketch, "E8.6.15.8", {"start": v(-178.06, 304.65) * mm, "end": v(-175.52, 304.65) * mm});
            skLineSegment(sketch, "E8.9.15.8", {"start": v(-175.52, 304.65) * mm, "end": v(-175.52, 302.11) * mm});
            skLineSegment(sketch, "E8.0.15.9", {"start": v(-178.06, 299.27) * mm, "end": v(-175.52, 299.27) * mm});
            skLineSegment(sketch, "E8.3.15.9", {"start": v(-178.06, 301.8) * mm, "end": v(-178.06, 299.27) * mm});
            skLineSegment(sketch, "E8.6.15.9", {"start": v(-178.06, 301.8) * mm, "end": v(-175.52, 301.8) * mm});
            skLineSegment(sketch, "E8.9.15.9", {"start": v(-175.52, 301.8) * mm, "end": v(-175.52, 299.27) * mm});
            skLineSegment(sketch, "E8.0.15.10", {"start": v(-178.06, 296.42) * mm, "end": v(-175.52, 296.42) * mm});
            skLineSegment(sketch, "E8.3.15.10", {"start": v(-178.06, 298.96) * mm, "end": v(-178.06, 296.42) * mm});
            skLineSegment(sketch, "E8.6.15.10", {"start": v(-178.06, 298.96) * mm, "end": v(-175.52, 298.96) * mm});
            skLineSegment(sketch, "E8.9.15.10", {"start": v(-175.52, 298.96) * mm, "end": v(-175.52, 296.42) * mm});
            skLineSegment(sketch, "E8.0.15.11", {"start": v(-178.06, 293.58) * mm, "end": v(-175.52, 293.58) * mm});
            skLineSegment(sketch, "E8.3.15.11", {"start": v(-178.06, 296.12) * mm, "end": v(-178.06, 293.58) * mm});
            skLineSegment(sketch, "E8.6.15.11", {"start": v(-178.06, 296.12) * mm, "end": v(-175.52, 296.12) * mm});
            skLineSegment(sketch, "E8.9.15.11", {"start": v(-175.52, 296.12) * mm, "end": v(-175.52, 293.58) * mm});
            skLineSegment(sketch, "E8.0.15.12", {"start": v(-178.06, 290.73) * mm, "end": v(-175.52, 290.73) * mm});
            skLineSegment(sketch, "E8.3.15.12", {"start": v(-178.06, 293.27) * mm, "end": v(-178.06, 290.73) * mm});
            skLineSegment(sketch, "E8.6.15.12", {"start": v(-178.06, 293.27) * mm, "end": v(-175.52, 293.27) * mm});
            skLineSegment(sketch, "E8.9.15.12", {"start": v(-175.52, 293.27) * mm, "end": v(-175.52, 290.73) * mm});
            skLineSegment(sketch, "E8.0.15.13", {"start": v(-178.06, 287.89) * mm, "end": v(-175.52, 287.89) * mm});
            skLineSegment(sketch, "E8.3.15.13", {"start": v(-178.06, 290.43) * mm, "end": v(-178.06, 287.89) * mm});
            skLineSegment(sketch, "E8.6.15.13", {"start": v(-178.06, 290.43) * mm, "end": v(-175.52, 290.43) * mm});
            skLineSegment(sketch, "E8.9.15.13", {"start": v(-175.52, 290.43) * mm, "end": v(-175.52, 287.89) * mm});
            skLineSegment(sketch, "E8.0.15.14", {"start": v(-178.06, 285.04) * mm, "end": v(-175.52, 285.04) * mm});
            skLineSegment(sketch, "E8.3.15.14", {"start": v(-178.06, 287.58) * mm, "end": v(-178.06, 285.04) * mm});
            skLineSegment(sketch, "E8.6.15.14", {"start": v(-178.06, 287.58) * mm, "end": v(-175.52, 287.58) * mm});
            skLineSegment(sketch, "E8.9.15.14", {"start": v(-175.52, 287.58) * mm, "end": v(-175.52, 285.04) * mm});
            skLineSegment(sketch, "E8.0.15.15", {"start": v(-178.06, 282.2) * mm, "end": v(-175.52, 282.2) * mm});
            skLineSegment(sketch, "E8.3.15.15", {"start": v(-178.06, 284.74) * mm, "end": v(-178.06, 282.2) * mm});
            skLineSegment(sketch, "E8.6.15.15", {"start": v(-178.06, 284.74) * mm, "end": v(-175.52, 284.74) * mm});
            skLineSegment(sketch, "E8.9.15.15", {"start": v(-175.52, 284.74) * mm, "end": v(-175.52, 282.2) * mm});
            skCircle(sketch, "E9", {"center": v(-198.12, 304.8) * mm, "radius": 3.37 * mm});
            skSolve(sketch);
        }
        {
            var Q0;
            Q0=makeQuery(id+"F4.imprint","IMPRINT",FACE,{"disambiguationData":[TD([[makeQuery(id+"F4.imprint","IMPRINT",EDGE,{"derivedFrom":sQuery(id+"F4.wireOp",EDGE,"E8.0.12.8")}),1.0]])]});
            var Q1;
            Q1=makeQuery(id+"F4.imprint","IMPRINT",FACE,{"disambiguationData":[TD([[makeQuery(id+"F4.imprint","IMPRINT",EDGE,{"derivedFrom":sQuery(id+"F4.wireOp",EDGE,"E8.0.11.6")}),1.0]])]});
            var Q2;
            Q2=makeQuery(id+"F4.imprint","IMPRINT",FACE,{"disambiguationData":[TD([[makeQuery(id+"F4.imprint","IMPRINT",EDGE,{"derivedFrom":sQuery(id+"F4.wireOp",EDGE,"E8.0.10.4")}),1.0]])]});
            var Q3;
            Q3=makeQuery(id+"F4.imprint","IMPRINT",FACE,{"disambiguationData":[TD([[makeQuery(id+"F4.imprint","IMPRINT",EDGE,{"derivedFrom":sQuery(id+"F4.wireOp",EDGE,"E8.0.8.14")}),1.0]])]});
            var Q4;
            {var subQ1=sQuery(id+"F4.wireOp",EDGE,"E8.3.7.6");Q4=makeQuery(id+"F4.imprint","IMPRINT",FACE,{"disambiguationData":[TD([[makeQuery(id+"F4.imprint","IMPRINT",EDGE,{"derivedFrom":subQ1}),1.0]])]});}
            var Q5;
            Q5=makeQuery(id+"F4.imprint","IMPRINT",FACE,{"disambiguationData":[TD([[makeQuery(id+"F4.imprint","IMPRINT",EDGE,{"derivedFrom":sQuery(id+"F4.wireOp",EDGE,"E8.0.15.14")}),1.0]])]});
            var Q6;
            Q6=makeQuery(id+"F4.imprint","IMPRINT",FACE,{"disambiguationData":[TD([[makeQuery(id+"F4.imprint","IMPRINT",EDGE,{"derivedFrom":sQuery(id+"F4.wireOp",EDGE,"E8.0.14.12")}),1.0]])]});
            var Q7;
            Q7=makeQuery(id+"F4.imprint","IMPRINT",FACE,{"disambiguationData":[TD([[makeQuery(id+"F4.imprint","IMPRINT",EDGE,{"derivedFrom":sQuery(id+"F4.wireOp",EDGE,"E8.0.13.10")}),1.0]])]});
            var Q8;
            Q8=makeQuery(id+"F4.imprint","IMPRINT",FACE,{"disambiguationData":[TD([[makeQuery(id+"F4.imprint","IMPRINT",EDGE,{"derivedFrom":sQuery(id+"F4.wireOp",EDGE,"E8.0.15.15")}),1.0]])]});
            var Q9;
            Q9=makeQuery(id+"F4.imprint","IMPRINT",FACE,{"disambiguationData":[TD([[makeQuery(id+"F4.imprint","IMPRINT",EDGE,{"derivedFrom":sQuery(id+"F4.wireOp",EDGE,"E8.0.14.13")}),1.0]])]});
            var Q10;
            Q10=makeQuery(id+"F4.imprint","IMPRINT",FACE,{"disambiguationData":[TD([[makeQuery(id+"F4.imprint","IMPRINT",EDGE,{"derivedFrom":sQuery(id+"F4.wireOp",EDGE,"E8.0.13.11")}),1.0]])]});
            var Q11;
            Q11=makeQuery(id+"F4.imprint","IMPRINT",FACE,{"disambiguationData":[TD([[makeQuery(id+"F4.imprint","IMPRINT",EDGE,{"derivedFrom":sQuery(id+"F4.wireOp",EDGE,"E8.0.1.8")}),1.0]])]});
            var Q12;
            Q12=makeQuery(id+"F4.imprint","IMPRINT",FACE,{"disambiguationData":[TD([[makeQuery(id+"F4.imprint","IMPRINT",EDGE,{"derivedFrom":sQuery(id+"F4.wireOp",EDGE,"E8.0.2.10")}),1.0]])]});
            var Q13;
            Q13=makeQuery(id+"F4.imprint","IMPRINT",FACE,{"disambiguationData":[TD([[makeQuery(id+"F4.imprint","IMPRINT",EDGE,{"derivedFrom":sQuery(id+"F4.wireOp",EDGE,"E8.0.0.6")}),1.0]])]});
            var Q14;
            Q14=makeQuery(id+"F4.imprint","IMPRINT",FACE,{"disambiguationData":[TD([[makeQuery(id+"F4.imprint","IMPRINT",EDGE,{"derivedFrom":sQuery(id+"F4.wireOp",EDGE,"E7.10.0.0")}),1.0]])]});
            var Q15;
            Q15=makeQuery(id+"F4.imprint","IMPRINT",FACE,{"disambiguationData":[TD([[makeQuery(id+"F4.imprint","IMPRINT",EDGE,{"derivedFrom":sQuery(id+"F4.wireOp",EDGE,"E8.0.7.10")}),1.0]])]});
            var Q16;
            Q16=makeQuery(id+"F4.imprint","IMPRINT",FACE,{"disambiguationData":[TD([[makeQuery(id+"F4.imprint","IMPRINT",EDGE,{"derivedFrom":sQuery(id+"F4.wireOp",EDGE,"E8.0.6.2")}),1.0]])]});
            var Q17;
            Q17=makeQuery(id+"F4.imprint","IMPRINT",FACE,{"disambiguationData":[TD([[makeQuery(id+"F4.imprint","IMPRINT",EDGE,{"derivedFrom":sQuery(id+"F4.wireOp",EDGE,"E8.0.4.14")}),1.0]])]});
            var Q18;
            Q18=makeQuery(id+"F4.imprint","IMPRINT",FACE,{"disambiguationData":[TD([[makeQuery(id+"F4.imprint","IMPRINT",EDGE,{"derivedFrom":sQuery(id+"F4.wireOp",EDGE,"E8.0.3.12")}),1.0]])]});
            var Q19;
            Q19=makeQuery(id+"F4.imprint","IMPRINT",FACE,{"disambiguationData":[TD([[makeQuery(id+"F4.imprint","IMPRINT",EDGE,{"derivedFrom":sQuery(id+"F4.wireOp",EDGE,"E8.0.12.10")}),1.0]])]});
            var Q20;
            Q20=makeQuery(id+"F4.imprint","IMPRINT",FACE,{"disambiguationData":[TD([[makeQuery(id+"F4.imprint","IMPRINT",EDGE,{"derivedFrom":sQuery(id+"F4.wireOp",EDGE,"E8.0.11.8")}),1.0]])]});
            var Q21;
            Q21=makeQuery(id+"F4.imprint","IMPRINT",FACE,{"disambiguationData":[TD([[makeQuery(id+"F4.imprint","IMPRINT",EDGE,{"derivedFrom":sQuery(id+"F4.wireOp",EDGE,"E8.0.10.6")}),1.0]])]});
            var Q22;
            Q22=makeQuery(id+"F4.imprint","IMPRINT",FACE,{"disambiguationData":[TD([[makeQuery(id+"F4.imprint","IMPRINT",EDGE,{"derivedFrom":sQuery(id+"F4.wireOp",EDGE,"E8.0.9.2")}),1.0]])]});
            var Q23;
            Q23=makeQuery(id+"F4.imprint","IMPRINT",FACE,{"disambiguationData":[TD([[makeQuery(id+"F4.imprint","IMPRINT",EDGE,{"derivedFrom":sQuery(id+"F4.wireOp",EDGE,"E8.0.14.14")}),1.0]])]});
            var Q24;
            Q24=makeQuery(id+"F4.imprint","IMPRINT",FACE,{"disambiguationData":[TD([[makeQuery(id+"F4.imprint","IMPRINT",EDGE,{"derivedFrom":sQuery(id+"F4.wireOp",EDGE,"E8.0.13.12")}),1.0]])]});
            var Q25;
            Q25=makeQuery(id+"F4.imprint","IMPRINT",FACE,{"disambiguationData":[TD([[makeQuery(id+"F4.imprint","IMPRINT",EDGE,{"derivedFrom":sQuery(id+"F4.wireOp",EDGE,"E8.0.2.11")}),1.0]])]});
            var Q26;
            Q26=makeQuery(id+"F4.imprint","IMPRINT",FACE,{"disambiguationData":[TD([[makeQuery(id+"F4.imprint","IMPRINT",EDGE,{"derivedFrom":sQuery(id+"F4.wireOp",EDGE,"E8.0.1.9")}),1.0]])]});
            var Q27;
            Q27=makeQuery(id+"F4.imprint","IMPRINT",FACE,{"disambiguationData":[TD([[makeQuery(id+"F4.imprint","IMPRINT",EDGE,{"derivedFrom":sQuery(id+"F4.wireOp",EDGE,"E8.0.0.7")}),1.0]])]});
            var Q28;
            Q28=makeQuery(id+"F4.imprint","IMPRINT",FACE,{"disambiguationData":[TD([[makeQuery(id+"F4.imprint","IMPRINT",EDGE,{"derivedFrom":sQuery(id+"F4.wireOp",EDGE,"E7.10.1.0")}),1.0]])]});
            var Q29;
            Q29=makeQuery(id+"F4.imprint","IMPRINT",FACE,{"disambiguationData":[TD([[makeQuery(id+"F4.imprint","IMPRINT",EDGE,{"derivedFrom":sQuery(id+"F4.wireOp",EDGE,"E8.0.7.11")}),1.0]])]});
            var Q30;
            Q30=makeQuery(id+"F4.imprint","IMPRINT",FACE,{"disambiguationData":[TD([[makeQuery(id+"F4.imprint","IMPRINT",EDGE,{"derivedFrom":sQuery(id+"F4.wireOp",EDGE,"E8.0.6.3")}),1.0]])]});
            var Q31;
            Q31=makeQuery(id+"F4.imprint","IMPRINT",FACE,{"disambiguationData":[TD([[makeQuery(id+"F4.imprint","IMPRINT",EDGE,{"derivedFrom":sQuery(id+"F4.wireOp",EDGE,"E8.0.4.15")}),1.0]])]});
            var Q32;
            Q32=makeQuery(id+"F4.imprint","IMPRINT",FACE,{"disambiguationData":[TD([[makeQuery(id+"F4.imprint","IMPRINT",EDGE,{"derivedFrom":sQuery(id+"F4.wireOp",EDGE,"E8.0.3.13")}),1.0]])]});
            var Q33;
            Q33=makeQuery(id+"F4.imprint","IMPRINT",FACE,{"disambiguationData":[TD([[makeQuery(id+"F4.imprint","IMPRINT",EDGE,{"derivedFrom":sQuery(id+"F4.wireOp",EDGE,"E8.0.12.11")}),1.0]])]});
            var Q34;
            Q34=makeQuery(id+"F4.imprint","IMPRINT",FACE,{"disambiguationData":[TD([[makeQuery(id+"F4.imprint","IMPRINT",EDGE,{"derivedFrom":sQuery(id+"F4.wireOp",EDGE,"E8.0.11.9")}),1.0]])]});
            var Q35;
            Q35=makeQuery(id+"F4.imprint","IMPRINT",FACE,{"disambiguationData":[TD([[makeQuery(id+"F4.imprint","IMPRINT",EDGE,{"derivedFrom":sQuery(id+"F4.wireOp",EDGE,"E8.0.10.7")}),1.0]])]});
            var Q36;
            Q36=makeQuery(id+"F4.imprint","IMPRINT",FACE,{"disambiguationData":[TD([[makeQuery(id+"F4.imprint","IMPRINT",EDGE,{"derivedFrom":sQuery(id+"F4.wireOp",EDGE,"E8.0.9.3")}),1.0]])]});
            var Q37;
            {var subQ1=sQuery(id+"F4.wireOp",EDGE,"E8.0.7.9");Q37=makeQuery(id+"F4.imprint","IMPRINT",FACE,{"disambiguationData":[TD([[makeQuery(id+"F4.imprint","IMPRINT",EDGE,{"derivedFrom":subQ1}),1.0]])]});}
            var Q38;
            {var subQ4=sQuery(id+"F4.wireOp",EDGE,"E8.0.8.7");Q38=makeQuery(id+"F4.imprint","IMPRINT",FACE,{"disambiguationData":[TD([[makeQuery(id+"F4.imprint","IMPRINT",EDGE,{"derivedFrom":subQ4}),1.0]])]});}
            var Q39;
            Q39=makeQuery(id+"F4.imprint","IMPRINT",FACE,{"disambiguationData":[TD([[makeQuery(id+"F4.imprint","IMPRINT",EDGE,{"derivedFrom":sQuery(id+"F4.wireOp",EDGE,"E8.0.14.15")}),1.0]])]});
            var Q40;
            Q40=makeQuery(id+"F4.imprint","IMPRINT",FACE,{"disambiguationData":[TD([[makeQuery(id+"F4.imprint","IMPRINT",EDGE,{"derivedFrom":sQuery(id+"F4.wireOp",EDGE,"E8.0.13.13")}),1.0]])]});
            var Q41;
            Q41=makeQuery(id+"F4.imprint","IMPRINT",FACE,{"disambiguationData":[TD([[makeQuery(id+"F4.imprint","IMPRINT",EDGE,{"derivedFrom":sQuery(id+"F4.wireOp",EDGE,"E8.0.2.9")}),1.0]])]});
            var Q42;
            Q42=makeQuery(id+"F4.imprint","IMPRINT",FACE,{"disambiguationData":[TD([[makeQuery(id+"F4.imprint","IMPRINT",EDGE,{"derivedFrom":sQuery(id+"F4.wireOp",EDGE,"E8.0.1.7")}),1.0]])]});
            var Q43;
            Q43=makeQuery(id+"F4.imprint","IMPRINT",FACE,{"disambiguationData":[TD([[makeQuery(id+"F4.imprint","IMPRINT",EDGE,{"derivedFrom":sQuery(id+"F4.wireOp",EDGE,"E8.0.0.5")}),1.0]])]});
            var Q44;
            Q44=makeQuery(id+"F4.imprint","IMPRINT",FACE,{"disambiguationData":[TD([[makeQuery(id+"F4.imprint","IMPRINT",EDGE,{"derivedFrom":sQuery(id+"F4.wireOp",EDGE,"E7.9.1.0")}),1.0]])]});
            var Q45;
            Q45=makeQuery(id+"F4.imprint","IMPRINT",FACE,{"disambiguationData":[TD([[makeQuery(id+"F4.imprint","IMPRINT",EDGE,{"derivedFrom":sQuery(id+"F4.wireOp",EDGE,"E8.0.7.5")}),1.0]])]});
            var Q46;
            Q46=makeQuery(id+"F4.imprint","IMPRINT",FACE,{"disambiguationData":[TD([[makeQuery(id+"F4.imprint","IMPRINT",EDGE,{"derivedFrom":sQuery(id+"F4.wireOp",EDGE,"E8.0.5.15")}),1.0]])]});
            var Q47;
            Q47=makeQuery(id+"F4.imprint","IMPRINT",FACE,{"disambiguationData":[TD([[makeQuery(id+"F4.imprint","IMPRINT",EDGE,{"derivedFrom":sQuery(id+"F4.wireOp",EDGE,"E8.0.4.13")}),1.0]])]});
            var Q48;
            Q48=makeQuery(id+"F4.imprint","IMPRINT",FACE,{"disambiguationData":[TD([[makeQuery(id+"F4.imprint","IMPRINT",EDGE,{"derivedFrom":sQuery(id+"F4.wireOp",EDGE,"E8.0.3.11")}),1.0]])]});
            var Q49;
            Q49=makeQuery(id+"F4.imprint","IMPRINT",FACE,{"disambiguationData":[TD([[makeQuery(id+"F4.imprint","IMPRINT",EDGE,{"derivedFrom":sQuery(id+"F4.wireOp",EDGE,"E8.0.11.7")}),1.0]])]});
            var Q50;
            Q50=makeQuery(id+"F4.imprint","IMPRINT",FACE,{"disambiguationData":[TD([[makeQuery(id+"F4.imprint","IMPRINT",EDGE,{"derivedFrom":sQuery(id+"F4.wireOp",EDGE,"E8.0.12.9")}),1.0]])]});
            var Q51;
            Q51=makeQuery(id+"F4.imprint","IMPRINT",FACE,{"disambiguationData":[TD([[makeQuery(id+"F4.imprint","IMPRINT",EDGE,{"derivedFrom":sQuery(id+"F4.wireOp",EDGE,"E8.0.10.5")}),1.0]])]});
            var Q52;
            Q52=makeQuery(id+"F4.imprint","IMPRINT",FACE,{"disambiguationData":[TD([[makeQuery(id+"F4.imprint","IMPRINT",EDGE,{"derivedFrom":sQuery(id+"F4.wireOp",EDGE,"E8.0.8.15")}),1.0]])]});
            var Q53;
            Q53=makeQuery(id+"F4.imprint","IMPRINT",FACE,{"disambiguationData":[TD([[makeQuery(id+"F4.imprint","IMPRINT",EDGE,{"derivedFrom":sQuery(id+"F4.wireOp",EDGE,"E8.0.3.10")}),1.0]])]});
            var Q54;
            Q54=makeQuery(id+"F4.imprint","IMPRINT",FACE,{"disambiguationData":[TD([[makeQuery(id+"F4.imprint","IMPRINT",EDGE,{"derivedFrom":sQuery(id+"F4.wireOp",EDGE,"E8.0.4.12")}),1.0]])]});
            var Q55;
            Q55=makeQuery(id+"F4.imprint","IMPRINT",FACE,{"disambiguationData":[TD([[makeQuery(id+"F4.imprint","IMPRINT",EDGE,{"derivedFrom":sQuery(id+"F4.wireOp",EDGE,"E8.0.5.14")}),1.0]])]});
            var Q56;
            Q56=makeQuery(id+"F4.imprint","IMPRINT",FACE,{"disambiguationData":[TD([[makeQuery(id+"F4.imprint","IMPRINT",EDGE,{"derivedFrom":sQuery(id+"F4.wireOp",EDGE,"E8.0.7.4")}),1.0]])]});
            var Q57;
            Q57=makeQuery(id+"F4.imprint","IMPRINT",FACE,{"disambiguationData":[TD([[makeQuery(id+"F4.imprint","IMPRINT",EDGE,{"derivedFrom":sQuery(id+"F4.wireOp",EDGE,"E7.9.0.0")}),1.0]])]});
            var Q58;
            Q58=makeQuery(id+"F4.imprint","IMPRINT",FACE,{"disambiguationData":[TD([[makeQuery(id+"F4.imprint","IMPRINT",EDGE,{"derivedFrom":sQuery(id+"F4.wireOp",EDGE,"E8.0.0.4")}),1.0]])]});
            var Q59;
            Q59=makeQuery(id+"F4.imprint","IMPRINT",FACE,{"disambiguationData":[TD([[makeQuery(id+"F4.imprint","IMPRINT",EDGE,{"derivedFrom":sQuery(id+"F4.wireOp",EDGE,"E8.0.1.6")}),1.0]])]});
            var Q60;
            Q60=makeQuery(id+"F4.imprint","IMPRINT",FACE,{"disambiguationData":[TD([[makeQuery(id+"F4.imprint","IMPRINT",EDGE,{"derivedFrom":sQuery(id+"F4.wireOp",EDGE,"E8.0.2.8")}),1.0]])]});
            var Q61;
            Q61=makeQuery(id+"F4.imprint","IMPRINT",FACE,{"disambiguationData":[TD([[makeQuery(id+"F4.imprint","IMPRINT",EDGE,{"derivedFrom":sQuery(id+"F4.wireOp",EDGE,"E8.0.13.9")}),1.0]])]});
            var Q62;
            Q62=makeQuery(id+"F4.imprint","IMPRINT",FACE,{"disambiguationData":[TD([[makeQuery(id+"F4.imprint","IMPRINT",EDGE,{"derivedFrom":sQuery(id+"F4.wireOp",EDGE,"E8.0.14.11")}),1.0]])]});
            var Q63;
            Q63=makeQuery(id+"F4.imprint","IMPRINT",FACE,{"disambiguationData":[TD([[makeQuery(id+"F4.imprint","IMPRINT",EDGE,{"derivedFrom":sQuery(id+"F4.wireOp",EDGE,"E8.0.15.13")}),1.0]])]});
            var Q64;
            {var subQ1=sQuery(id+"F4.wireOp",EDGE,"E8.0.6.8");Q64=makeQuery(id+"F4.imprint","IMPRINT",FACE,{"disambiguationData":[TD([[makeQuery(id+"F4.imprint","IMPRINT",EDGE,{"derivedFrom":subQ1}),1.0]])]});}
            var Q65;
            Q65=makeQuery(id+"F4.imprint","IMPRINT",FACE,{"disambiguationData":[TD([[makeQuery(id+"F4.imprint","IMPRINT",EDGE,{"derivedFrom":sQuery(id+"F4.wireOp",EDGE,"E8.0.8.13")}),1.0]])]});
            var Q66;
            Q66=makeQuery(id+"F4.imprint","IMPRINT",FACE,{"disambiguationData":[TD([[makeQuery(id+"F4.imprint","IMPRINT",EDGE,{"derivedFrom":sQuery(id+"F4.wireOp",EDGE,"E8.0.10.3")}),1.0]])]});
            var Q67;
            Q67=makeQuery(id+"F4.imprint","IMPRINT",FACE,{"disambiguationData":[TD([[makeQuery(id+"F4.imprint","IMPRINT",EDGE,{"derivedFrom":sQuery(id+"F4.wireOp",EDGE,"E8.0.11.5")}),1.0]])]});
            var Q68;
            Q68=makeQuery(id+"F4.imprint","IMPRINT",FACE,{"disambiguationData":[TD([[makeQuery(id+"F4.imprint","IMPRINT",EDGE,{"derivedFrom":sQuery(id+"F4.wireOp",EDGE,"E8.0.12.7")}),1.0]])]});
            var Q69;
            Q69=makeQuery(id+"F4.imprint","IMPRINT",FACE,{"disambiguationData":[TD([[makeQuery(id+"F4.imprint","IMPRINT",EDGE,{"derivedFrom":sQuery(id+"F4.wireOp",EDGE,"E8.0.3.9")}),1.0]])]});
            var Q70;
            Q70=makeQuery(id+"F4.imprint","IMPRINT",FACE,{"disambiguationData":[TD([[makeQuery(id+"F4.imprint","IMPRINT",EDGE,{"derivedFrom":sQuery(id+"F4.wireOp",EDGE,"E8.0.4.11")}),1.0]])]});
            var Q71;
            Q71=makeQuery(id+"F4.imprint","IMPRINT",FACE,{"disambiguationData":[TD([[makeQuery(id+"F4.imprint","IMPRINT",EDGE,{"derivedFrom":sQuery(id+"F4.wireOp",EDGE,"E8.0.5.13")}),1.0]])]});
            var Q72;
            Q72=makeQuery(id+"F4.imprint","IMPRINT",FACE,{"disambiguationData":[TD([[makeQuery(id+"F4.imprint","IMPRINT",EDGE,{"derivedFrom":sQuery(id+"F4.wireOp",EDGE,"E8.0.7.3")}),1.0]])]});
            var Q73;
            Q73=makeQuery(id+"F4.imprint","IMPRINT",FACE,{"disambiguationData":[TD([[makeQuery(id+"F4.imprint","IMPRINT",EDGE,{"derivedFrom":sQuery(id+"F4.wireOp",EDGE,"E7.8.1.0")}),1.0]])]});
            var Q74;
            Q74=makeQuery(id+"F4.imprint","IMPRINT",FACE,{"disambiguationData":[TD([[makeQuery(id+"F4.imprint","IMPRINT",EDGE,{"derivedFrom":sQuery(id+"F4.wireOp",EDGE,"E8.0.1.5")}),1.0]])]});
            var Q75;
            Q75=makeQuery(id+"F4.imprint","IMPRINT",FACE,{"disambiguationData":[TD([[makeQuery(id+"F4.imprint","IMPRINT",EDGE,{"derivedFrom":sQuery(id+"F4.wireOp",EDGE,"E8.0.0.3")}),1.0]])]});
            var Q76;
            Q76=makeQuery(id+"F4.imprint","IMPRINT",FACE,{"disambiguationData":[TD([[makeQuery(id+"F4.imprint","IMPRINT",EDGE,{"derivedFrom":sQuery(id+"F4.wireOp",EDGE,"E8.0.2.7")}),1.0]])]});
            var Q77;
            Q77=makeQuery(id+"F4.imprint","IMPRINT",FACE,{"disambiguationData":[TD([[makeQuery(id+"F4.imprint","IMPRINT",EDGE,{"derivedFrom":sQuery(id+"F4.wireOp",EDGE,"E8.0.13.8")}),1.0]])]});
            var Q78;
            Q78=makeQuery(id+"F4.imprint","IMPRINT",FACE,{"disambiguationData":[TD([[makeQuery(id+"F4.imprint","IMPRINT",EDGE,{"derivedFrom":sQuery(id+"F4.wireOp",EDGE,"E8.0.14.10")}),1.0]])]});
            var Q79;
            Q79=makeQuery(id+"F4.imprint","IMPRINT",FACE,{"disambiguationData":[TD([[makeQuery(id+"F4.imprint","IMPRINT",EDGE,{"derivedFrom":sQuery(id+"F4.wireOp",EDGE,"E8.0.15.12")}),1.0]])]});
            var Q80;
            {var subQ6=sQuery(id+"F4.wireOp",EDGE,"E8.3.6.7");Q80=makeQuery(id+"F4.imprint","IMPRINT",FACE,{"disambiguationData":[TD([[makeQuery(id+"F4.imprint","IMPRINT",EDGE,{"derivedFrom":subQ6}),1.0]])]});}
            var Q81;
            Q81=makeQuery(id+"F4.imprint","IMPRINT",FACE,{"disambiguationData":[TD([[makeQuery(id+"F4.imprint","IMPRINT",EDGE,{"derivedFrom":sQuery(id+"F4.wireOp",EDGE,"E8.0.8.12")}),1.0]])]});
            var Q82;
            Q82=makeQuery(id+"F4.imprint","IMPRINT",FACE,{"disambiguationData":[TD([[makeQuery(id+"F4.imprint","IMPRINT",EDGE,{"derivedFrom":sQuery(id+"F4.wireOp",EDGE,"E8.0.10.2")}),1.0]])]});
            var Q83;
            Q83=makeQuery(id+"F4.imprint","IMPRINT",FACE,{"disambiguationData":[TD([[makeQuery(id+"F4.imprint","IMPRINT",EDGE,{"derivedFrom":sQuery(id+"F4.wireOp",EDGE,"E8.0.11.4")}),1.0]])]});
            var Q84;
            Q84=makeQuery(id+"F4.imprint","IMPRINT",FACE,{"disambiguationData":[TD([[makeQuery(id+"F4.imprint","IMPRINT",EDGE,{"derivedFrom":sQuery(id+"F4.wireOp",EDGE,"E8.0.12.6")}),1.0]])]});
            var Q85;
            Q85=makeQuery(id+"F4.imprint","IMPRINT",FACE,{"disambiguationData":[TD([[makeQuery(id+"F4.imprint","IMPRINT",EDGE,{"derivedFrom":sQuery(id+"F4.wireOp",EDGE,"E8.0.3.8")}),1.0]])]});
            var Q86;
            Q86=makeQuery(id+"F4.imprint","IMPRINT",FACE,{"disambiguationData":[TD([[makeQuery(id+"F4.imprint","IMPRINT",EDGE,{"derivedFrom":sQuery(id+"F4.wireOp",EDGE,"E8.0.4.10")}),1.0]])]});
            var Q87;
            Q87=makeQuery(id+"F4.imprint","IMPRINT",FACE,{"disambiguationData":[TD([[makeQuery(id+"F4.imprint","IMPRINT",EDGE,{"derivedFrom":sQuery(id+"F4.wireOp",EDGE,"E8.0.5.12")}),1.0]])]});
            var Q88;
            Q88=makeQuery(id+"F4.imprint","IMPRINT",FACE,{"disambiguationData":[TD([[makeQuery(id+"F4.imprint","IMPRINT",EDGE,{"derivedFrom":sQuery(id+"F4.wireOp",EDGE,"E8.0.7.2")}),1.0]])]});
            var Q89;
            Q89=makeQuery(id+"F4.imprint","IMPRINT",FACE,{"disambiguationData":[TD([[makeQuery(id+"F4.imprint","IMPRINT",EDGE,{"derivedFrom":sQuery(id+"F4.wireOp",EDGE,"E7.8.0.0")}),1.0]])]});
            var Q90;
            Q90=makeQuery(id+"F4.imprint","IMPRINT",FACE,{"disambiguationData":[TD([[makeQuery(id+"F4.imprint","IMPRINT",EDGE,{"derivedFrom":sQuery(id+"F4.wireOp",EDGE,"E8.0.0.2")}),1.0]])]});
            var Q91;
            Q91=makeQuery(id+"F4.imprint","IMPRINT",FACE,{"disambiguationData":[TD([[makeQuery(id+"F4.imprint","IMPRINT",EDGE,{"derivedFrom":sQuery(id+"F4.wireOp",EDGE,"E8.0.1.4")}),1.0]])]});
            var Q92;
            Q92=makeQuery(id+"F4.imprint","IMPRINT",FACE,{"disambiguationData":[TD([[makeQuery(id+"F4.imprint","IMPRINT",EDGE,{"derivedFrom":sQuery(id+"F4.wireOp",EDGE,"E8.0.2.6")}),1.0]])]});
            var Q93;
            Q93=makeQuery(id+"F4.imprint","IMPRINT",FACE,{"disambiguationData":[TD([[makeQuery(id+"F4.imprint","IMPRINT",EDGE,{"derivedFrom":sQuery(id+"F4.wireOp",EDGE,"E8.0.13.6")}),1.0]])]});
            var Q94;
            Q94=makeQuery(id+"F4.imprint","IMPRINT",FACE,{"disambiguationData":[TD([[makeQuery(id+"F4.imprint","IMPRINT",EDGE,{"derivedFrom":sQuery(id+"F4.wireOp",EDGE,"E8.0.14.8")}),1.0]])]});
            var Q95;
            Q95=makeQuery(id+"F4.imprint","IMPRINT",FACE,{"disambiguationData":[TD([[makeQuery(id+"F4.imprint","IMPRINT",EDGE,{"derivedFrom":sQuery(id+"F4.wireOp",EDGE,"E8.0.15.10")}),1.0]])]});
            var Q96;
            {var subQ1=sQuery(id+"F4.wireOp",EDGE,"E8.3.8.8");Q96=makeQuery(id+"F4.imprint","IMPRINT",FACE,{"disambiguationData":[TD([[makeQuery(id+"F4.imprint","IMPRINT",EDGE,{"derivedFrom":subQ1}),1.0]])]});}
            var Q97;
            Q97=makeQuery(id+"F4.imprint","IMPRINT",FACE,{"disambiguationData":[TD([[makeQuery(id+"F4.imprint","IMPRINT",EDGE,{"derivedFrom":sQuery(id+"F4.wireOp",EDGE,"E8.0.8.10")}),1.0]])]});
            var Q98;
            Q98=makeQuery(id+"F4.imprint","IMPRINT",FACE,{"disambiguationData":[TD([[makeQuery(id+"F4.imprint","IMPRINT",EDGE,{"derivedFrom":sQuery(id+"F4.wireOp",EDGE,"E8.0.9.14")}),1.0]])]});
            var Q99;
            Q99=makeQuery(id+"F4.imprint","IMPRINT",FACE,{"disambiguationData":[TD([[makeQuery(id+"F4.imprint","IMPRINT",EDGE,{"derivedFrom":sQuery(id+"F4.wireOp",EDGE,"E8.0.11.2")}),1.0]])]});
            var Q100;
            Q100=makeQuery(id+"F4.imprint","IMPRINT",FACE,{"disambiguationData":[TD([[makeQuery(id+"F4.imprint","IMPRINT",EDGE,{"derivedFrom":sQuery(id+"F4.wireOp",EDGE,"E8.0.12.4")}),1.0]])]});
            var Q101;
            Q101=makeQuery(id+"F4.imprint","IMPRINT",FACE,{"disambiguationData":[TD([[makeQuery(id+"F4.imprint","IMPRINT",EDGE,{"derivedFrom":sQuery(id+"F4.wireOp",EDGE,"E8.0.3.6")}),1.0]])]});
            var Q102;
            Q102=makeQuery(id+"F4.imprint","IMPRINT",FACE,{"disambiguationData":[TD([[makeQuery(id+"F4.imprint","IMPRINT",EDGE,{"derivedFrom":sQuery(id+"F4.wireOp",EDGE,"E8.0.4.8")}),1.0]])]});
            var Q103;
            Q103=makeQuery(id+"F4.imprint","IMPRINT",FACE,{"disambiguationData":[TD([[makeQuery(id+"F4.imprint","IMPRINT",EDGE,{"derivedFrom":sQuery(id+"F4.wireOp",EDGE,"E8.0.5.10")}),1.0]])]});
            var Q104;
            Q104=makeQuery(id+"F4.imprint","IMPRINT",FACE,{"disambiguationData":[TD([[makeQuery(id+"F4.imprint","IMPRINT",EDGE,{"derivedFrom":sQuery(id+"F4.wireOp",EDGE,"E8.0.6.14")}),1.0]])]});
            var Q105;
            Q105=makeQuery(id+"F4.imprint","IMPRINT",FACE,{"disambiguationData":[TD([[makeQuery(id+"F4.imprint","IMPRINT",EDGE,{"derivedFrom":sQuery(id+"F4.wireOp",EDGE,"E7.15.0.0")}),1.0]])]});
            var Q106;
            Q106=makeQuery(id+"F4.imprint","IMPRINT",FACE,{"disambiguationData":[TD([[makeQuery(id+"F4.imprint","IMPRINT",EDGE,{"derivedFrom":sQuery(id+"F4.wireOp",EDGE,"E8.0.1.2")}),1.0]])]});
            var Q107;
            Q107=makeQuery(id+"F4.imprint","IMPRINT",FACE,{"disambiguationData":[TD([[makeQuery(id+"F4.imprint","IMPRINT",EDGE,{"derivedFrom":sQuery(id+"F4.wireOp",EDGE,"E8.0.2.4")}),1.0]])]});
            var Q108;
            Q108=makeQuery(id+"F4.imprint","IMPRINT",FACE,{"disambiguationData":[TD([[makeQuery(id+"F4.imprint","IMPRINT",EDGE,{"derivedFrom":sQuery(id+"F4.wireOp",EDGE,"E8.0.13.5")}),1.0]])]});
            var Q109;
            Q109=makeQuery(id+"F4.imprint","IMPRINT",FACE,{"disambiguationData":[TD([[makeQuery(id+"F4.imprint","IMPRINT",EDGE,{"derivedFrom":sQuery(id+"F4.wireOp",EDGE,"E8.0.14.7")}),1.0]])]});
            var Q110;
            Q110=makeQuery(id+"F4.imprint","IMPRINT",FACE,{"disambiguationData":[TD([[makeQuery(id+"F4.imprint","IMPRINT",EDGE,{"derivedFrom":sQuery(id+"F4.wireOp",EDGE,"E8.0.15.9")}),1.0]])]});
            var Q111;
            Q111=makeQuery(id+"F4.imprint","IMPRINT",FACE,{"disambiguationData":[TD([[makeQuery(id+"F4.imprint","IMPRINT",EDGE,{"derivedFrom":sQuery(id+"F4.wireOp",EDGE,"E8.0.8.5")}),1.0]])]});
            var Q112;
            Q112=makeQuery(id+"F4.imprint","IMPRINT",FACE,{"disambiguationData":[TD([[makeQuery(id+"F4.imprint","IMPRINT",EDGE,{"derivedFrom":sQuery(id+"F4.wireOp",EDGE,"E8.0.9.13")}),1.0]])]});
            var Q113;
            Q113=makeQuery(id+"F4.imprint","IMPRINT",FACE,{"disambiguationData":[TD([[makeQuery(id+"F4.imprint","IMPRINT",EDGE,{"derivedFrom":sQuery(id+"F4.wireOp",EDGE,"E8.0.10.15")}),1.0]])]});
            var Q114;
            Q114=makeQuery(id+"F4.imprint","IMPRINT",FACE,{"disambiguationData":[TD([[makeQuery(id+"F4.imprint","IMPRINT",EDGE,{"derivedFrom":sQuery(id+"F4.wireOp",EDGE,"E8.0.12.3")}),1.0]])]});
            var Q115;
            Q115=makeQuery(id+"F4.imprint","IMPRINT",FACE,{"disambiguationData":[TD([[makeQuery(id+"F4.imprint","IMPRINT",EDGE,{"derivedFrom":sQuery(id+"F4.wireOp",EDGE,"E8.0.3.5")}),1.0]])]});
            var Q116;
            Q116=makeQuery(id+"F4.imprint","IMPRINT",FACE,{"disambiguationData":[TD([[makeQuery(id+"F4.imprint","IMPRINT",EDGE,{"derivedFrom":sQuery(id+"F4.wireOp",EDGE,"E8.0.4.7")}),1.0]])]});
            var Q117;
            Q117=makeQuery(id+"F4.imprint","IMPRINT",FACE,{"disambiguationData":[TD([[makeQuery(id+"F4.imprint","IMPRINT",EDGE,{"derivedFrom":sQuery(id+"F4.wireOp",EDGE,"E8.0.5.9")}),1.0]])]});
            var Q118;
            Q118=makeQuery(id+"F4.imprint","IMPRINT",FACE,{"disambiguationData":[TD([[makeQuery(id+"F4.imprint","IMPRINT",EDGE,{"derivedFrom":sQuery(id+"F4.wireOp",EDGE,"E8.0.6.13")}),1.0]])]});
            var Q119;
            Q119=makeQuery(id+"F4.imprint","IMPRINT",FACE,{"disambiguationData":[TD([[makeQuery(id+"F4.imprint","IMPRINT",EDGE,{"derivedFrom":sQuery(id+"F4.wireOp",EDGE,"E7.14.1.0")}),1.0]])]});
            var Q120;
            Q120=makeQuery(id+"F4.imprint","IMPRINT",FACE,{"disambiguationData":[TD([[makeQuery(id+"F4.imprint","IMPRINT",EDGE,{"derivedFrom":sQuery(id+"F4.wireOp",EDGE,"E8.0.0.15")}),1.0]])]});
            var Q121;
            Q121=makeQuery(id+"F4.imprint","IMPRINT",FACE,{"disambiguationData":[TD([[makeQuery(id+"F4.imprint","IMPRINT",EDGE,{"derivedFrom":sQuery(id+"F4.wireOp",EDGE,"E8.0.2.3")}),1.0]])]});
            var Q122;
            Q122=makeQuery(id+"F4.imprint","IMPRINT",FACE,{"disambiguationData":[TD([[makeQuery(id+"F4.imprint","IMPRINT",EDGE,{"derivedFrom":sQuery(id+"F4.wireOp",EDGE,"E8.0.4.9")}),1.0]])]});
            var Q123;
            Q123=makeQuery(id+"F4.imprint","IMPRINT",FACE,{"disambiguationData":[TD([[makeQuery(id+"F4.imprint","IMPRINT",EDGE,{"derivedFrom":sQuery(id+"F4.wireOp",EDGE,"E8.0.5.11")}),1.0]])]});
            var Q124;
            Q124=makeQuery(id+"F4.imprint","IMPRINT",FACE,{"disambiguationData":[TD([[makeQuery(id+"F4.imprint","IMPRINT",EDGE,{"derivedFrom":sQuery(id+"F4.wireOp",EDGE,"E8.0.6.15")}),1.0]])]});
            var Q125;
            Q125=makeQuery(id+"F4.imprint","IMPRINT",FACE,{"disambiguationData":[TD([[makeQuery(id+"F4.imprint","IMPRINT",EDGE,{"derivedFrom":sQuery(id+"F4.wireOp",EDGE,"E8.0.8.11")}),1.0]])]});
            var Q126;
            Q126=makeQuery(id+"F4.imprint","IMPRINT",FACE,{"disambiguationData":[TD([[makeQuery(id+"F4.imprint","IMPRINT",EDGE,{"derivedFrom":sQuery(id+"F4.wireOp",EDGE,"E7.15.1.0")}),1.0]])]});
            var Q127;
            Q127=makeQuery(id+"F4.imprint","IMPRINT",FACE,{"disambiguationData":[TD([[makeQuery(id+"F4.imprint","IMPRINT",EDGE,{"derivedFrom":sQuery(id+"F4.wireOp",EDGE,"E8.0.1.3")}),1.0]])]});
            var Q128;
            Q128=makeQuery(id+"F4.imprint","IMPRINT",FACE,{"disambiguationData":[TD([[makeQuery(id+"F4.imprint","IMPRINT",EDGE,{"derivedFrom":sQuery(id+"F4.wireOp",EDGE,"E8.0.2.5")}),1.0]])]});
            var Q129;
            Q129=makeQuery(id+"F4.imprint","IMPRINT",FACE,{"disambiguationData":[TD([[makeQuery(id+"F4.imprint","IMPRINT",EDGE,{"derivedFrom":sQuery(id+"F4.wireOp",EDGE,"E8.0.3.7")}),1.0]])]});
            var Q130;
            Q130=makeQuery(id+"F4.imprint","IMPRINT",FACE,{"disambiguationData":[TD([[makeQuery(id+"F4.imprint","IMPRINT",EDGE,{"derivedFrom":sQuery(id+"F4.wireOp",EDGE,"E8.0.14.9")}),1.0]])]});
            var Q131;
            Q131=makeQuery(id+"F4.imprint","IMPRINT",FACE,{"disambiguationData":[TD([[makeQuery(id+"F4.imprint","IMPRINT",EDGE,{"derivedFrom":sQuery(id+"F4.wireOp",EDGE,"E8.0.15.11")}),1.0]])]});
            var Q132;
            Q132=makeQuery(id+"F4.imprint","IMPRINT",FACE,{"disambiguationData":[TD([[makeQuery(id+"F4.imprint","IMPRINT",EDGE,{"derivedFrom":sQuery(id+"F4.wireOp",EDGE,"E8.0.9.15")}),1.0]])]});
            var Q133;
            Q133=makeQuery(id+"F4.imprint","IMPRINT",FACE,{"disambiguationData":[TD([[makeQuery(id+"F4.imprint","IMPRINT",EDGE,{"derivedFrom":sQuery(id+"F4.wireOp",EDGE,"E8.0.11.3")}),1.0]])]});
            var Q134;
            Q134=makeQuery(id+"F4.imprint","IMPRINT",FACE,{"disambiguationData":[TD([[makeQuery(id+"F4.imprint","IMPRINT",EDGE,{"derivedFrom":sQuery(id+"F4.wireOp",EDGE,"E8.0.12.5")}),1.0]])]});
            var Q135;
            Q135=makeQuery(id+"F4.imprint","IMPRINT",FACE,{"disambiguationData":[TD([[makeQuery(id+"F4.imprint","IMPRINT",EDGE,{"derivedFrom":sQuery(id+"F4.wireOp",EDGE,"E8.0.13.7")}),1.0]])]});
            var Q136;
            Q136=makeQuery(id+"F4.imprint","IMPRINT",FACE,{"disambiguationData":[TD([[makeQuery(id+"F4.imprint","IMPRINT",EDGE,{"derivedFrom":sQuery(id+"F4.wireOp",EDGE,"E7.6.0.0")}),1.0]])]});
            var Q137;
            Q137=makeQuery(id+"F4.imprint","IMPRINT",FACE,{"disambiguationData":[TD([[makeQuery(id+"F4.imprint","IMPRINT",EDGE,{"derivedFrom":sQuery(id+"F4.wireOp",EDGE,"E7.5.1.0")}),1.0]])]});
            var Q138;
            Q138=makeQuery(id+"F4.imprint","IMPRINT",FACE,{"disambiguationData":[TD([[makeQuery(id+"F4.imprint","IMPRINT",EDGE,{"derivedFrom":sQuery(id+"F4.wireOp",EDGE,"E7.5.0.0")}),1.0]])]});
            var Q139;
            Q139=makeQuery(id+"F4.imprint","IMPRINT",FACE,{"disambiguationData":[TD([[makeQuery(id+"F4.imprint","IMPRINT",EDGE,{"derivedFrom":sQuery(id+"F4.wireOp",EDGE,"E7.4.1.0")}),1.0]])]});
            var Q140;
            Q140=makeQuery(id+"F4.imprint","IMPRINT",FACE,{"disambiguationData":[TD([[makeQuery(id+"F4.imprint","IMPRINT",EDGE,{"derivedFrom":sQuery(id+"F4.wireOp",EDGE,"E7.4.0.0")}),1.0]])]});
            var Q141;
            Q141=makeQuery(id+"F4.imprint","IMPRINT",FACE,{"disambiguationData":[TD([[makeQuery(id+"F4.imprint","IMPRINT",EDGE,{"derivedFrom":sQuery(id+"F4.wireOp",EDGE,"E7.3.1.0")}),1.0]])]});
            var Q142;
            Q142=makeQuery(id+"F4.imprint","IMPRINT",FACE,{"disambiguationData":[TD([[makeQuery(id+"F4.imprint","IMPRINT",EDGE,{"derivedFrom":sQuery(id+"F4.wireOp",EDGE,"E7.3.0.0")}),1.0]])]});
            var Q143;
            Q143=makeQuery(id+"F4.imprint","IMPRINT",FACE,{"disambiguationData":[TD([[makeQuery(id+"F4.imprint","IMPRINT",EDGE,{"derivedFrom":sQuery(id+"F4.wireOp",EDGE,"E7.2.1.0")}),1.0]])]});
            var Q144;
            Q144=makeQuery(id+"F4.imprint","IMPRINT",FACE,{"disambiguationData":[TD([[makeQuery(id+"F4.imprint","IMPRINT",EDGE,{"derivedFrom":sQuery(id+"F4.wireOp",EDGE,"E7.2.0.0")}),1.0]])]});
            var Q145;
            Q145=makeQuery(id+"F4.imprint","IMPRINT",FACE,{"disambiguationData":[TD([[makeQuery(id+"F4.imprint","IMPRINT",EDGE,{"derivedFrom":sQuery(id+"F4.wireOp",EDGE,"E7.1.1.0")}),1.0]])]});
            var Q146;
            Q146=makeQuery(id+"F4.imprint","IMPRINT",FACE,{"disambiguationData":[TD([[makeQuery(id+"F4.imprint","IMPRINT",EDGE,{"derivedFrom":sQuery(id+"F4.wireOp",EDGE,"E7.1.0.0")}),1.0]])]});
            var Q147;
            Q147=makeQuery(id+"F4.imprint","IMPRINT",FACE,{"disambiguationData":[TD([[makeQuery(id+"F4.imprint","IMPRINT",EDGE,{"derivedFrom":sQuery(id+"F4.wireOp",EDGE,"E7.0.1.0")}),1.0]])]});
            var Q148;
            Q148=makeQuery(id+"F4.imprint","IMPRINT",FACE,{"disambiguationData":[TD([[makeQuery(id+"F4.imprint","IMPRINT",EDGE,{"derivedFrom":sQuery(id+"F4.wireOp",EDGE,"E5.bottom")}),-1.0]])]});
            var Q149;
            Q149=makeQuery(id+"F4.imprint","IMPRINT",FACE,{"disambiguationData":[TD([[makeQuery(id+"F4.imprint","IMPRINT",EDGE,{"derivedFrom":sQuery(id+"F4.wireOp",EDGE,"E7.7.0.0")}),1.0]])]});
            var Q150;
            Q150=makeQuery(id+"F4.imprint","IMPRINT",FACE,{"disambiguationData":[TD([[makeQuery(id+"F4.imprint","IMPRINT",EDGE,{"derivedFrom":sQuery(id+"F4.wireOp",EDGE,"E7.6.1.0")}),1.0]])]});
            var Q151;
            Q151=makeQuery(id+"F4.imprint","IMPRINT",FACE,{"disambiguationData":[TD([[makeQuery(id+"F4.imprint","IMPRINT",EDGE,{"derivedFrom":sQuery(id+"F4.wireOp",EDGE,"E7.7.1.0")}),1.0]])]});
            var Q152;
            Q152=makeQuery(id+"F4.imprint","IMPRINT",FACE,{"disambiguationData":[TD([[makeQuery(id+"F4.imprint","IMPRINT",EDGE,{"derivedFrom":sQuery(id+"F4.wireOp",EDGE,"E8.0.12.2")}),1.0]])]});
            var Q153;
            Q153=makeQuery(id+"F4.imprint","IMPRINT",FACE,{"disambiguationData":[TD([[makeQuery(id+"F4.imprint","IMPRINT",EDGE,{"derivedFrom":sQuery(id+"F4.wireOp",EDGE,"E8.0.13.4")}),1.0]])]});
            var Q154;
            Q154=makeQuery(id+"F4.imprint","IMPRINT",FACE,{"disambiguationData":[TD([[makeQuery(id+"F4.imprint","IMPRINT",EDGE,{"derivedFrom":sQuery(id+"F4.wireOp",EDGE,"E8.0.14.6")}),1.0]])]});
            var Q155;
            Q155=makeQuery(id+"F4.imprint","IMPRINT",FACE,{"disambiguationData":[TD([[makeQuery(id+"F4.imprint","IMPRINT",EDGE,{"derivedFrom":sQuery(id+"F4.wireOp",EDGE,"E8.0.15.8")}),1.0]])]});
            var Q156;
            Q156=makeQuery(id+"F4.imprint","IMPRINT",FACE,{"disambiguationData":[TD([[makeQuery(id+"F4.imprint","IMPRINT",EDGE,{"derivedFrom":sQuery(id+"F4.wireOp",EDGE,"E8.0.6.12")}),1.0]])]});
            var Q157;
            Q157=makeQuery(id+"F4.imprint","IMPRINT",FACE,{"disambiguationData":[TD([[makeQuery(id+"F4.imprint","IMPRINT",EDGE,{"derivedFrom":sQuery(id+"F4.wireOp",EDGE,"E8.0.9.12")}),1.0]])]});
            var Q158;
            Q158=makeQuery(id+"F4.imprint","IMPRINT",FACE,{"disambiguationData":[TD([[makeQuery(id+"F4.imprint","IMPRINT",EDGE,{"derivedFrom":sQuery(id+"F4.wireOp",EDGE,"E8.0.8.4")}),1.0]])]});
            var Q159;
            Q159=makeQuery(id+"F4.imprint","IMPRINT",FACE,{"disambiguationData":[TD([[makeQuery(id+"F4.imprint","IMPRINT",EDGE,{"derivedFrom":sQuery(id+"F4.wireOp",EDGE,"E8.0.10.14")}),1.0]])]});
            var Q160;
            Q160=makeQuery(id+"F4.imprint","IMPRINT",FACE,{"disambiguationData":[TD([[makeQuery(id+"F4.imprint","IMPRINT",EDGE,{"derivedFrom":sQuery(id+"F4.wireOp",EDGE,"E8.0.2.2")}),1.0]])]});
            var Q161;
            Q161=makeQuery(id+"F4.imprint","IMPRINT",FACE,{"disambiguationData":[TD([[makeQuery(id+"F4.imprint","IMPRINT",EDGE,{"derivedFrom":sQuery(id+"F4.wireOp",EDGE,"E8.0.3.4")}),1.0]])]});
            var Q162;
            Q162=makeQuery(id+"F4.imprint","IMPRINT",FACE,{"disambiguationData":[TD([[makeQuery(id+"F4.imprint","IMPRINT",EDGE,{"derivedFrom":sQuery(id+"F4.wireOp",EDGE,"E8.0.4.6")}),1.0]])]});
            var Q163;
            Q163=makeQuery(id+"F4.imprint","IMPRINT",FACE,{"disambiguationData":[TD([[makeQuery(id+"F4.imprint","IMPRINT",EDGE,{"derivedFrom":sQuery(id+"F4.wireOp",EDGE,"E8.0.5.8")}),1.0]])]});
            var Q164;
            Q164=makeQuery(id+"F4.imprint","IMPRINT",FACE,{"disambiguationData":[TD([[makeQuery(id+"F4.imprint","IMPRINT",EDGE,{"derivedFrom":sQuery(id+"F4.wireOp",EDGE,"E7.14.0.0")}),1.0]])]});
            var Q165;
            Q165=makeQuery(id+"F4.imprint","IMPRINT",FACE,{"disambiguationData":[TD([[makeQuery(id+"F4.imprint","IMPRINT",EDGE,{"derivedFrom":sQuery(id+"F4.wireOp",EDGE,"E8.0.0.14")}),1.0]])]});
            var Q166;
            {var subQ0=sQuery(id+"F4.wireOp",EDGE,"E8.6.7.8");Q166=makeQuery(id+"F4.imprint","IMPRINT",FACE,{"disambiguationData":[TD([[makeQuery(id+"F4.imprint","IMPRINT",EDGE,{"derivedFrom":subQ0}),-1.0]])]});}
            var Q167;
            {var subQ5=sQuery(id+"F4.wireOp",EDGE,"E8.0.9.8");Q167=makeQuery(id+"F4.imprint","IMPRINT",FACE,{"disambiguationData":[TD([[makeQuery(id+"F4.imprint","IMPRINT",EDGE,{"derivedFrom":subQ5}),1.0]])]});}
            var Q168;
            Q168=makeQuery(id+"F4.imprint","IMPRINT",FACE,{"disambiguationData":[TD([[makeQuery(id+"F4.imprint","IMPRINT",EDGE,{"derivedFrom":sQuery(id+"F4.wireOp",EDGE,"E8.0.11.15")}),1.0]])]});
            var Q169;
            Q169=makeQuery(id+"F4.imprint","IMPRINT",FACE,{"disambiguationData":[TD([[makeQuery(id+"F4.imprint","IMPRINT",EDGE,{"derivedFrom":sQuery(id+"F4.wireOp",EDGE,"E8.0.13.3")}),1.0]])]});
            var Q170;
            Q170=makeQuery(id+"F4.imprint","IMPRINT",FACE,{"disambiguationData":[TD([[makeQuery(id+"F4.imprint","IMPRINT",EDGE,{"derivedFrom":sQuery(id+"F4.wireOp",EDGE,"E8.0.14.5")}),1.0]])]});
            var Q171;
            Q171=makeQuery(id+"F4.imprint","IMPRINT",FACE,{"disambiguationData":[TD([[makeQuery(id+"F4.imprint","IMPRINT",EDGE,{"derivedFrom":sQuery(id+"F4.wireOp",EDGE,"E8.0.15.7")}),1.0]])]});
            var Q172;
            Q172=makeQuery(id+"F4.imprint","IMPRINT",FACE,{"disambiguationData":[TD([[makeQuery(id+"F4.imprint","IMPRINT",EDGE,{"derivedFrom":sQuery(id+"F4.wireOp",EDGE,"E8.0.6.11")}),1.0]])]});
            var Q173;
            Q173=makeQuery(id+"F4.imprint","IMPRINT",FACE,{"disambiguationData":[TD([[makeQuery(id+"F4.imprint","IMPRINT",EDGE,{"derivedFrom":sQuery(id+"F4.wireOp",EDGE,"E8.0.8.3")}),1.0]])]});
            var Q174;
            Q174=makeQuery(id+"F4.imprint","IMPRINT",FACE,{"disambiguationData":[TD([[makeQuery(id+"F4.imprint","IMPRINT",EDGE,{"derivedFrom":sQuery(id+"F4.wireOp",EDGE,"E8.0.9.11")}),1.0]])]});
            var Q175;
            Q175=makeQuery(id+"F4.imprint","IMPRINT",FACE,{"disambiguationData":[TD([[makeQuery(id+"F4.imprint","IMPRINT",EDGE,{"derivedFrom":sQuery(id+"F4.wireOp",EDGE,"E8.0.10.13")}),1.0]])]});
            var Q176;
            Q176=makeQuery(id+"F4.imprint","IMPRINT",FACE,{"disambiguationData":[TD([[makeQuery(id+"F4.imprint","IMPRINT",EDGE,{"derivedFrom":sQuery(id+"F4.wireOp",EDGE,"E8.0.1.15")}),1.0]])]});
            var Q177;
            Q177=makeQuery(id+"F4.imprint","IMPRINT",FACE,{"disambiguationData":[TD([[makeQuery(id+"F4.imprint","IMPRINT",EDGE,{"derivedFrom":sQuery(id+"F4.wireOp",EDGE,"E8.0.3.3")}),1.0]])]});
            var Q178;
            Q178=makeQuery(id+"F4.imprint","IMPRINT",FACE,{"disambiguationData":[TD([[makeQuery(id+"F4.imprint","IMPRINT",EDGE,{"derivedFrom":sQuery(id+"F4.wireOp",EDGE,"E8.0.4.5")}),1.0]])]});
            var Q179;
            Q179=makeQuery(id+"F4.imprint","IMPRINT",FACE,{"disambiguationData":[TD([[makeQuery(id+"F4.imprint","IMPRINT",EDGE,{"derivedFrom":sQuery(id+"F4.wireOp",EDGE,"E8.0.5.7")}),1.0]])]});
            var Q180;
            Q180=makeQuery(id+"F4.imprint","IMPRINT",FACE,{"disambiguationData":[TD([[makeQuery(id+"F4.imprint","IMPRINT",EDGE,{"derivedFrom":sQuery(id+"F4.wireOp",EDGE,"E7.13.1.0")}),1.0]])]});
            var Q181;
            Q181=makeQuery(id+"F4.imprint","IMPRINT",FACE,{"disambiguationData":[TD([[makeQuery(id+"F4.imprint","IMPRINT",EDGE,{"derivedFrom":sQuery(id+"F4.wireOp",EDGE,"E8.0.0.13")}),1.0]])]});
            var Q182;
            Q182=makeQuery(id+"F4.imprint","IMPRINT",FACE,{"disambiguationData":[TD([[makeQuery(id+"F4.imprint","IMPRINT",EDGE,{"derivedFrom":sQuery(id+"F4.wireOp",EDGE,"E8.0.11.14")}),1.0]])]});
            var Q183;
            Q183=makeQuery(id+"F4.imprint","IMPRINT",FACE,{"disambiguationData":[TD([[makeQuery(id+"F4.imprint","IMPRINT",EDGE,{"derivedFrom":sQuery(id+"F4.wireOp",EDGE,"E8.0.13.2")}),1.0]])]});
            var Q184;
            Q184=makeQuery(id+"F4.imprint","IMPRINT",FACE,{"disambiguationData":[TD([[makeQuery(id+"F4.imprint","IMPRINT",EDGE,{"derivedFrom":sQuery(id+"F4.wireOp",EDGE,"E8.0.14.4")}),1.0]])]});
            var Q185;
            Q185=makeQuery(id+"F4.imprint","IMPRINT",FACE,{"disambiguationData":[TD([[makeQuery(id+"F4.imprint","IMPRINT",EDGE,{"derivedFrom":sQuery(id+"F4.wireOp",EDGE,"E8.0.15.6")}),1.0]])]});
            var Q186;
            Q186=makeQuery(id+"F4.imprint","IMPRINT",FACE,{"disambiguationData":[TD([[makeQuery(id+"F4.imprint","IMPRINT",EDGE,{"derivedFrom":sQuery(id+"F4.wireOp",EDGE,"E8.0.6.10")}),1.0]])]});
            var Q187;
            Q187=makeQuery(id+"F4.imprint","IMPRINT",FACE,{"disambiguationData":[TD([[makeQuery(id+"F4.imprint","IMPRINT",EDGE,{"derivedFrom":sQuery(id+"F4.wireOp",EDGE,"E8.0.8.2")}),1.0]])]});
            var Q188;
            Q188=makeQuery(id+"F4.imprint","IMPRINT",FACE,{"disambiguationData":[TD([[makeQuery(id+"F4.imprint","IMPRINT",EDGE,{"derivedFrom":sQuery(id+"F4.wireOp",EDGE,"E8.0.9.10")}),1.0]])]});
            var Q189;
            Q189=makeQuery(id+"F4.imprint","IMPRINT",FACE,{"disambiguationData":[TD([[makeQuery(id+"F4.imprint","IMPRINT",EDGE,{"derivedFrom":sQuery(id+"F4.wireOp",EDGE,"E8.0.10.12")}),1.0]])]});
            var Q190;
            Q190=makeQuery(id+"F4.imprint","IMPRINT",FACE,{"disambiguationData":[TD([[makeQuery(id+"F4.imprint","IMPRINT",EDGE,{"derivedFrom":sQuery(id+"F4.wireOp",EDGE,"E8.0.1.14")}),1.0]])]});
            var Q191;
            Q191=makeQuery(id+"F4.imprint","IMPRINT",FACE,{"disambiguationData":[TD([[makeQuery(id+"F4.imprint","IMPRINT",EDGE,{"derivedFrom":sQuery(id+"F4.wireOp",EDGE,"E8.0.3.2")}),1.0]])]});
            var Q192;
            Q192=makeQuery(id+"F4.imprint","IMPRINT",FACE,{"disambiguationData":[TD([[makeQuery(id+"F4.imprint","IMPRINT",EDGE,{"derivedFrom":sQuery(id+"F4.wireOp",EDGE,"E8.0.4.4")}),1.0]])]});
            var Q193;
            Q193=makeQuery(id+"F4.imprint","IMPRINT",FACE,{"disambiguationData":[TD([[makeQuery(id+"F4.imprint","IMPRINT",EDGE,{"derivedFrom":sQuery(id+"F4.wireOp",EDGE,"E8.0.5.6")}),1.0]])]});
            var Q194;
            Q194=makeQuery(id+"F4.imprint","IMPRINT",FACE,{"disambiguationData":[TD([[makeQuery(id+"F4.imprint","IMPRINT",EDGE,{"derivedFrom":sQuery(id+"F4.wireOp",EDGE,"E7.13.0.0")}),1.0]])]});
            var Q195;
            Q195=makeQuery(id+"F4.imprint","IMPRINT",FACE,{"disambiguationData":[TD([[makeQuery(id+"F4.imprint","IMPRINT",EDGE,{"derivedFrom":sQuery(id+"F4.wireOp",EDGE,"E8.0.0.12")}),1.0]])]});
            var Q196;
            {var subQ0=sQuery(id+"F4.wireOp",EDGE,"E8.6.9.7");Q196=makeQuery(id+"F4.imprint","IMPRINT",FACE,{"disambiguationData":[TD([[makeQuery(id+"F4.imprint","IMPRINT",EDGE,{"derivedFrom":subQ0}),-1.0]])]});}
            var Q197;
            Q197=makeQuery(id+"F4.imprint","IMPRINT",FACE,{"disambiguationData":[TD([[makeQuery(id+"F4.imprint","IMPRINT",EDGE,{"derivedFrom":sQuery(id+"F4.wireOp",EDGE,"E8.0.7.15")}),1.0]])]});
            var Q198;
            Q198=makeQuery(id+"F4.imprint","IMPRINT",FACE,{"disambiguationData":[TD([[makeQuery(id+"F4.imprint","IMPRINT",EDGE,{"derivedFrom":sQuery(id+"F4.wireOp",EDGE,"E8.0.6.9")}),1.0]])]});
            var Q199;
            Q199=makeQuery(id+"F4.imprint","IMPRINT",FACE,{"disambiguationData":[TD([[makeQuery(id+"F4.imprint","IMPRINT",EDGE,{"derivedFrom":sQuery(id+"F4.wireOp",EDGE,"E8.0.9.9")}),1.0]])]});
            var Q200;
            Q200=makeQuery(id+"F4.imprint","IMPRINT",FACE,{"disambiguationData":[TD([[makeQuery(id+"F4.imprint","IMPRINT",EDGE,{"derivedFrom":sQuery(id+"F4.wireOp",EDGE,"E8.0.10.11")}),1.0]])]});
            var Q201;
            Q201=makeQuery(id+"F4.imprint","IMPRINT",FACE,{"disambiguationData":[TD([[makeQuery(id+"F4.imprint","IMPRINT",EDGE,{"derivedFrom":sQuery(id+"F4.wireOp",EDGE,"E8.0.1.13")}),1.0]])]});
            var Q202;
            Q202=makeQuery(id+"F4.imprint","IMPRINT",FACE,{"disambiguationData":[TD([[makeQuery(id+"F4.imprint","IMPRINT",EDGE,{"derivedFrom":sQuery(id+"F4.wireOp",EDGE,"E8.0.2.15")}),1.0]])]});
            var Q203;
            Q203=makeQuery(id+"F4.imprint","IMPRINT",FACE,{"disambiguationData":[TD([[makeQuery(id+"F4.imprint","IMPRINT",EDGE,{"derivedFrom":sQuery(id+"F4.wireOp",EDGE,"E8.0.4.3")}),1.0]])]});
            var Q204;
            Q204=makeQuery(id+"F4.imprint","IMPRINT",FACE,{"disambiguationData":[TD([[makeQuery(id+"F4.imprint","IMPRINT",EDGE,{"derivedFrom":sQuery(id+"F4.wireOp",EDGE,"E8.0.5.5")}),1.0]])]});
            var Q205;
            Q205=makeQuery(id+"F4.imprint","IMPRINT",FACE,{"disambiguationData":[TD([[makeQuery(id+"F4.imprint","IMPRINT",EDGE,{"derivedFrom":sQuery(id+"F4.wireOp",EDGE,"E8.0.0.11")}),1.0]])]});
            var Q206;
            Q206=makeQuery(id+"F4.imprint","IMPRINT",FACE,{"disambiguationData":[TD([[makeQuery(id+"F4.imprint","IMPRINT",EDGE,{"derivedFrom":sQuery(id+"F4.wireOp",EDGE,"E7.12.1.0")}),1.0]])]});
            var Q207;
            {var subQ5=sQuery(id+"F4.wireOp",EDGE,"E8.0.8.9");Q207=makeQuery(id+"F4.imprint","IMPRINT",FACE,{"disambiguationData":[TD([[makeQuery(id+"F4.imprint","IMPRINT",EDGE,{"derivedFrom":subQ5}),1.0]])]});}
            var Q208;
            Q208=makeQuery(id+"F4.imprint","IMPRINT",FACE,{"disambiguationData":[TD([[makeQuery(id+"F4.imprint","IMPRINT",EDGE,{"derivedFrom":sQuery(id+"F4.wireOp",EDGE,"E8.0.11.13")}),1.0]])]});
            var Q209;
            Q209=makeQuery(id+"F4.imprint","IMPRINT",FACE,{"disambiguationData":[TD([[makeQuery(id+"F4.imprint","IMPRINT",EDGE,{"derivedFrom":sQuery(id+"F4.wireOp",EDGE,"E8.0.14.3")}),1.0]])]});
            var Q210;
            Q210=makeQuery(id+"F4.imprint","IMPRINT",FACE,{"disambiguationData":[TD([[makeQuery(id+"F4.imprint","IMPRINT",EDGE,{"derivedFrom":sQuery(id+"F4.wireOp",EDGE,"E8.0.12.15")}),1.0]])]});
            var Q211;
            Q211=makeQuery(id+"F4.imprint","IMPRINT",FACE,{"disambiguationData":[TD([[makeQuery(id+"F4.imprint","IMPRINT",EDGE,{"derivedFrom":sQuery(id+"F4.wireOp",EDGE,"E8.0.15.5")}),1.0]])]});
            var Q212;
            Q212=makeQuery(id+"F4.imprint","IMPRINT",FACE,{"disambiguationData":[TD([[makeQuery(id+"F4.imprint","IMPRINT",EDGE,{"derivedFrom":sQuery(id+"F4.wireOp",EDGE,"E8.0.1.12")}),1.0]])]});
            var Q213;
            Q213=makeQuery(id+"F4.imprint","IMPRINT",FACE,{"disambiguationData":[TD([[makeQuery(id+"F4.imprint","IMPRINT",EDGE,{"derivedFrom":sQuery(id+"F4.wireOp",EDGE,"E8.0.2.14")}),1.0]])]});
            var Q214;
            Q214=makeQuery(id+"F4.imprint","IMPRINT",FACE,{"disambiguationData":[TD([[makeQuery(id+"F4.imprint","IMPRINT",EDGE,{"derivedFrom":sQuery(id+"F4.wireOp",EDGE,"E8.0.4.2")}),1.0]])]});
            var Q215;
            Q215=makeQuery(id+"F4.imprint","IMPRINT",FACE,{"disambiguationData":[TD([[makeQuery(id+"F4.imprint","IMPRINT",EDGE,{"derivedFrom":sQuery(id+"F4.wireOp",EDGE,"E8.0.5.4")}),1.0]])]});
            var Q216;
            Q216=makeQuery(id+"F4.imprint","IMPRINT",FACE,{"disambiguationData":[TD([[makeQuery(id+"F4.imprint","IMPRINT",EDGE,{"derivedFrom":sQuery(id+"F4.wireOp",EDGE,"E7.12.0.0")}),1.0]])]});
            var Q217;
            Q217=makeQuery(id+"F4.imprint","IMPRINT",FACE,{"disambiguationData":[TD([[makeQuery(id+"F4.imprint","IMPRINT",EDGE,{"derivedFrom":sQuery(id+"F4.wireOp",EDGE,"E8.0.0.10")}),1.0]])]});
            var Q218;
            {var subQ1=sQuery(id+"F4.wireOp",EDGE,"E8.0.7.7");Q218=makeQuery(id+"F4.imprint","IMPRINT",FACE,{"disambiguationData":[TD([[makeQuery(id+"F4.imprint","IMPRINT",EDGE,{"derivedFrom":subQ1}),1.0]])]});}
            var Q219;
            Q219=makeQuery(id+"F4.imprint","IMPRINT",FACE,{"disambiguationData":[TD([[makeQuery(id+"F4.imprint","IMPRINT",EDGE,{"derivedFrom":sQuery(id+"F4.wireOp",EDGE,"E8.0.11.12")}),1.0]])]});
            var Q220;
            Q220=makeQuery(id+"F4.imprint","IMPRINT",FACE,{"disambiguationData":[TD([[makeQuery(id+"F4.imprint","IMPRINT",EDGE,{"derivedFrom":sQuery(id+"F4.wireOp",EDGE,"E8.0.12.14")}),1.0]])]});
            var Q221;
            Q221=makeQuery(id+"F4.imprint","IMPRINT",FACE,{"disambiguationData":[TD([[makeQuery(id+"F4.imprint","IMPRINT",EDGE,{"derivedFrom":sQuery(id+"F4.wireOp",EDGE,"E8.0.14.2")}),1.0]])]});
            var Q222;
            Q222=makeQuery(id+"F4.imprint","IMPRINT",FACE,{"disambiguationData":[TD([[makeQuery(id+"F4.imprint","IMPRINT",EDGE,{"derivedFrom":sQuery(id+"F4.wireOp",EDGE,"E8.0.15.4")}),1.0]])]});
            var Q223;
            Q223=makeQuery(id+"F4.imprint","IMPRINT",FACE,{"disambiguationData":[TD([[makeQuery(id+"F4.imprint","IMPRINT",EDGE,{"derivedFrom":sQuery(id+"F4.wireOp",EDGE,"E8.0.6.6")}),1.0]])]});
            var Q224;
            Q224=makeQuery(id+"F4.imprint","IMPRINT",FACE,{"disambiguationData":[TD([[makeQuery(id+"F4.imprint","IMPRINT",EDGE,{"derivedFrom":sQuery(id+"F4.wireOp",EDGE,"E8.0.7.14")}),1.0]])]});
            var Q225;
            Q225=makeQuery(id+"F4.imprint","IMPRINT",FACE,{"disambiguationData":[TD([[makeQuery(id+"F4.imprint","IMPRINT",EDGE,{"derivedFrom":sQuery(id+"F4.wireOp",EDGE,"E8.0.10.10")}),1.0]])]});
            var Q226;
            Q226=makeQuery(id+"F4.imprint","IMPRINT",FACE,{"disambiguationData":[TD([[makeQuery(id+"F4.imprint","IMPRINT",EDGE,{"derivedFrom":sQuery(id+"F4.wireOp",EDGE,"E8.0.9.6")}),1.0]])]});
            var Q227;
            Q227=makeQuery(id+"F4.imprint","IMPRINT",FACE,{"disambiguationData":[TD([[makeQuery(id+"F4.imprint","IMPRINT",EDGE,{"derivedFrom":sQuery(id+"F4.wireOp",EDGE,"E7.11.1.0")}),1.0]])]});
            var Q228;
            Q228=makeQuery(id+"F4.imprint","IMPRINT",FACE,{"disambiguationData":[TD([[makeQuery(id+"F4.imprint","IMPRINT",EDGE,{"derivedFrom":sQuery(id+"F4.wireOp",EDGE,"E8.0.0.9")}),1.0]])]});
            var Q229;
            Q229=makeQuery(id+"F4.imprint","IMPRINT",FACE,{"disambiguationData":[TD([[makeQuery(id+"F4.imprint","IMPRINT",EDGE,{"derivedFrom":sQuery(id+"F4.wireOp",EDGE,"E8.0.11.11")}),1.0]])]});
            var Q230;
            Q230=makeQuery(id+"F4.imprint","IMPRINT",FACE,{"disambiguationData":[TD([[makeQuery(id+"F4.imprint","IMPRINT",EDGE,{"derivedFrom":sQuery(id+"F4.wireOp",EDGE,"E8.0.12.13")}),1.0]])]});
            var Q231;
            Q231=makeQuery(id+"F4.imprint","IMPRINT",FACE,{"disambiguationData":[TD([[makeQuery(id+"F4.imprint","IMPRINT",EDGE,{"derivedFrom":sQuery(id+"F4.wireOp",EDGE,"E8.0.13.15")}),1.0]])]});
            var Q232;
            Q232=makeQuery(id+"F4.imprint","IMPRINT",FACE,{"disambiguationData":[TD([[makeQuery(id+"F4.imprint","IMPRINT",EDGE,{"derivedFrom":sQuery(id+"F4.wireOp",EDGE,"E8.0.15.3")}),1.0]])]});
            var Q233;
            Q233=makeQuery(id+"F4.imprint","IMPRINT",FACE,{"disambiguationData":[TD([[makeQuery(id+"F4.imprint","IMPRINT",EDGE,{"derivedFrom":sQuery(id+"F4.wireOp",EDGE,"E8.0.6.5")}),1.0]])]});
            var Q234;
            Q234=makeQuery(id+"F4.imprint","IMPRINT",FACE,{"disambiguationData":[TD([[makeQuery(id+"F4.imprint","IMPRINT",EDGE,{"derivedFrom":sQuery(id+"F4.wireOp",EDGE,"E8.0.7.13")}),1.0]])]});
            var Q235;
            Q235=makeQuery(id+"F4.imprint","IMPRINT",FACE,{"disambiguationData":[TD([[makeQuery(id+"F4.imprint","IMPRINT",EDGE,{"derivedFrom":sQuery(id+"F4.wireOp",EDGE,"E8.0.9.5")}),1.0]])]});
            var Q236;
            Q236=makeQuery(id+"F4.imprint","IMPRINT",FACE,{"disambiguationData":[TD([[makeQuery(id+"F4.imprint","IMPRINT",EDGE,{"derivedFrom":sQuery(id+"F4.wireOp",EDGE,"E8.0.10.9")}),1.0]])]});
            var Q237;
            Q237=makeQuery(id+"F4.imprint","IMPRINT",FACE,{"disambiguationData":[TD([[makeQuery(id+"F4.imprint","IMPRINT",EDGE,{"derivedFrom":sQuery(id+"F4.wireOp",EDGE,"E8.0.1.11")}),1.0]])]});
            var Q238;
            Q238=makeQuery(id+"F4.imprint","IMPRINT",FACE,{"disambiguationData":[TD([[makeQuery(id+"F4.imprint","IMPRINT",EDGE,{"derivedFrom":sQuery(id+"F4.wireOp",EDGE,"E8.0.2.13")}),1.0]])]});
            var Q239;
            Q239=makeQuery(id+"F4.imprint","IMPRINT",FACE,{"disambiguationData":[TD([[makeQuery(id+"F4.imprint","IMPRINT",EDGE,{"derivedFrom":sQuery(id+"F4.wireOp",EDGE,"E8.0.3.15")}),1.0]])]});
            var Q240;
            Q240=makeQuery(id+"F4.imprint","IMPRINT",FACE,{"disambiguationData":[TD([[makeQuery(id+"F4.imprint","IMPRINT",EDGE,{"derivedFrom":sQuery(id+"F4.wireOp",EDGE,"E8.0.5.3")}),1.0]])]});
            var Q241;
            {var subQ0=sQuery(id+"F4.wireOp",EDGE,"E8.6.8.6");Q241=makeQuery(id+"F4.imprint","IMPRINT",FACE,{"disambiguationData":[TD([[makeQuery(id+"F4.imprint","IMPRINT",EDGE,{"derivedFrom":subQ0}),-1.0]])]});}
            var Q242;
            Q242=makeQuery(id+"F4.imprint","IMPRINT",FACE,{"disambiguationData":[TD([[makeQuery(id+"F4.imprint","IMPRINT",EDGE,{"derivedFrom":sQuery(id+"F4.wireOp",EDGE,"E8.0.11.10")}),1.0]])]});
            var Q243;
            Q243=makeQuery(id+"F4.imprint","IMPRINT",FACE,{"disambiguationData":[TD([[makeQuery(id+"F4.imprint","IMPRINT",EDGE,{"derivedFrom":sQuery(id+"F4.wireOp",EDGE,"E8.0.12.12")}),1.0]])]});
            var Q244;
            Q244=makeQuery(id+"F4.imprint","IMPRINT",FACE,{"disambiguationData":[TD([[makeQuery(id+"F4.imprint","IMPRINT",EDGE,{"derivedFrom":sQuery(id+"F4.wireOp",EDGE,"E8.0.13.14")}),1.0]])]});
            var Q245;
            Q245=makeQuery(id+"F4.imprint","IMPRINT",FACE,{"disambiguationData":[TD([[makeQuery(id+"F4.imprint","IMPRINT",EDGE,{"derivedFrom":sQuery(id+"F4.wireOp",EDGE,"E8.0.15.2")}),1.0]])]});
            var Q246;
            Q246=makeQuery(id+"F4.imprint","IMPRINT",FACE,{"disambiguationData":[TD([[makeQuery(id+"F4.imprint","IMPRINT",EDGE,{"derivedFrom":sQuery(id+"F4.wireOp",EDGE,"E8.0.6.4")}),1.0]])]});
            var Q247;
            Q247=makeQuery(id+"F4.imprint","IMPRINT",FACE,{"disambiguationData":[TD([[makeQuery(id+"F4.imprint","IMPRINT",EDGE,{"derivedFrom":sQuery(id+"F4.wireOp",EDGE,"E8.0.7.12")}),1.0]])]});
            var Q248;
            Q248=makeQuery(id+"F4.imprint","IMPRINT",FACE,{"disambiguationData":[TD([[makeQuery(id+"F4.imprint","IMPRINT",EDGE,{"derivedFrom":sQuery(id+"F4.wireOp",EDGE,"E8.0.9.4")}),1.0]])]});
            var Q249;
            Q249=makeQuery(id+"F4.imprint","IMPRINT",FACE,{"disambiguationData":[TD([[makeQuery(id+"F4.imprint","IMPRINT",EDGE,{"derivedFrom":sQuery(id+"F4.wireOp",EDGE,"E8.0.10.8")}),1.0]])]});
            var Q250;
            Q250=makeQuery(id+"F4.imprint","IMPRINT",FACE,{"disambiguationData":[TD([[makeQuery(id+"F4.imprint","IMPRINT",EDGE,{"derivedFrom":sQuery(id+"F4.wireOp",EDGE,"E8.0.1.10")}),1.0]])]});
            var Q251;
            Q251=makeQuery(id+"F4.imprint","IMPRINT",FACE,{"disambiguationData":[TD([[makeQuery(id+"F4.imprint","IMPRINT",EDGE,{"derivedFrom":sQuery(id+"F4.wireOp",EDGE,"E8.0.2.12")}),1.0]])]});
            var Q252;
            Q252=makeQuery(id+"F4.imprint","IMPRINT",FACE,{"disambiguationData":[TD([[makeQuery(id+"F4.imprint","IMPRINT",EDGE,{"derivedFrom":sQuery(id+"F4.wireOp",EDGE,"E8.0.3.14")}),1.0]])]});
            var Q253;
            Q253=makeQuery(id+"F4.imprint","IMPRINT",FACE,{"disambiguationData":[TD([[makeQuery(id+"F4.imprint","IMPRINT",EDGE,{"derivedFrom":sQuery(id+"F4.wireOp",EDGE,"E8.0.5.2")}),1.0]])]});
            var Q254;
            Q254=makeQuery(id+"F4.imprint","IMPRINT",FACE,{"disambiguationData":[TD([[makeQuery(id+"F4.imprint","IMPRINT",EDGE,{"derivedFrom":sQuery(id+"F4.wireOp",EDGE,"E7.11.0.0")}),1.0]])]});
            var Q255;
            Q255=makeQuery(id+"F4.imprint","IMPRINT",FACE,{"disambiguationData":[TD([[makeQuery(id+"F4.imprint","IMPRINT",EDGE,{"derivedFrom":sQuery(id+"F4.wireOp",EDGE,"E8.0.0.8")}),1.0]])]});
            var Q256;
            {var subQ0=sQuery(id+"F4.wireOp",EDGE,"E8.9.7.6");var subQ1=sQuery(id+"F4.wireOp",EDGE,"E6");var subQ2=makeQuery(id+"F4.imprint","INTERSECT",VERTEX,{"derivedFrom":[subQ1,subQ0]});Q256=makeQuery(id+"F4.imprint","IMPRINT",FACE,{"disambiguationData":[TD([[makeQuery(id+"F4.imprint","IMPRINT",EDGE,{"disambiguationData":[TD([[subQ2,-1.0]])],"derivedFrom":subQ1}),-1.0]])]});}
            var Q257;
            {var subQ6=sQuery(id+"F4.wireOp",EDGE,"E8.0.7.7");Q257=makeQuery(id+"F4.imprint","IMPRINT",FACE,{"disambiguationData":[TD([[makeQuery(id+"F4.imprint","IMPRINT",EDGE,{"derivedFrom":subQ6}),-1.0]])]});}
            var Q258;
            {var subQ0=sQuery(id+"F4.wireOp",EDGE,"E8.6.7.7");var subQ1=sQuery(id+"F4.wireOp",EDGE,"E6");var subQ2=makeQuery(id+"F4.imprint","INTERSECT",VERTEX,{"derivedFrom":[subQ1,subQ0]});Q258=makeQuery(id+"F4.imprint","IMPRINT",FACE,{"disambiguationData":[TD([[makeQuery(id+"F4.imprint","IMPRINT",EDGE,{"disambiguationData":[TD([[subQ2,-1.0]])],"derivedFrom":subQ1}),-1.0]])]});}
            var Q259;
            {var subQ0=sQuery(id+"F4.wireOp",EDGE,"E8.9.8.8");var subQ1=sQuery(id+"F4.wireOp",EDGE,"E6");var subQ2=makeQuery(id+"F4.imprint","INTERSECT",VERTEX,{"derivedFrom":[subQ1,subQ0]});Q259=makeQuery(id+"F4.imprint","IMPRINT",FACE,{"disambiguationData":[TD([[makeQuery(id+"F4.imprint","IMPRINT",EDGE,{"disambiguationData":[TD([[subQ2,-1.0]])],"derivedFrom":subQ1}),-1.0]])]});}
            var Q260;
            {var subQ0=sQuery(id+"F4.wireOp",EDGE,"E8.0.8.8");var subQ1=sQuery(id+"F4.wireOp",EDGE,"E6");var subQ2=makeQuery(id+"F4.imprint","INTERSECT",VERTEX,{"derivedFrom":[subQ1,subQ0]});Q260=makeQuery(id+"F4.imprint","IMPRINT",FACE,{"disambiguationData":[TD([[makeQuery(id+"F4.imprint","IMPRINT",EDGE,{"disambiguationData":[TD([[subQ2,-1.0]])],"derivedFrom":subQ1}),-1.0]])]});}
            var Q261;
            {var subQ0=sQuery(id+"F4.wireOp",EDGE,"E8.9.8.7");var subQ1=sQuery(id+"F4.wireOp",EDGE,"E6");var subQ2=makeQuery(id+"F4.imprint","INTERSECT",VERTEX,{"derivedFrom":[subQ1,subQ0]});Q261=makeQuery(id+"F4.imprint","IMPRINT",FACE,{"disambiguationData":[TD([[makeQuery(id+"F4.imprint","IMPRINT",EDGE,{"disambiguationData":[TD([[subQ2,-1.0]])],"derivedFrom":subQ1}),-1.0]])]});}
            var Q262;
            {var subQ0=sQuery(id+"F4.wireOp",EDGE,"E8.3.8.9");var subQ1=sQuery(id+"F4.wireOp",EDGE,"E6");var subQ2=makeQuery(id+"F4.imprint","INTERSECT",VERTEX,{"derivedFrom":[subQ1,subQ0]});Q262=makeQuery(id+"F4.imprint","IMPRINT",FACE,{"disambiguationData":[TD([[makeQuery(id+"F4.imprint","IMPRINT",EDGE,{"disambiguationData":[TD([[subQ2,-1.0]])],"derivedFrom":subQ1}),-1.0]])]});}
            var Q263;
            {var subQ0=sQuery(id+"F4.wireOp",EDGE,"E8.3.9.7");var subQ1=sQuery(id+"F4.wireOp",EDGE,"E6");var subQ2=makeQuery(id+"F4.imprint","INTERSECT",VERTEX,{"derivedFrom":[subQ1,subQ0]});Q263=makeQuery(id+"F4.imprint","IMPRINT",FACE,{"disambiguationData":[TD([[makeQuery(id+"F4.imprint","IMPRINT",EDGE,{"disambiguationData":[TD([[subQ2,-1.0]])],"derivedFrom":subQ1}),-1.0]])]});}
            var Q264;
            {var subQ0=sQuery(id+"F4.wireOp",EDGE,"E8.6.8.9");var subQ1=sQuery(id+"F4.wireOp",EDGE,"E6");var subQ2=makeQuery(id+"F4.imprint","INTERSECT",VERTEX,{"derivedFrom":[subQ1,subQ0]});Q264=makeQuery(id+"F4.imprint","IMPRINT",FACE,{"disambiguationData":[TD([[makeQuery(id+"F4.imprint","IMPRINT",EDGE,{"disambiguationData":[TD([[subQ2,-1.0]])],"derivedFrom":subQ1}),-1.0]])]});}
            var Q265;
            {var subQ0=sQuery(id+"F4.wireOp",EDGE,"E8.6.8.7");var subQ1=sQuery(id+"F4.wireOp",EDGE,"E6");var subQ2=makeQuery(id+"F4.imprint","INTERSECT",VERTEX,{"derivedFrom":[subQ1,subQ0]});Q265=makeQuery(id+"F4.imprint","IMPRINT",FACE,{"disambiguationData":[TD([[makeQuery(id+"F4.imprint","IMPRINT",EDGE,{"disambiguationData":[TD([[subQ2,-1.0]])],"derivedFrom":subQ1}),-1.0]])]});}
            var Q266;
            {var subQ0=sQuery(id+"F4.wireOp",EDGE,"E8.6.7.9");var subQ1=sQuery(id+"F4.wireOp",EDGE,"E6");var subQ2=makeQuery(id+"F4.imprint","INTERSECT",VERTEX,{"derivedFrom":[subQ1,subQ0]});Q266=makeQuery(id+"F4.imprint","IMPRINT",FACE,{"disambiguationData":[TD([[makeQuery(id+"F4.imprint","IMPRINT",EDGE,{"disambiguationData":[TD([[subQ2,-1.0]])],"derivedFrom":subQ1}),-1.0]])]});}
            var Q267;
            {var subQ0=sQuery(id+"F4.wireOp",EDGE,"E8.0.7.8");var subQ1=sQuery(id+"F4.wireOp",EDGE,"E6");var subQ2=makeQuery(id+"F4.imprint","INTERSECT",VERTEX,{"derivedFrom":[subQ1,subQ0]});Q267=makeQuery(id+"F4.imprint","IMPRINT",FACE,{"disambiguationData":[TD([[makeQuery(id+"F4.imprint","IMPRINT",EDGE,{"disambiguationData":[TD([[subQ2,-1.0]])],"derivedFrom":subQ1}),-1.0]])]});}
            var Q268;
            {var subQ0=sQuery(id+"F4.wireOp",EDGE,"E8.6.6.8");var subQ1=sQuery(id+"F4.wireOp",EDGE,"E6");var subQ2=makeQuery(id+"F4.imprint","INTERSECT",VERTEX,{"derivedFrom":[subQ1,subQ0]});Q268=makeQuery(id+"F4.imprint","IMPRINT",FACE,{"disambiguationData":[TD([[makeQuery(id+"F4.imprint","IMPRINT",EDGE,{"disambiguationData":[TD([[subQ2,-1.0]])],"derivedFrom":subQ1}),-1.0]])]});}
            var Q269;
            {var subQ0=sQuery(id+"F4.wireOp",EDGE,"E8.9.6.7");var subQ1=sQuery(id+"F4.wireOp",EDGE,"E6");var subQ2=makeQuery(id+"F4.imprint","INTERSECT",VERTEX,{"derivedFrom":[subQ1,subQ0]});Q269=makeQuery(id+"F4.imprint","IMPRINT",FACE,{"disambiguationData":[TD([[makeQuery(id+"F4.imprint","IMPRINT",EDGE,{"disambiguationData":[TD([[subQ2,-1.0]])],"derivedFrom":subQ1}),-1.0]])]});}
            var Q270;
            {var subQ0=sQuery(id+"F4.wireOp",EDGE,"E8.3.9.8");var subQ1=sQuery(id+"F4.wireOp",EDGE,"E6");var subQ2=makeQuery(id+"F4.imprint","INTERSECT",VERTEX,{"derivedFrom":[subQ1,subQ0]});Q270=makeQuery(id+"F4.imprint","IMPRINT",FACE,{"disambiguationData":[TD([[makeQuery(id+"F4.imprint","IMPRINT",EDGE,{"disambiguationData":[TD([[subQ2,-1.0]])],"derivedFrom":subQ1}),-1.0]])]});}
            var Q271;
            {var subQ0=sQuery(id+"F4.wireOp",EDGE,"E8.6.7.7");var subQ1=sQuery(id+"F4.wireOp",EDGE,"E8.3.7.7");var subQ2=makeQuery(id+"F4.imprint","INTERSECT",VERTEX,{"derivedFrom":[subQ1,subQ0]});Q271=makeQuery(id+"F4.imprint","IMPRINT",FACE,{"disambiguationData":[TD([[makeQuery(id+"F4.imprint","IMPRINT",EDGE,{"disambiguationData":[TD([[subQ2,-1.0]])],"derivedFrom":subQ1}),1.0]])]});}
            var Q272;
            {var subQ0=sQuery(id+"F4.wireOp",EDGE,"E8.0.7.6");var subQ1=sQuery(id+"F4.wireOp",EDGE,"E6");var subQ2=makeQuery(id+"F4.imprint","INTERSECT",VERTEX,{"derivedFrom":[subQ1,subQ0]});Q272=makeQuery(id+"F4.imprint","IMPRINT",FACE,{"disambiguationData":[TD([[makeQuery(id+"F4.imprint","IMPRINT",EDGE,{"disambiguationData":[TD([[subQ2,-1.0]])],"derivedFrom":subQ1}),-1.0]])]});}
            var Q273;
            {var subQ0=sQuery(id+"F4.wireOp",EDGE,"E8.3.7.8");var subQ1=sQuery(id+"F4.wireOp",EDGE,"E8.0.7.8");var subQ2=makeQuery(id+"F4.imprint","INTERSECT",VERTEX,{"derivedFrom":[subQ1,subQ0]});Q273=makeQuery(id+"F4.imprint","IMPRINT",FACE,{"disambiguationData":[TD([[makeQuery(id+"F4.imprint","IMPRINT",EDGE,{"disambiguationData":[TD([[subQ2,-1.0]])],"derivedFrom":subQ1}),1.0]])]});}
            var Q274;
            {var subQ0=sQuery(id+"F4.wireOp",EDGE,"E8.3.8.6");var subQ1=sQuery(id+"F4.wireOp",EDGE,"E6");var subQ2=makeQuery(id+"F4.imprint","INTERSECT",VERTEX,{"derivedFrom":[subQ1,subQ0]});Q274=makeQuery(id+"F4.imprint","IMPRINT",FACE,{"disambiguationData":[TD([[makeQuery(id+"F4.imprint","IMPRINT",EDGE,{"disambiguationData":[TD([[subQ2,-1.0]])],"derivedFrom":subQ1}),-1.0]])]});}
            var Q275;
            {var subQ0=sQuery(id+"F4.wireOp",EDGE,"E8.0.8.6");var subQ1=sQuery(id+"F4.wireOp",EDGE,"E6");var subQ2=makeQuery(id+"F4.imprint","INTERSECT",VERTEX,{"derivedFrom":[subQ1,subQ0]});Q275=makeQuery(id+"F4.imprint","IMPRINT",FACE,{"disambiguationData":[TD([[makeQuery(id+"F4.imprint","IMPRINT",EDGE,{"disambiguationData":[TD([[subQ2,-1.0]])],"derivedFrom":subQ1}),-1.0]])]});}
            var Q276;
            {var subQ0=sQuery(id+"F4.wireOp",EDGE,"E8.9.7.9");var subQ1=sQuery(id+"F4.wireOp",EDGE,"E6");var subQ2=makeQuery(id+"F4.imprint","INTERSECT",VERTEX,{"derivedFrom":[subQ1,subQ0]});Q276=makeQuery(id+"F4.imprint","IMPRINT",FACE,{"disambiguationData":[TD([[makeQuery(id+"F4.imprint","IMPRINT",EDGE,{"disambiguationData":[TD([[subQ2,-1.0]])],"derivedFrom":subQ1}),-1.0]])]});}
            var Q277;
            {var subQ0=sQuery(id+"F4.wireOp",EDGE,"E8.3.8.9");var subQ1=sQuery(id+"F4.wireOp",EDGE,"E6");var subQ2=makeQuery(id+"F4.imprint","INTERSECT",VERTEX,{"derivedFrom":[subQ1,subQ0]});Q277=makeQuery(id+"F4.imprint","IMPRINT",FACE,{"disambiguationData":[TD([[makeQuery(id+"F4.imprint","IMPRINT",EDGE,{"disambiguationData":[TD([[subQ2,-1.0]])],"derivedFrom":subQ1}),1.0]])]});}
            var Q278;
            {var subQ0=sQuery(id+"F4.wireOp",EDGE,"E8.3.9.8");var subQ1=sQuery(id+"F4.wireOp",EDGE,"E6");var subQ2=makeQuery(id+"F4.imprint","INTERSECT",VERTEX,{"derivedFrom":[subQ1,subQ0]});Q278=makeQuery(id+"F4.imprint","IMPRINT",FACE,{"disambiguationData":[TD([[makeQuery(id+"F4.imprint","IMPRINT",EDGE,{"disambiguationData":[TD([[subQ2,-1.0]])],"derivedFrom":subQ1}),1.0]])]});}
            var Q279;
            {var subQ0=sQuery(id+"F4.wireOp",EDGE,"E8.6.7.9");var subQ1=sQuery(id+"F4.wireOp",EDGE,"E6");var subQ2=makeQuery(id+"F4.imprint","INTERSECT",VERTEX,{"derivedFrom":[subQ1,subQ0]});Q279=makeQuery(id+"F4.imprint","IMPRINT",FACE,{"disambiguationData":[TD([[makeQuery(id+"F4.imprint","IMPRINT",EDGE,{"disambiguationData":[TD([[subQ2,-1.0]])],"derivedFrom":subQ1}),1.0]])]});}
            var Q280;
            {var subQ0=sQuery(id+"F4.wireOp",EDGE,"E8.3.9.7");var subQ1=sQuery(id+"F4.wireOp",EDGE,"E6");var subQ2=makeQuery(id+"F4.imprint","INTERSECT",VERTEX,{"derivedFrom":[subQ1,subQ0]});Q280=makeQuery(id+"F4.imprint","IMPRINT",FACE,{"disambiguationData":[TD([[makeQuery(id+"F4.imprint","IMPRINT",EDGE,{"disambiguationData":[TD([[subQ2,1.0]])],"derivedFrom":subQ1}),-1.0]])]});}
            var Q281;
            {var subQ0=sQuery(id+"F4.wireOp",EDGE,"E8.6.6.8");var subQ1=sQuery(id+"F4.wireOp",EDGE,"E6");var subQ2=makeQuery(id+"F4.imprint","INTERSECT",VERTEX,{"derivedFrom":[subQ1,subQ0]});Q281=makeQuery(id+"F4.imprint","IMPRINT",FACE,{"disambiguationData":[TD([[makeQuery(id+"F4.imprint","IMPRINT",EDGE,{"disambiguationData":[TD([[subQ2,-1.0]])],"derivedFrom":subQ1}),1.0]])]});}
            var Q282;
            {var subQ0=sQuery(id+"F4.wireOp",EDGE,"E8.3.7.8");var subQ1=sQuery(id+"F4.wireOp",EDGE,"E6");var subQ2=makeQuery(id+"F4.imprint","INTERSECT",VERTEX,{"derivedFrom":[subQ1,subQ0]});Q282=makeQuery(id+"F4.imprint","IMPRINT",FACE,{"disambiguationData":[TD([[makeQuery(id+"F4.imprint","IMPRINT",EDGE,{"disambiguationData":[TD([[subQ2,-1.0]])],"derivedFrom":subQ1}),-1.0]])]});}
            var Q283;
            {var subQ0=sQuery(id+"F4.wireOp",EDGE,"E8.9.6.7");var subQ1=sQuery(id+"F4.wireOp",EDGE,"E6");var subQ2=makeQuery(id+"F4.imprint","INTERSECT",VERTEX,{"derivedFrom":[subQ1,subQ0]});Q283=makeQuery(id+"F4.imprint","IMPRINT",FACE,{"disambiguationData":[TD([[makeQuery(id+"F4.imprint","IMPRINT",EDGE,{"disambiguationData":[TD([[subQ2,-1.0]])],"derivedFrom":subQ1}),1.0]])]});}
            var Q284;
            {var subQ0=sQuery(id+"F4.wireOp",EDGE,"E8.9.8.8");var subQ1=sQuery(id+"F4.wireOp",EDGE,"E8.0.8.8");var subQ2=makeQuery(id+"F4.imprint","INTERSECT",VERTEX,{"derivedFrom":[subQ1,subQ0]});Q284=makeQuery(id+"F4.imprint","IMPRINT",FACE,{"disambiguationData":[TD([[makeQuery(id+"F4.imprint","IMPRINT",EDGE,{"disambiguationData":[TD([[subQ2,1.0]])],"derivedFrom":subQ1}),1.0]])]});}
            var Q285;
            {var subQ0=sQuery(id+"F4.wireOp",EDGE,"E8.9.7.6");var subQ1=sQuery(id+"F4.wireOp",EDGE,"E6");var subQ2=makeQuery(id+"F4.imprint","INTERSECT",VERTEX,{"derivedFrom":[subQ1,subQ0]});Q285=makeQuery(id+"F4.imprint","IMPRINT",FACE,{"disambiguationData":[TD([[makeQuery(id+"F4.imprint","IMPRINT",EDGE,{"disambiguationData":[TD([[subQ2,-1.0]])],"derivedFrom":subQ1}),1.0]])]});}
            var Q286;
            {var subQ0=sQuery(id+"F4.wireOp",EDGE,"E8.9.8.7");var subQ1=sQuery(id+"F4.wireOp",EDGE,"E8.6.8.7");var subQ2=makeQuery(id+"F4.imprint","INTERSECT",VERTEX,{"derivedFrom":[subQ1,subQ0]});Q286=makeQuery(id+"F4.imprint","IMPRINT",FACE,{"disambiguationData":[TD([[makeQuery(id+"F4.imprint","IMPRINT",EDGE,{"disambiguationData":[TD([[subQ2,1.0]])],"derivedFrom":subQ1}),-1.0]])]});}
            var Q287;
            {var subQ0=sQuery(id+"F4.wireOp",EDGE,"E8.0.6.7");var subQ1=sQuery(id+"F4.wireOp",EDGE,"E6");var subQ2=makeQuery(id+"F4.imprint","INTERSECT",VERTEX,{"derivedFrom":[subQ1,subQ0]});Q287=makeQuery(id+"F4.imprint","IMPRINT",FACE,{"disambiguationData":[TD([[makeQuery(id+"F4.imprint","IMPRINT",EDGE,{"disambiguationData":[TD([[subQ2,-1.0]])],"derivedFrom":subQ1}),-1.0]])]});}
            var Q288;
            {var subQ0=sQuery(id+"F4.wireOp",EDGE,"E8.0.8.6");var subQ1=sQuery(id+"F4.wireOp",EDGE,"E6");var subQ2=makeQuery(id+"F4.imprint","INTERSECT",VERTEX,{"derivedFrom":[subQ1,subQ0]});Q288=makeQuery(id+"F4.imprint","IMPRINT",FACE,{"disambiguationData":[TD([[makeQuery(id+"F4.imprint","IMPRINT",EDGE,{"disambiguationData":[TD([[subQ2,-1.0]])],"derivedFrom":subQ1}),1.0]])]});}
            var Q289;
            {var subQ0=sQuery(id+"F4.wireOp",EDGE,"E8.3.9.7");var subQ1=sQuery(id+"F4.wireOp",EDGE,"E6");var subQ2=makeQuery(id+"F4.imprint","INTERSECT",VERTEX,{"derivedFrom":[subQ1,subQ0]});Q289=makeQuery(id+"F4.imprint","IMPRINT",FACE,{"disambiguationData":[TD([[makeQuery(id+"F4.imprint","IMPRINT",EDGE,{"disambiguationData":[TD([[subQ2,1.0]])],"derivedFrom":subQ1}),1.0]])]});}
            var Q290;
            {var subQ0=sQuery(id+"F4.wireOp",EDGE,"E8.3.7.7");var subQ1=sQuery(id+"F4.wireOp",EDGE,"E6");var subQ2=makeQuery(id+"F4.imprint","INTERSECT",VERTEX,{"derivedFrom":[subQ1,subQ0]});Q290=makeQuery(id+"F4.imprint","IMPRINT",FACE,{"disambiguationData":[TD([[makeQuery(id+"F4.imprint","IMPRINT",EDGE,{"disambiguationData":[TD([[subQ2,-1.0]])],"derivedFrom":subQ1}),-1.0]])]});}
            var Q291;
            {var subQ0=sQuery(id+"F4.wireOp",EDGE,"E8.9.6.8");var subQ1=sQuery(id+"F4.wireOp",EDGE,"E6");var subQ2=makeQuery(id+"F4.imprint","INTERSECT",VERTEX,{"derivedFrom":[subQ1,subQ0]});Q291=makeQuery(id+"F4.imprint","IMPRINT",FACE,{"disambiguationData":[TD([[makeQuery(id+"F4.imprint","IMPRINT",EDGE,{"disambiguationData":[TD([[subQ2,-1.0]])],"derivedFrom":subQ1}),-1.0]])]});}
            var Q292;
            {var subQ0=sQuery(id+"F4.wireOp",EDGE,"E8.0.9.7");var subQ1=sQuery(id+"F4.wireOp",EDGE,"E6");var subQ2=makeQuery(id+"F4.imprint","INTERSECT",VERTEX,{"derivedFrom":[subQ1,subQ0]});Q292=makeQuery(id+"F4.imprint","IMPRINT",FACE,{"disambiguationData":[TD([[makeQuery(id+"F4.imprint","IMPRINT",EDGE,{"disambiguationData":[TD([[subQ2,1.0]])],"derivedFrom":subQ1}),-1.0]])]});}
            extrude(context, id + "F5", {"entities" : qUnion([Q0, Q1, Q2, Q3, Q4, Q5, Q6, Q7, Q8, Q9, Q10, Q11, Q12, Q13, Q14, Q15, Q16, Q17, Q18, Q19, Q20, Q21, Q22, Q23, Q24, Q25, Q26, Q27, Q28, Q29, Q30, Q31, Q32, Q33, Q34, Q35, Q36, Q37, Q38, Q39, Q40, Q41, Q42, Q43, Q44, Q45, Q46, Q47, Q48, Q49, Q50, Q51, Q52, Q53, Q54, Q55, Q56, Q57, Q58, Q59, Q60, Q61, Q62, Q63, Q64, Q65, Q66, Q67, Q68, Q69, Q70, Q71, Q72, Q73, Q74, Q75, Q76, Q77, Q78, Q79, Q80, Q81, Q82, Q83, Q84, Q85, Q86, Q87, Q88, Q89, Q90, Q91, Q92, Q93, Q94, Q95, Q96, Q97, Q98, Q99, Q100, Q101, Q102, Q103, Q104, Q105, Q106, Q107, Q108, Q109, Q110, Q111, Q112, Q113, Q114, Q115, Q116, Q117, Q118, Q119, Q120, Q121, Q122, Q123, Q124, Q125, Q126, Q127, Q128, Q129, Q130, Q131, Q132, Q133, Q134, Q135, Q136, Q137, Q138, Q139, Q140, Q141, Q142, Q143, Q144, Q145, Q146, Q147, Q148, Q149, Q150, Q151, Q152, Q153, Q154, Q155, Q156, Q157, Q158, Q159, Q160, Q161, Q162, Q163, Q164, Q165, Q166, Q167, Q168, Q169, Q170, Q171, Q172, Q173, Q174, Q175, Q176, Q177, Q178, Q179, Q180, Q181, Q182, Q183, Q184, Q185, Q186, Q187, Q188, Q189, Q190, Q191, Q192, Q193, Q194, Q195, Q196, Q197, Q198, Q199, Q200, Q201, Q202, Q203, Q204, Q205, Q206, Q207, Q208, Q209, Q210, Q211, Q212, Q213, Q214, Q215, Q216, Q217, Q218, Q219, Q220, Q221, Q222, Q223, Q224, Q225, Q226, Q227, Q228, Q229, Q230, Q231, Q232, Q233, Q234, Q235, Q236, Q237, Q238, Q239, Q240, Q241, Q242, Q243, Q244, Q245, Q246, Q247, Q248, Q249, Q250, Q251, Q252, Q253, Q254, Q255, Q256, Q257, Q258, Q259, Q260, Q261, Q262, Q263, Q264, Q265, Q266, Q267, Q268, Q269, Q270, Q271, Q272, Q273, Q274, Q275, Q276, Q277, Q278, Q279, Q280, Q281, Q282, Q283, Q284, Q285, Q286, Q287, Q288, Q289, Q290, Q291, Q292]), "operationType" : NewBodyOperationType.ADD, "depth" : 0.25 * mm});
        }
        {
            var Q0;
            Q0=makeQuery(id+"F5.opExtrude","CAP_FACE",FACE,{"disambiguationData":[OSD([sQuery(id+"F4.wireOp",EDGE,"E8.0.6.7"),sQuery(id+"F4.wireOp",EDGE,"E8.3.6.7"),sQuery(id+"F4.wireOp",EDGE,"E8.6.6.7"),sQuery(id+"F4.wireOp",EDGE,"E8.9.6.7"),sQuery(id+"F4.wireOp",EDGE,"E8.0.6.8"),sQuery(id+"F4.wireOp",EDGE,"E8.3.6.8"),sQuery(id+"F4.wireOp",EDGE,"E8.6.6.8"),sQuery(id+"F4.wireOp",EDGE,"E8.9.6.8"),sQuery(id+"F4.wireOp",EDGE,"E8.0.7.6"),sQuery(id+"F4.wireOp",EDGE,"E8.3.7.6"),sQuery(id+"F4.wireOp",EDGE,"E8.6.7.6"),sQuery(id+"F4.wireOp",EDGE,"E8.9.7.6"),sQuery(id+"F4.wireOp",EDGE,"E8.3.7.7"),sQuery(id+"F4.wireOp",EDGE,"E8.6.7.7"),sQuery(id+"F4.wireOp",EDGE,"E8.0.7.8"),sQuery(id+"F4.wireOp",EDGE,"E8.3.7.8"),sQuery(id+"F4.wireOp",EDGE,"E8.0.7.9"),sQuery(id+"F4.wireOp",EDGE,"E8.3.7.9"),sQuery(id+"F4.wireOp",EDGE,"E8.6.7.9"),sQuery(id+"F4.wireOp",EDGE,"E8.9.7.9"),sQuery(id+"F4.wireOp",EDGE,"E8.0.8.6"),sQuery(id+"F4.wireOp",EDGE,"E8.3.8.6"),sQuery(id+"F4.wireOp",EDGE,"E8.6.8.6"),sQuery(id+"F4.wireOp",EDGE,"E8.9.8.6"),sQuery(id+"F4.wireOp",EDGE,"E8.6.8.7"),sQuery(id+"F4.wireOp",EDGE,"E8.9.8.7"),sQuery(id+"F4.wireOp",EDGE,"E8.0.8.8"),sQuery(id+"F4.wireOp",EDGE,"E8.9.8.8"),sQuery(id+"F4.wireOp",EDGE,"E8.0.8.9"),sQuery(id+"F4.wireOp",EDGE,"E8.3.8.9"),sQuery(id+"F4.wireOp",EDGE,"E8.6.8.9"),sQuery(id+"F4.wireOp",EDGE,"E8.9.8.9"),sQuery(id+"F4.wireOp",EDGE,"E8.0.9.7"),sQuery(id+"F4.wireOp",EDGE,"E8.3.9.7"),sQuery(id+"F4.wireOp",EDGE,"E8.6.9.7"),sQuery(id+"F4.wireOp",EDGE,"E8.9.9.7"),sQuery(id+"F4.wireOp",EDGE,"E8.0.9.8"),sQuery(id+"F4.wireOp",EDGE,"E8.3.9.8"),sQuery(id+"F4.wireOp",EDGE,"E8.6.9.8"),sQuery(id+"F4.wireOp",EDGE,"E8.9.9.8"),sQuery(id+"F4.wireOp",EDGE,"E9")])],"isStart":false});
            var sketch = newSketch(context, id + "F6", { "sketchPlane" : qUnion([Q0])});
            skCircle(sketch, "E10", {"center": v(-198.12, 304.8) * mm, "radius": 3.37 * mm});
            skSolve(sketch);
        }
        {
            var Q0;
            {var subQ0=sQuery(id+"F6.wireOp",EDGE,"E10");var subQ18=makeQuery(id+"F6.imprint","INTERSECT",VERTEX,{"derivedFrom":[makeQuery(id+"F5.opExtrude","CAP_EDGE",EDGE,{"disambiguationData":[OSD([sQuery(id+"F4.wireOp",EDGE,"E8.0.9.7")])],"isStart":false}),subQ0]});Q0=makeQuery(id+"F6.imprint","IMPRINT",FACE,{"disambiguationData":[TD([[makeQuery(id+"F6.imprint","IMPRINT",EDGE,{"disambiguationData":[TD([[subQ18,-1.0]])],"derivedFrom":subQ0}),1.0]])]});}
            extrude(context, id + "F7", {"entities" : qUnion([Q0]), "operationType" : NewBodyOperationType.REMOVE, "oppositeDirection" : true, "depth" : 25.4 * mm});
        }
        {
            var Q0;
            {var subQ1=sQuery(id+"F4.wireOp",EDGE,"E8.0.7.8");var subQ2=sQuery(id+"F6.wireOp",EDGE,"E10");Q0=makeQuery(id+"F7.boolean.opBoolean","COPY",EDGE,{"disambiguationData":[TD([makeQuery(id+"F5.opExtrude","SWEPT_FACE",FACE,{"disambiguationData":[OSD([subQ1])]})])],"derivedFrom":makeQuery(id+"F7.opExtrude","CAP_EDGE",EDGE,{"disambiguationData":[OSD([subQ2])],"isStart":true})});}
            var Q1;
            {var subQ1=sQuery(id+"F4.wireOp",EDGE,"E8.6.6.8");var subQ2=sQuery(id+"F6.wireOp",EDGE,"E10");Q1=makeQuery(id+"F7.boolean.opBoolean","COPY",EDGE,{"disambiguationData":[TD([makeQuery(id+"F5.opExtrude","SWEPT_FACE",FACE,{"disambiguationData":[OSD([subQ1])]})])],"derivedFrom":makeQuery(id+"F7.opExtrude","CAP_EDGE",EDGE,{"disambiguationData":[OSD([subQ2])],"isStart":true})});}
            var Q2;
            {var subQ0=sQuery(id+"F4.wireOp",EDGE,"E8.0.6.7");var subQ2=sQuery(id+"F6.wireOp",EDGE,"E10");Q2=makeQuery(id+"F7.boolean.opBoolean","COPY",EDGE,{"disambiguationData":[TD([makeQuery(id+"F5.opExtrude","SWEPT_FACE",FACE,{"disambiguationData":[OSD([subQ0])]})])],"derivedFrom":makeQuery(id+"F7.opExtrude","CAP_EDGE",EDGE,{"disambiguationData":[OSD([subQ2])],"isStart":true})});}
            var Q3;
            {var subQ1=sQuery(id+"F4.wireOp",EDGE,"E8.3.7.7");var subQ2=sQuery(id+"F6.wireOp",EDGE,"E10");Q3=makeQuery(id+"F7.boolean.opBoolean","COPY",EDGE,{"disambiguationData":[TD([makeQuery(id+"F5.opExtrude","SWEPT_FACE",FACE,{"disambiguationData":[OSD([subQ1])]})])],"derivedFrom":makeQuery(id+"F7.opExtrude","CAP_EDGE",EDGE,{"disambiguationData":[OSD([subQ2])],"isStart":true})});}
            var Q4;
            {var subQ1=sQuery(id+"F4.wireOp",EDGE,"E8.0.7.6");var subQ2=sQuery(id+"F6.wireOp",EDGE,"E10");Q4=makeQuery(id+"F7.boolean.opBoolean","COPY",EDGE,{"disambiguationData":[TD([makeQuery(id+"F5.opExtrude","SWEPT_FACE",FACE,{"disambiguationData":[OSD([subQ1])]})])],"derivedFrom":makeQuery(id+"F7.opExtrude","CAP_EDGE",EDGE,{"disambiguationData":[OSD([subQ2])],"isStart":true})});}
            var Q5;
            {var subQ1=sQuery(id+"F4.wireOp",EDGE,"E8.0.8.6");var subQ2=sQuery(id+"F6.wireOp",EDGE,"E10");Q5=makeQuery(id+"F7.boolean.opBoolean","COPY",EDGE,{"disambiguationData":[TD([makeQuery(id+"F5.opExtrude","SWEPT_FACE",FACE,{"disambiguationData":[OSD([subQ1])]})])],"derivedFrom":makeQuery(id+"F7.opExtrude","CAP_EDGE",EDGE,{"disambiguationData":[OSD([subQ2])],"isStart":true})});}
            var Q6;
            {var subQ1=sQuery(id+"F4.wireOp",EDGE,"E8.6.8.7");var subQ2=sQuery(id+"F6.wireOp",EDGE,"E10");Q6=makeQuery(id+"F7.boolean.opBoolean","COPY",EDGE,{"disambiguationData":[TD([makeQuery(id+"F5.opExtrude","SWEPT_FACE",FACE,{"disambiguationData":[OSD([subQ1])]})])],"derivedFrom":makeQuery(id+"F7.opExtrude","CAP_EDGE",EDGE,{"disambiguationData":[OSD([subQ2])],"isStart":true})});}
            var Q7;
            {var subQ1=sQuery(id+"F4.wireOp",EDGE,"E8.0.9.7");var subQ2=sQuery(id+"F6.wireOp",EDGE,"E10");Q7=makeQuery(id+"F7.boolean.opBoolean","COPY",EDGE,{"disambiguationData":[TD([makeQuery(id+"F5.opExtrude","SWEPT_FACE",FACE,{"disambiguationData":[OSD([subQ1])]})])],"derivedFrom":makeQuery(id+"F7.opExtrude","CAP_EDGE",EDGE,{"disambiguationData":[OSD([subQ2])],"isStart":true})});}
            var Q8;
            {var subQ1=sQuery(id+"F4.wireOp",EDGE,"E8.3.9.8");var subQ2=sQuery(id+"F6.wireOp",EDGE,"E10");Q8=makeQuery(id+"F7.boolean.opBoolean","COPY",EDGE,{"disambiguationData":[TD([makeQuery(id+"F5.opExtrude","SWEPT_FACE",FACE,{"disambiguationData":[OSD([subQ1])]})])],"derivedFrom":makeQuery(id+"F7.opExtrude","CAP_EDGE",EDGE,{"disambiguationData":[OSD([subQ2])],"isStart":true})});}
            var Q9;
            {var subQ1=sQuery(id+"F4.wireOp",EDGE,"E8.0.8.8");var subQ2=sQuery(id+"F6.wireOp",EDGE,"E10");Q9=makeQuery(id+"F7.boolean.opBoolean","COPY",EDGE,{"disambiguationData":[TD([makeQuery(id+"F5.opExtrude","SWEPT_FACE",FACE,{"disambiguationData":[OSD([subQ1])]})])],"derivedFrom":makeQuery(id+"F7.opExtrude","CAP_EDGE",EDGE,{"disambiguationData":[OSD([subQ2])],"isStart":true})});}
            var Q10;
            {var subQ1=sQuery(id+"F4.wireOp",EDGE,"E8.3.8.9");var subQ2=sQuery(id+"F6.wireOp",EDGE,"E10");Q10=makeQuery(id+"F7.boolean.opBoolean","COPY",EDGE,{"disambiguationData":[TD([makeQuery(id+"F5.opExtrude","SWEPT_FACE",FACE,{"disambiguationData":[OSD([subQ1])]})])],"derivedFrom":makeQuery(id+"F7.opExtrude","CAP_EDGE",EDGE,{"disambiguationData":[OSD([subQ2])],"isStart":true})});}
            var Q11;
            {var subQ1=sQuery(id+"F4.wireOp",EDGE,"E8.6.7.9");var subQ2=sQuery(id+"F6.wireOp",EDGE,"E10");Q11=makeQuery(id+"F7.boolean.opBoolean","COPY",EDGE,{"disambiguationData":[TD([makeQuery(id+"F5.opExtrude","SWEPT_FACE",FACE,{"disambiguationData":[OSD([subQ1])]})])],"derivedFrom":makeQuery(id+"F7.opExtrude","CAP_EDGE",EDGE,{"disambiguationData":[OSD([subQ2])],"isStart":true})});}
            chamfer(context, id + "F8", {"entities" : qUnion([Q0, Q1, Q2, Q3, Q4, Q5, Q6, Q7, Q8, Q9, Q10, Q11]), "width" : 0.13 * mm, "tangentPropagation" : true});
        }
    });
